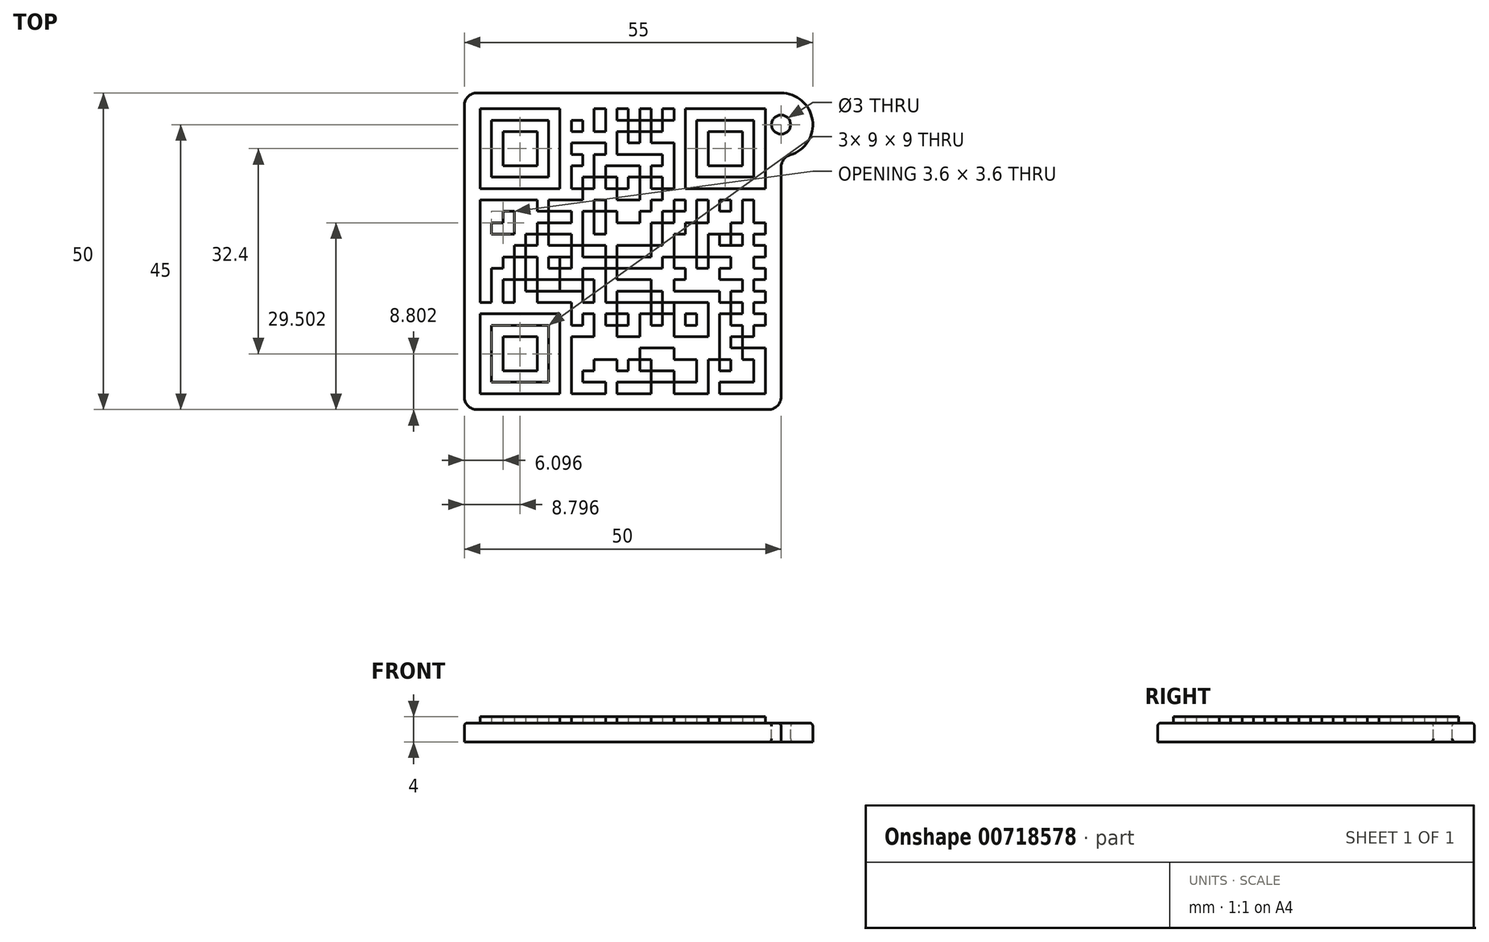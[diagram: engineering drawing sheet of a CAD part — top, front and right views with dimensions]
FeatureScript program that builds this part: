
annotation { "Feature Type Name" : "Feature", "Feature Type Description" : "" }
export const myFeature = defineFeature(function(context is Context, id is Id, definition is map)
    precondition{}
    {
        {
            var Q0;
            Q0=qCreatedBy(makeId("Top.planeOp"),FACE);
            var sketch = newSketch(context, id + "F0", { "sketchPlane" : qUnion([Q0])});
            skLineSegment(sketch, "E0.bottom", {"start": v(-25, 25) * mm, "end": v(25, 25) * mm});
            skLineSegment(sketch, "E0.top", {"start": v(-25, -25) * mm, "end": v(25, -25) * mm});
            skLineSegment(sketch, "E0.left", {"start": v(-25, 25) * mm, "end": v(-25, -25) * mm});
            skLineSegment(sketch, "E0.right", {"start": v(25, 15) * mm, "end": v(25, -25) * mm});
            skArc(sketch, "E1", {"start": v(25, 15) * mm, "mid": v(30, 20) * mm, "end": v(25, 25) * mm});
            skCircle(sketch, "E2", {"center": v(25, 20) * mm, "radius": 1.5 * mm});
            skSolve(sketch);
        }
        {
            var Q0;
            Q0 = qSketchRegion(id + "F0", true);
            extrude(context, id + "F1", {"entities" : qUnion([Q0]), "oppositeDirection" : true, "depth" : 3 * mm, "offsetDistance" : 25 * mm});
        }
        {
            var Q0;
            Q0=makeQuery(id+"F1.opExtrude","SWEPT_EDGE",EDGE,{"disambiguationData":[OSD([sQuery(id+"F0.wireOp",EDGE,"E0.top"),sQuery(id+"F0.wireOp",EDGE,"E0.left")])]});
            var Q1;
            Q1=makeQuery(id+"F1.opExtrude","SWEPT_EDGE",EDGE,{"disambiguationData":[OSD([sQuery(id+"F0.wireOp",EDGE,"E0.top"),sQuery(id+"F0.wireOp",EDGE,"E0.right")])]});
            var Q2;
            Q2=makeQuery(id+"F1.opExtrude","SWEPT_EDGE",EDGE,{"disambiguationData":[OSD([sQuery(id+"F0.wireOp",EDGE,"E0.right"),sQuery(id+"F0.wireOp",EDGE,"E1")])]});
            var Q3;
            Q3=makeQuery(id+"F1.opExtrude","SWEPT_EDGE",EDGE,{"disambiguationData":[OSD([sQuery(id+"F0.wireOp",EDGE,"E0.bottom"),sQuery(id+"F0.wireOp",EDGE,"E0.left")])]});
            fillet(context, id + "F2", {"entities" : qUnion([Q0, Q1, Q2, Q3]), "radius" : 2 * mm, "tangentPropagation" : true, "allowEdgeOverflow" : false});
        }
        {
            var Q0;
            Q0=qCreatedBy(makeId("Top.planeOp"),FACE);
            var sketch = newSketch(context, id + "F3", { "sketchPlane" : qUnion([Q0])});
            skLineSegment(sketch, "E3", {"start": v(22.5, 22.5) * mm, "end": v(22.5, -22.5) * mm});
            skLineSegment(sketch, "E4.1.0.0", {"start": v(20.7, 22.5) * mm, "end": v(20.7, -22.5) * mm});
            skLineSegment(sketch, "E4.2.0.0", {"start": v(18.9, 22.5) * mm, "end": v(18.9, -22.5) * mm});
            skLineSegment(sketch, "E4.3.0.0", {"start": v(17.1, 22.5) * mm, "end": v(17.1, -22.5) * mm});
            skLineSegment(sketch, "E4.4.0.0", {"start": v(15.3, 22.5) * mm, "end": v(15.3, -22.5) * mm});
            skLineSegment(sketch, "E4.5.0.0", {"start": v(13.5, 22.5) * mm, "end": v(13.5, -22.5) * mm});
            skLineSegment(sketch, "E4.6.0.0", {"start": v(11.7, 22.5) * mm, "end": v(11.7, -22.5) * mm});
            skLineSegment(sketch, "E4.7.0.0", {"start": v(9.9, 22.5) * mm, "end": v(9.9, -22.5) * mm});
            skLineSegment(sketch, "E4.8.0.0", {"start": v(8.1, 22.5) * mm, "end": v(8.1, -22.5) * mm});
            skLineSegment(sketch, "E4.9.0.0", {"start": v(6.3, 22.5) * mm, "end": v(6.3, -22.5) * mm});
            skLineSegment(sketch, "E4.direction1", {"start": v(22.5, -22.5) * mm, "end": v(20.7, -22.5) * mm, "construction": true});
            skLineSegment(sketch, "E5.0.10.0", {"start": v(4.5, 22.5) * mm, "end": v(4.5, -22.5) * mm});
            skLineSegment(sketch, "E5.0.11.0", {"start": v(2.7, 22.5) * mm, "end": v(2.7, -22.5) * mm});
            skLineSegment(sketch, "E6.0.12.0", {"start": v(0.9, 22.5) * mm, "end": v(0.9, -22.5) * mm});
            skLineSegment(sketch, "E6.0.13.0", {"start": v(-0.9, 22.5) * mm, "end": v(-0.9, -22.5) * mm});
            skLineSegment(sketch, "E6.0.14.0", {"start": v(-2.7, 22.5) * mm, "end": v(-2.7, -22.5) * mm});
            skLineSegment(sketch, "E6.0.15.0", {"start": v(-4.5, 22.5) * mm, "end": v(-4.5, -22.5) * mm});
            skLineSegment(sketch, "E6.0.16.0", {"start": v(-6.3, 22.5) * mm, "end": v(-6.3, -22.5) * mm});
            skLineSegment(sketch, "E6.0.17.0", {"start": v(-8.1, 22.5) * mm, "end": v(-8.1, -22.5) * mm});
            skLineSegment(sketch, "E6.0.18.0", {"start": v(-9.9, 22.5) * mm, "end": v(-9.9, -22.5) * mm});
            skLineSegment(sketch, "E6.0.19.0", {"start": v(-11.7, 22.5) * mm, "end": v(-11.7, -22.5) * mm});
            skLineSegment(sketch, "E6.0.20.0", {"start": v(-13.5, 22.5) * mm, "end": v(-13.5, -22.5) * mm});
            skLineSegment(sketch, "E6.0.21.0", {"start": v(-15.3, 22.5) * mm, "end": v(-15.3, -22.5) * mm});
            skLineSegment(sketch, "E6.0.22.0", {"start": v(-17.1, 22.5) * mm, "end": v(-17.1, -22.5) * mm});
            skLineSegment(sketch, "E6.0.23.0", {"start": v(-18.9, 22.5) * mm, "end": v(-18.9, -22.5) * mm});
            skLineSegment(sketch, "E6.0.24.0", {"start": v(-20.7, 22.5) * mm, "end": v(-20.7, -22.5) * mm});
            skLineSegment(sketch, "E6.0.25.0", {"start": v(-22.5, 22.5) * mm, "end": v(-22.5, -22.5) * mm});
            skLineSegment(sketch, "E7", {"start": v(-22.5, -22.5) * mm, "end": v(22.5, -22.5) * mm});
            skLineSegment(sketch, "E8.0.1.0", {"start": v(-22.5, -20.7) * mm, "end": v(22.5, -20.7) * mm});
            skLineSegment(sketch, "E8.0.2.0", {"start": v(-22.5, -18.9) * mm, "end": v(22.5, -18.9) * mm});
            skLineSegment(sketch, "E8.0.3.0", {"start": v(-22.5, -17.1) * mm, "end": v(22.5, -17.1) * mm});
            skLineSegment(sketch, "E8.0.4.0", {"start": v(-22.5, -15.3) * mm, "end": v(22.5, -15.3) * mm});
            skLineSegment(sketch, "E8.0.5.0", {"start": v(-22.5, -13.5) * mm, "end": v(22.5, -13.5) * mm});
            skLineSegment(sketch, "E8.0.6.0", {"start": v(-22.5, -11.7) * mm, "end": v(22.5, -11.7) * mm});
            skLineSegment(sketch, "E8.0.7.0", {"start": v(-22.5, -9.9) * mm, "end": v(22.5, -9.9) * mm});
            skLineSegment(sketch, "E8.0.8.0", {"start": v(-22.5, -8.1) * mm, "end": v(22.5, -8.1) * mm});
            skLineSegment(sketch, "E8.0.9.0", {"start": v(-22.5, -6.3) * mm, "end": v(22.5, -6.3) * mm});
            skLineSegment(sketch, "E8.0.10.0", {"start": v(-22.5, -4.5) * mm, "end": v(22.5, -4.5) * mm});
            skLineSegment(sketch, "E8.0.11.0", {"start": v(-22.5, -2.7) * mm, "end": v(22.5, -2.7) * mm});
            skLineSegment(sketch, "E8.0.12.0", {"start": v(-22.5, -0.9) * mm, "end": v(22.5, -0.9) * mm});
            skLineSegment(sketch, "E8.0.13.0", {"start": v(-22.5, 0.9) * mm, "end": v(22.5, 0.9) * mm});
            skLineSegment(sketch, "E8.0.14.0", {"start": v(-22.5, 2.7) * mm, "end": v(22.5, 2.7) * mm});
            skLineSegment(sketch, "E8.0.15.0", {"start": v(-22.5, 4.5) * mm, "end": v(22.5, 4.5) * mm});
            skLineSegment(sketch, "E8.0.16.0", {"start": v(-22.5, 6.3) * mm, "end": v(22.5, 6.3) * mm});
            skLineSegment(sketch, "E8.0.17.0", {"start": v(-22.5, 8.1) * mm, "end": v(22.5, 8.1) * mm});
            skLineSegment(sketch, "E8.0.18.0", {"start": v(-22.5, 9.9) * mm, "end": v(22.5, 9.9) * mm});
            skLineSegment(sketch, "E8.0.19.0", {"start": v(-22.5, 11.7) * mm, "end": v(22.5, 11.7) * mm});
            skLineSegment(sketch, "E8.0.20.0", {"start": v(-22.5, 13.5) * mm, "end": v(22.5, 13.5) * mm});
            skLineSegment(sketch, "E8.0.21.0", {"start": v(-22.5, 15.3) * mm, "end": v(22.5, 15.3) * mm});
            skLineSegment(sketch, "E8.0.22.0", {"start": v(-22.5, 17.1) * mm, "end": v(22.5, 17.1) * mm});
            skLineSegment(sketch, "E8.0.23.0", {"start": v(-22.5, 18.9) * mm, "end": v(22.5, 18.9) * mm});
            skLineSegment(sketch, "E8.0.24.0", {"start": v(-22.5, 20.7) * mm, "end": v(22.5, 20.7) * mm});
            skLineSegment(sketch, "E8.0.25.0", {"start": v(-22.5, 22.5) * mm, "end": v(22.5, 22.5) * mm});
            skLineSegment(sketch, "E8.direction1", {"start": v(-22.5, -22.5) * mm, "end": v(22.5, -22.5) * mm, "construction": true});
            skLineSegment(sketch, "E8.direction2", {"start": v(-22.5, -22.5) * mm, "end": v(-22.5, -20.7) * mm, "construction": true});
            skSolve(sketch);
        }
        {
            var Q0;
            {var subQ0=sQuery(id+"F3.wireOp",EDGE,"E8.0.25.0");var subQ1=sQuery(id+"F3.wireOp",EDGE,"E3");var subQ2=makeQuery(id+"F3.imprint","INTERSECT",VERTEX,{"derivedFrom":[subQ1,subQ0]});Q0=makeQuery(id+"F3.imprint","IMPRINT",FACE,{"disambiguationData":[TD([[makeQuery(id+"F3.imprint","IMPRINT",EDGE,{"disambiguationData":[TD([[subQ2,-1.0]])],"derivedFrom":subQ1}),-1.0]])]});}
            var Q1;
            {var subQ0=sQuery(id+"F3.wireOp",EDGE,"E7");var subQ1=sQuery(id+"F3.wireOp",EDGE,"E3");var subQ2=makeQuery(id+"F3.imprint","INTERSECT",VERTEX,{"derivedFrom":[subQ1,subQ0]});Q1=makeQuery(id+"F3.imprint","IMPRINT",FACE,{"disambiguationData":[TD([[makeQuery(id+"F3.imprint","IMPRINT",EDGE,{"disambiguationData":[TD([[subQ2,1.0]])],"derivedFrom":subQ1}),-1.0]])]});}
            var Q2;
            {var subQ0=sQuery(id+"F3.wireOp",EDGE,"E8.0.25.0");var subQ1=sQuery(id+"F3.wireOp",EDGE,"E6.0.24.0");var subQ2=makeQuery(id+"F3.imprint","INTERSECT",VERTEX,{"derivedFrom":[subQ1,subQ0]});Q2=makeQuery(id+"F3.imprint","IMPRINT",FACE,{"disambiguationData":[TD([[makeQuery(id+"F3.imprint","IMPRINT",EDGE,{"disambiguationData":[TD([[subQ2,-1.0]])],"derivedFrom":subQ1}),-1.0]])]});}
            var Q3;
            {var subQ0=sQuery(id+"F3.wireOp",EDGE,"E7");var subQ1=sQuery(id+"F3.wireOp",EDGE,"E6.0.24.0");var subQ2=makeQuery(id+"F3.imprint","INTERSECT",VERTEX,{"derivedFrom":[subQ1,subQ0]});Q3=makeQuery(id+"F3.imprint","IMPRINT",FACE,{"disambiguationData":[TD([[makeQuery(id+"F3.imprint","IMPRINT",EDGE,{"disambiguationData":[TD([[subQ2,1.0]])],"derivedFrom":subQ1}),-1.0]])]});}
            var Q4;
            {var subQ0=sQuery(id+"F3.wireOp",EDGE,"E8.0.23.0");var subQ1=sQuery(id+"F3.wireOp",EDGE,"E3");var subQ2=makeQuery(id+"F3.imprint","INTERSECT",VERTEX,{"derivedFrom":[subQ1,subQ0]});Q4=makeQuery(id+"F3.imprint","IMPRINT",FACE,{"disambiguationData":[TD([[makeQuery(id+"F3.imprint","IMPRINT",EDGE,{"disambiguationData":[TD([[subQ2,1.0]])],"derivedFrom":subQ1}),-1.0]])]});}
            var Q5;
            {var subQ0=sQuery(id+"F3.wireOp",EDGE,"E8.0.22.0");var subQ1=sQuery(id+"F3.wireOp",EDGE,"E3");var subQ2=makeQuery(id+"F3.imprint","INTERSECT",VERTEX,{"derivedFrom":[subQ1,subQ0]});Q5=makeQuery(id+"F3.imprint","IMPRINT",FACE,{"disambiguationData":[TD([[makeQuery(id+"F3.imprint","IMPRINT",EDGE,{"disambiguationData":[TD([[subQ2,1.0]])],"derivedFrom":subQ1}),-1.0]])]});}
            var Q6;
            {var subQ0=sQuery(id+"F3.wireOp",EDGE,"E8.0.21.0");var subQ1=sQuery(id+"F3.wireOp",EDGE,"E3");var subQ2=makeQuery(id+"F3.imprint","INTERSECT",VERTEX,{"derivedFrom":[subQ1,subQ0]});Q6=makeQuery(id+"F3.imprint","IMPRINT",FACE,{"disambiguationData":[TD([[makeQuery(id+"F3.imprint","IMPRINT",EDGE,{"disambiguationData":[TD([[subQ2,1.0]])],"derivedFrom":subQ1}),-1.0]])]});}
            var Q7;
            {var subQ0=sQuery(id+"F3.wireOp",EDGE,"E8.0.20.0");var subQ1=sQuery(id+"F3.wireOp",EDGE,"E3");var subQ2=makeQuery(id+"F3.imprint","INTERSECT",VERTEX,{"derivedFrom":[subQ1,subQ0]});Q7=makeQuery(id+"F3.imprint","IMPRINT",FACE,{"disambiguationData":[TD([[makeQuery(id+"F3.imprint","IMPRINT",EDGE,{"disambiguationData":[TD([[subQ2,1.0]])],"derivedFrom":subQ1}),-1.0]])]});}
            var Q8;
            {var subQ0=sQuery(id+"F3.wireOp",EDGE,"E8.0.19.0");var subQ1=sQuery(id+"F3.wireOp",EDGE,"E3");var subQ2=makeQuery(id+"F3.imprint","INTERSECT",VERTEX,{"derivedFrom":[subQ1,subQ0]});Q8=makeQuery(id+"F3.imprint","IMPRINT",FACE,{"disambiguationData":[TD([[makeQuery(id+"F3.imprint","IMPRINT",EDGE,{"disambiguationData":[TD([[subQ2,1.0]])],"derivedFrom":subQ1}),-1.0]])]});}
            var Q9;
            {var subQ0=sQuery(id+"F3.wireOp",EDGE,"E8.0.18.0");var subQ1=sQuery(id+"F3.wireOp",EDGE,"E3");var subQ2=makeQuery(id+"F3.imprint","INTERSECT",VERTEX,{"derivedFrom":[subQ1,subQ0]});Q9=makeQuery(id+"F3.imprint","IMPRINT",FACE,{"disambiguationData":[TD([[makeQuery(id+"F3.imprint","IMPRINT",EDGE,{"disambiguationData":[TD([[subQ2,1.0]])],"derivedFrom":subQ1}),-1.0]])]});}
            var Q10;
            {var subQ0=sQuery(id+"F3.wireOp",EDGE,"E8.0.14.0");var subQ1=sQuery(id+"F3.wireOp",EDGE,"E3");var subQ2=makeQuery(id+"F3.imprint","INTERSECT",VERTEX,{"derivedFrom":[subQ1,subQ0]});Q10=makeQuery(id+"F3.imprint","IMPRINT",FACE,{"disambiguationData":[TD([[makeQuery(id+"F3.imprint","IMPRINT",EDGE,{"disambiguationData":[TD([[subQ2,1.0]])],"derivedFrom":subQ1}),-1.0]])]});}
            var Q11;
            {var subQ0=sQuery(id+"F3.wireOp",EDGE,"E8.0.12.0");var subQ1=sQuery(id+"F3.wireOp",EDGE,"E3");var subQ2=makeQuery(id+"F3.imprint","INTERSECT",VERTEX,{"derivedFrom":[subQ1,subQ0]});Q11=makeQuery(id+"F3.imprint","IMPRINT",FACE,{"disambiguationData":[TD([[makeQuery(id+"F3.imprint","IMPRINT",EDGE,{"disambiguationData":[TD([[subQ2,1.0]])],"derivedFrom":subQ1}),-1.0]])]});}
            var Q12;
            {var subQ0=sQuery(id+"F3.wireOp",EDGE,"E8.0.10.0");var subQ1=sQuery(id+"F3.wireOp",EDGE,"E3");var subQ2=makeQuery(id+"F3.imprint","INTERSECT",VERTEX,{"derivedFrom":[subQ1,subQ0]});Q12=makeQuery(id+"F3.imprint","IMPRINT",FACE,{"disambiguationData":[TD([[makeQuery(id+"F3.imprint","IMPRINT",EDGE,{"disambiguationData":[TD([[subQ2,1.0]])],"derivedFrom":subQ1}),-1.0]])]});}
            var Q13;
            {var subQ0=sQuery(id+"F3.wireOp",EDGE,"E8.0.8.0");var subQ1=sQuery(id+"F3.wireOp",EDGE,"E3");var subQ2=makeQuery(id+"F3.imprint","INTERSECT",VERTEX,{"derivedFrom":[subQ1,subQ0]});Q13=makeQuery(id+"F3.imprint","IMPRINT",FACE,{"disambiguationData":[TD([[makeQuery(id+"F3.imprint","IMPRINT",EDGE,{"disambiguationData":[TD([[subQ2,1.0]])],"derivedFrom":subQ1}),-1.0]])]});}
            var Q14;
            {var subQ0=sQuery(id+"F3.wireOp",EDGE,"E8.0.6.0");var subQ1=sQuery(id+"F3.wireOp",EDGE,"E3");var subQ2=makeQuery(id+"F3.imprint","INTERSECT",VERTEX,{"derivedFrom":[subQ1,subQ0]});Q14=makeQuery(id+"F3.imprint","IMPRINT",FACE,{"disambiguationData":[TD([[makeQuery(id+"F3.imprint","IMPRINT",EDGE,{"disambiguationData":[TD([[subQ2,1.0]])],"derivedFrom":subQ1}),-1.0]])]});}
            var Q15;
            {var subQ0=sQuery(id+"F3.wireOp",EDGE,"E8.0.3.0");var subQ1=sQuery(id+"F3.wireOp",EDGE,"E3");var subQ2=makeQuery(id+"F3.imprint","INTERSECT",VERTEX,{"derivedFrom":[subQ1,subQ0]});Q15=makeQuery(id+"F3.imprint","IMPRINT",FACE,{"disambiguationData":[TD([[makeQuery(id+"F3.imprint","IMPRINT",EDGE,{"disambiguationData":[TD([[subQ2,1.0]])],"derivedFrom":subQ1}),-1.0]])]});}
            var Q16;
            {var subQ0=sQuery(id+"F3.wireOp",EDGE,"E8.0.2.0");var subQ1=sQuery(id+"F3.wireOp",EDGE,"E3");var subQ2=makeQuery(id+"F3.imprint","INTERSECT",VERTEX,{"derivedFrom":[subQ1,subQ0]});Q16=makeQuery(id+"F3.imprint","IMPRINT",FACE,{"disambiguationData":[TD([[makeQuery(id+"F3.imprint","IMPRINT",EDGE,{"disambiguationData":[TD([[subQ2,1.0]])],"derivedFrom":subQ1}),-1.0]])]});}
            var Q17;
            {var subQ0=sQuery(id+"F3.wireOp",EDGE,"E8.0.1.0");var subQ1=sQuery(id+"F3.wireOp",EDGE,"E3");var subQ2=makeQuery(id+"F3.imprint","INTERSECT",VERTEX,{"derivedFrom":[subQ1,subQ0]});Q17=makeQuery(id+"F3.imprint","IMPRINT",FACE,{"disambiguationData":[TD([[makeQuery(id+"F3.imprint","IMPRINT",EDGE,{"disambiguationData":[TD([[subQ2,1.0]])],"derivedFrom":subQ1}),-1.0]])]});}
            var Q18;
            {var subQ0=sQuery(id+"F3.wireOp",EDGE,"E8.0.25.0");var subQ1=sQuery(id+"F3.wireOp",EDGE,"E4.1.0.0");var subQ2=makeQuery(id+"F3.imprint","INTERSECT",VERTEX,{"derivedFrom":[subQ1,subQ0]});Q18=makeQuery(id+"F3.imprint","IMPRINT",FACE,{"disambiguationData":[TD([[makeQuery(id+"F3.imprint","IMPRINT",EDGE,{"disambiguationData":[TD([[subQ2,-1.0]])],"derivedFrom":subQ1}),-1.0]])]});}
            var Q19;
            {var subQ0=sQuery(id+"F3.wireOp",EDGE,"E7");var subQ1=sQuery(id+"F3.wireOp",EDGE,"E4.1.0.0");var subQ2=makeQuery(id+"F3.imprint","INTERSECT",VERTEX,{"derivedFrom":[subQ1,subQ0]});Q19=makeQuery(id+"F3.imprint","IMPRINT",FACE,{"disambiguationData":[TD([[makeQuery(id+"F3.imprint","IMPRINT",EDGE,{"disambiguationData":[TD([[subQ2,1.0]])],"derivedFrom":subQ1}),-1.0]])]});}
            var Q20;
            {var subQ0=sQuery(id+"F3.wireOp",EDGE,"E8.0.25.0");var subQ1=sQuery(id+"F3.wireOp",EDGE,"E4.2.0.0");var subQ2=makeQuery(id+"F3.imprint","INTERSECT",VERTEX,{"derivedFrom":[subQ1,subQ0]});Q20=makeQuery(id+"F3.imprint","IMPRINT",FACE,{"disambiguationData":[TD([[makeQuery(id+"F3.imprint","IMPRINT",EDGE,{"disambiguationData":[TD([[subQ2,-1.0]])],"derivedFrom":subQ1}),-1.0]])]});}
            var Q21;
            {var subQ0=sQuery(id+"F3.wireOp",EDGE,"E7");var subQ1=sQuery(id+"F3.wireOp",EDGE,"E4.2.0.0");var subQ2=makeQuery(id+"F3.imprint","INTERSECT",VERTEX,{"derivedFrom":[subQ1,subQ0]});Q21=makeQuery(id+"F3.imprint","IMPRINT",FACE,{"disambiguationData":[TD([[makeQuery(id+"F3.imprint","IMPRINT",EDGE,{"disambiguationData":[TD([[subQ2,1.0]])],"derivedFrom":subQ1}),-1.0]])]});}
            var Q22;
            {var subQ0=sQuery(id+"F3.wireOp",EDGE,"E8.0.25.0");var subQ1=sQuery(id+"F3.wireOp",EDGE,"E4.3.0.0");var subQ2=makeQuery(id+"F3.imprint","INTERSECT",VERTEX,{"derivedFrom":[subQ1,subQ0]});Q22=makeQuery(id+"F3.imprint","IMPRINT",FACE,{"disambiguationData":[TD([[makeQuery(id+"F3.imprint","IMPRINT",EDGE,{"disambiguationData":[TD([[subQ2,-1.0]])],"derivedFrom":subQ1}),-1.0]])]});}
            var Q23;
            {var subQ0=sQuery(id+"F3.wireOp",EDGE,"E7");var subQ1=sQuery(id+"F3.wireOp",EDGE,"E4.3.0.0");var subQ2=makeQuery(id+"F3.imprint","INTERSECT",VERTEX,{"derivedFrom":[subQ1,subQ0]});Q23=makeQuery(id+"F3.imprint","IMPRINT",FACE,{"disambiguationData":[TD([[makeQuery(id+"F3.imprint","IMPRINT",EDGE,{"disambiguationData":[TD([[subQ2,1.0]])],"derivedFrom":subQ1}),-1.0]])]});}
            var Q24;
            {var subQ0=sQuery(id+"F3.wireOp",EDGE,"E8.0.25.0");var subQ1=sQuery(id+"F3.wireOp",EDGE,"E4.4.0.0");var subQ2=makeQuery(id+"F3.imprint","INTERSECT",VERTEX,{"derivedFrom":[subQ1,subQ0]});Q24=makeQuery(id+"F3.imprint","IMPRINT",FACE,{"disambiguationData":[TD([[makeQuery(id+"F3.imprint","IMPRINT",EDGE,{"disambiguationData":[TD([[subQ2,-1.0]])],"derivedFrom":subQ1}),-1.0]])]});}
            var Q25;
            {var subQ0=sQuery(id+"F3.wireOp",EDGE,"E8.0.25.0");var subQ1=sQuery(id+"F3.wireOp",EDGE,"E4.5.0.0");var subQ2=makeQuery(id+"F3.imprint","INTERSECT",VERTEX,{"derivedFrom":[subQ1,subQ0]});Q25=makeQuery(id+"F3.imprint","IMPRINT",FACE,{"disambiguationData":[TD([[makeQuery(id+"F3.imprint","IMPRINT",EDGE,{"disambiguationData":[TD([[subQ2,-1.0]])],"derivedFrom":subQ1}),-1.0]])]});}
            var Q26;
            {var subQ0=sQuery(id+"F3.wireOp",EDGE,"E7");var subQ1=sQuery(id+"F3.wireOp",EDGE,"E4.5.0.0");var subQ2=makeQuery(id+"F3.imprint","INTERSECT",VERTEX,{"derivedFrom":[subQ1,subQ0]});Q26=makeQuery(id+"F3.imprint","IMPRINT",FACE,{"disambiguationData":[TD([[makeQuery(id+"F3.imprint","IMPRINT",EDGE,{"disambiguationData":[TD([[subQ2,1.0]])],"derivedFrom":subQ1}),-1.0]])]});}
            var Q27;
            {var subQ0=sQuery(id+"F3.wireOp",EDGE,"E8.0.25.0");var subQ1=sQuery(id+"F3.wireOp",EDGE,"E4.6.0.0");var subQ2=makeQuery(id+"F3.imprint","INTERSECT",VERTEX,{"derivedFrom":[subQ1,subQ0]});Q27=makeQuery(id+"F3.imprint","IMPRINT",FACE,{"disambiguationData":[TD([[makeQuery(id+"F3.imprint","IMPRINT",EDGE,{"disambiguationData":[TD([[subQ2,-1.0]])],"derivedFrom":subQ1}),-1.0]])]});}
            var Q28;
            {var subQ0=sQuery(id+"F3.wireOp",EDGE,"E7");var subQ1=sQuery(id+"F3.wireOp",EDGE,"E4.6.0.0");var subQ2=makeQuery(id+"F3.imprint","INTERSECT",VERTEX,{"derivedFrom":[subQ1,subQ0]});Q28=makeQuery(id+"F3.imprint","IMPRINT",FACE,{"disambiguationData":[TD([[makeQuery(id+"F3.imprint","IMPRINT",EDGE,{"disambiguationData":[TD([[subQ2,1.0]])],"derivedFrom":subQ1}),-1.0]])]});}
            var Q29;
            {var subQ0=sQuery(id+"F3.wireOp",EDGE,"E7");var subQ1=sQuery(id+"F3.wireOp",EDGE,"E4.7.0.0");var subQ2=makeQuery(id+"F3.imprint","INTERSECT",VERTEX,{"derivedFrom":[subQ1,subQ0]});Q29=makeQuery(id+"F3.imprint","IMPRINT",FACE,{"disambiguationData":[TD([[makeQuery(id+"F3.imprint","IMPRINT",EDGE,{"disambiguationData":[TD([[subQ2,1.0]])],"derivedFrom":subQ1}),-1.0]])]});}
            var Q30;
            {var subQ0=sQuery(id+"F3.wireOp",EDGE,"E7");var subQ1=sQuery(id+"F3.wireOp",EDGE,"E5.0.10.0");var subQ2=makeQuery(id+"F3.imprint","INTERSECT",VERTEX,{"derivedFrom":[subQ1,subQ0]});Q30=makeQuery(id+"F3.imprint","IMPRINT",FACE,{"disambiguationData":[TD([[makeQuery(id+"F3.imprint","IMPRINT",EDGE,{"disambiguationData":[TD([[subQ2,1.0]])],"derivedFrom":subQ1}),-1.0]])]});}
            var Q31;
            {var subQ0=sQuery(id+"F3.wireOp",EDGE,"E7");var subQ1=sQuery(id+"F3.wireOp",EDGE,"E5.0.11.0");var subQ2=makeQuery(id+"F3.imprint","INTERSECT",VERTEX,{"derivedFrom":[subQ1,subQ0]});Q31=makeQuery(id+"F3.imprint","IMPRINT",FACE,{"disambiguationData":[TD([[makeQuery(id+"F3.imprint","IMPRINT",EDGE,{"disambiguationData":[TD([[subQ2,1.0]])],"derivedFrom":subQ1}),-1.0]])]});}
            var Q32;
            {var subQ0=sQuery(id+"F3.wireOp",EDGE,"E7");var subQ1=sQuery(id+"F3.wireOp",EDGE,"E6.0.12.0");var subQ2=makeQuery(id+"F3.imprint","INTERSECT",VERTEX,{"derivedFrom":[subQ1,subQ0]});Q32=makeQuery(id+"F3.imprint","IMPRINT",FACE,{"disambiguationData":[TD([[makeQuery(id+"F3.imprint","IMPRINT",EDGE,{"disambiguationData":[TD([[subQ2,1.0]])],"derivedFrom":subQ1}),-1.0]])]});}
            var Q33;
            {var subQ0=sQuery(id+"F3.wireOp",EDGE,"E8.0.25.0");var subQ1=sQuery(id+"F3.wireOp",EDGE,"E6.0.14.0");var subQ2=makeQuery(id+"F3.imprint","INTERSECT",VERTEX,{"derivedFrom":[subQ1,subQ0]});Q33=makeQuery(id+"F3.imprint","IMPRINT",FACE,{"disambiguationData":[TD([[makeQuery(id+"F3.imprint","IMPRINT",EDGE,{"disambiguationData":[TD([[subQ2,-1.0]])],"derivedFrom":subQ1}),-1.0]])]});}
            var Q34;
            {var subQ0=sQuery(id+"F3.wireOp",EDGE,"E7");var subQ1=sQuery(id+"F3.wireOp",EDGE,"E6.0.14.0");var subQ2=makeQuery(id+"F3.imprint","INTERSECT",VERTEX,{"derivedFrom":[subQ1,subQ0]});Q34=makeQuery(id+"F3.imprint","IMPRINT",FACE,{"disambiguationData":[TD([[makeQuery(id+"F3.imprint","IMPRINT",EDGE,{"disambiguationData":[TD([[subQ2,1.0]])],"derivedFrom":subQ1}),-1.0]])]});}
            var Q35;
            {var subQ0=sQuery(id+"F3.wireOp",EDGE,"E7");var subQ1=sQuery(id+"F3.wireOp",EDGE,"E6.0.15.0");var subQ2=makeQuery(id+"F3.imprint","INTERSECT",VERTEX,{"derivedFrom":[subQ1,subQ0]});Q35=makeQuery(id+"F3.imprint","IMPRINT",FACE,{"disambiguationData":[TD([[makeQuery(id+"F3.imprint","IMPRINT",EDGE,{"disambiguationData":[TD([[subQ2,1.0]])],"derivedFrom":subQ1}),-1.0]])]});}
            var Q36;
            {var subQ0=sQuery(id+"F3.wireOp",EDGE,"E7");var subQ1=sQuery(id+"F3.wireOp",EDGE,"E6.0.16.0");var subQ2=makeQuery(id+"F3.imprint","INTERSECT",VERTEX,{"derivedFrom":[subQ1,subQ0]});Q36=makeQuery(id+"F3.imprint","IMPRINT",FACE,{"disambiguationData":[TD([[makeQuery(id+"F3.imprint","IMPRINT",EDGE,{"disambiguationData":[TD([[subQ2,1.0]])],"derivedFrom":subQ1}),-1.0]])]});}
            var Q37;
            {var subQ0=sQuery(id+"F3.wireOp",EDGE,"E8.0.25.0");var subQ1=sQuery(id+"F3.wireOp",EDGE,"E6.0.18.0");var subQ2=makeQuery(id+"F3.imprint","INTERSECT",VERTEX,{"derivedFrom":[subQ1,subQ0]});Q37=makeQuery(id+"F3.imprint","IMPRINT",FACE,{"disambiguationData":[TD([[makeQuery(id+"F3.imprint","IMPRINT",EDGE,{"disambiguationData":[TD([[subQ2,-1.0]])],"derivedFrom":subQ1}),-1.0]])]});}
            var Q38;
            {var subQ0=sQuery(id+"F3.wireOp",EDGE,"E7");var subQ1=sQuery(id+"F3.wireOp",EDGE,"E6.0.18.0");var subQ2=makeQuery(id+"F3.imprint","INTERSECT",VERTEX,{"derivedFrom":[subQ1,subQ0]});Q38=makeQuery(id+"F3.imprint","IMPRINT",FACE,{"disambiguationData":[TD([[makeQuery(id+"F3.imprint","IMPRINT",EDGE,{"disambiguationData":[TD([[subQ2,1.0]])],"derivedFrom":subQ1}),-1.0]])]});}
            var Q39;
            {var subQ0=sQuery(id+"F3.wireOp",EDGE,"E8.0.25.0");var subQ1=sQuery(id+"F3.wireOp",EDGE,"E6.0.19.0");var subQ2=makeQuery(id+"F3.imprint","INTERSECT",VERTEX,{"derivedFrom":[subQ1,subQ0]});Q39=makeQuery(id+"F3.imprint","IMPRINT",FACE,{"disambiguationData":[TD([[makeQuery(id+"F3.imprint","IMPRINT",EDGE,{"disambiguationData":[TD([[subQ2,-1.0]])],"derivedFrom":subQ1}),-1.0]])]});}
            var Q40;
            {var subQ0=sQuery(id+"F3.wireOp",EDGE,"E7");var subQ1=sQuery(id+"F3.wireOp",EDGE,"E6.0.19.0");var subQ2=makeQuery(id+"F3.imprint","INTERSECT",VERTEX,{"derivedFrom":[subQ1,subQ0]});Q40=makeQuery(id+"F3.imprint","IMPRINT",FACE,{"disambiguationData":[TD([[makeQuery(id+"F3.imprint","IMPRINT",EDGE,{"disambiguationData":[TD([[subQ2,1.0]])],"derivedFrom":subQ1}),-1.0]])]});}
            var Q41;
            {var subQ0=sQuery(id+"F3.wireOp",EDGE,"E8.0.25.0");var subQ1=sQuery(id+"F3.wireOp",EDGE,"E6.0.20.0");var subQ2=makeQuery(id+"F3.imprint","INTERSECT",VERTEX,{"derivedFrom":[subQ1,subQ0]});Q41=makeQuery(id+"F3.imprint","IMPRINT",FACE,{"disambiguationData":[TD([[makeQuery(id+"F3.imprint","IMPRINT",EDGE,{"disambiguationData":[TD([[subQ2,-1.0]])],"derivedFrom":subQ1}),-1.0]])]});}
            var Q42;
            {var subQ0=sQuery(id+"F3.wireOp",EDGE,"E7");var subQ1=sQuery(id+"F3.wireOp",EDGE,"E6.0.20.0");var subQ2=makeQuery(id+"F3.imprint","INTERSECT",VERTEX,{"derivedFrom":[subQ1,subQ0]});Q42=makeQuery(id+"F3.imprint","IMPRINT",FACE,{"disambiguationData":[TD([[makeQuery(id+"F3.imprint","IMPRINT",EDGE,{"disambiguationData":[TD([[subQ2,1.0]])],"derivedFrom":subQ1}),-1.0]])]});}
            var Q43;
            {var subQ0=sQuery(id+"F3.wireOp",EDGE,"E8.0.25.0");var subQ1=sQuery(id+"F3.wireOp",EDGE,"E6.0.21.0");var subQ2=makeQuery(id+"F3.imprint","INTERSECT",VERTEX,{"derivedFrom":[subQ1,subQ0]});Q43=makeQuery(id+"F3.imprint","IMPRINT",FACE,{"disambiguationData":[TD([[makeQuery(id+"F3.imprint","IMPRINT",EDGE,{"disambiguationData":[TD([[subQ2,-1.0]])],"derivedFrom":subQ1}),-1.0]])]});}
            var Q44;
            {var subQ0=sQuery(id+"F3.wireOp",EDGE,"E7");var subQ1=sQuery(id+"F3.wireOp",EDGE,"E6.0.21.0");var subQ2=makeQuery(id+"F3.imprint","INTERSECT",VERTEX,{"derivedFrom":[subQ1,subQ0]});Q44=makeQuery(id+"F3.imprint","IMPRINT",FACE,{"disambiguationData":[TD([[makeQuery(id+"F3.imprint","IMPRINT",EDGE,{"disambiguationData":[TD([[subQ2,1.0]])],"derivedFrom":subQ1}),-1.0]])]});}
            var Q45;
            {var subQ0=sQuery(id+"F3.wireOp",EDGE,"E8.0.25.0");var subQ1=sQuery(id+"F3.wireOp",EDGE,"E6.0.22.0");var subQ2=makeQuery(id+"F3.imprint","INTERSECT",VERTEX,{"derivedFrom":[subQ1,subQ0]});Q45=makeQuery(id+"F3.imprint","IMPRINT",FACE,{"disambiguationData":[TD([[makeQuery(id+"F3.imprint","IMPRINT",EDGE,{"disambiguationData":[TD([[subQ2,-1.0]])],"derivedFrom":subQ1}),-1.0]])]});}
            var Q46;
            {var subQ0=sQuery(id+"F3.wireOp",EDGE,"E7");var subQ1=sQuery(id+"F3.wireOp",EDGE,"E6.0.22.0");var subQ2=makeQuery(id+"F3.imprint","INTERSECT",VERTEX,{"derivedFrom":[subQ1,subQ0]});Q46=makeQuery(id+"F3.imprint","IMPRINT",FACE,{"disambiguationData":[TD([[makeQuery(id+"F3.imprint","IMPRINT",EDGE,{"disambiguationData":[TD([[subQ2,1.0]])],"derivedFrom":subQ1}),-1.0]])]});}
            var Q47;
            {var subQ0=sQuery(id+"F3.wireOp",EDGE,"E8.0.25.0");var subQ1=sQuery(id+"F3.wireOp",EDGE,"E6.0.23.0");var subQ2=makeQuery(id+"F3.imprint","INTERSECT",VERTEX,{"derivedFrom":[subQ1,subQ0]});Q47=makeQuery(id+"F3.imprint","IMPRINT",FACE,{"disambiguationData":[TD([[makeQuery(id+"F3.imprint","IMPRINT",EDGE,{"disambiguationData":[TD([[subQ2,-1.0]])],"derivedFrom":subQ1}),-1.0]])]});}
            var Q48;
            {var subQ0=sQuery(id+"F3.wireOp",EDGE,"E7");var subQ1=sQuery(id+"F3.wireOp",EDGE,"E6.0.23.0");var subQ2=makeQuery(id+"F3.imprint","INTERSECT",VERTEX,{"derivedFrom":[subQ1,subQ0]});Q48=makeQuery(id+"F3.imprint","IMPRINT",FACE,{"disambiguationData":[TD([[makeQuery(id+"F3.imprint","IMPRINT",EDGE,{"disambiguationData":[TD([[subQ2,1.0]])],"derivedFrom":subQ1}),-1.0]])]});}
            var Q49;
            {var subQ0=sQuery(id+"F3.wireOp",EDGE,"E8.0.24.0");var subQ1=sQuery(id+"F3.wireOp",EDGE,"E6.0.24.0");var subQ2=makeQuery(id+"F3.imprint","INTERSECT",VERTEX,{"derivedFrom":[subQ1,subQ0]});Q49=makeQuery(id+"F3.imprint","IMPRINT",FACE,{"disambiguationData":[TD([[makeQuery(id+"F3.imprint","IMPRINT",EDGE,{"disambiguationData":[TD([[subQ2,-1.0]])],"derivedFrom":subQ1}),-1.0]])]});}
            var Q50;
            {var subQ0=sQuery(id+"F3.wireOp",EDGE,"E8.0.23.0");var subQ1=sQuery(id+"F3.wireOp",EDGE,"E6.0.24.0");var subQ2=makeQuery(id+"F3.imprint","INTERSECT",VERTEX,{"derivedFrom":[subQ1,subQ0]});Q50=makeQuery(id+"F3.imprint","IMPRINT",FACE,{"disambiguationData":[TD([[makeQuery(id+"F3.imprint","IMPRINT",EDGE,{"disambiguationData":[TD([[subQ2,-1.0]])],"derivedFrom":subQ1}),-1.0]])]});}
            var Q51;
            {var subQ0=sQuery(id+"F3.wireOp",EDGE,"E8.0.22.0");var subQ1=sQuery(id+"F3.wireOp",EDGE,"E6.0.24.0");var subQ2=makeQuery(id+"F3.imprint","INTERSECT",VERTEX,{"derivedFrom":[subQ1,subQ0]});Q51=makeQuery(id+"F3.imprint","IMPRINT",FACE,{"disambiguationData":[TD([[makeQuery(id+"F3.imprint","IMPRINT",EDGE,{"disambiguationData":[TD([[subQ2,-1.0]])],"derivedFrom":subQ1}),-1.0]])]});}
            var Q52;
            {var subQ0=sQuery(id+"F3.wireOp",EDGE,"E8.0.21.0");var subQ1=sQuery(id+"F3.wireOp",EDGE,"E6.0.24.0");var subQ2=makeQuery(id+"F3.imprint","INTERSECT",VERTEX,{"derivedFrom":[subQ1,subQ0]});Q52=makeQuery(id+"F3.imprint","IMPRINT",FACE,{"disambiguationData":[TD([[makeQuery(id+"F3.imprint","IMPRINT",EDGE,{"disambiguationData":[TD([[subQ2,-1.0]])],"derivedFrom":subQ1}),-1.0]])]});}
            var Q53;
            {var subQ0=sQuery(id+"F3.wireOp",EDGE,"E8.0.20.0");var subQ1=sQuery(id+"F3.wireOp",EDGE,"E6.0.24.0");var subQ2=makeQuery(id+"F3.imprint","INTERSECT",VERTEX,{"derivedFrom":[subQ1,subQ0]});Q53=makeQuery(id+"F3.imprint","IMPRINT",FACE,{"disambiguationData":[TD([[makeQuery(id+"F3.imprint","IMPRINT",EDGE,{"disambiguationData":[TD([[subQ2,-1.0]])],"derivedFrom":subQ1}),-1.0]])]});}
            var Q54;
            {var subQ0=sQuery(id+"F3.wireOp",EDGE,"E8.0.19.0");var subQ1=sQuery(id+"F3.wireOp",EDGE,"E6.0.24.0");var subQ2=makeQuery(id+"F3.imprint","INTERSECT",VERTEX,{"derivedFrom":[subQ1,subQ0]});Q54=makeQuery(id+"F3.imprint","IMPRINT",FACE,{"disambiguationData":[TD([[makeQuery(id+"F3.imprint","IMPRINT",EDGE,{"disambiguationData":[TD([[subQ2,-1.0]])],"derivedFrom":subQ1}),-1.0]])]});}
            var Q55;
            {var subQ0=sQuery(id+"F3.wireOp",EDGE,"E8.0.17.0");var subQ1=sQuery(id+"F3.wireOp",EDGE,"E6.0.24.0");var subQ2=makeQuery(id+"F3.imprint","INTERSECT",VERTEX,{"derivedFrom":[subQ1,subQ0]});Q55=makeQuery(id+"F3.imprint","IMPRINT",FACE,{"disambiguationData":[TD([[makeQuery(id+"F3.imprint","IMPRINT",EDGE,{"disambiguationData":[TD([[subQ2,-1.0]])],"derivedFrom":subQ1}),-1.0]])]});}
            var Q56;
            {var subQ0=sQuery(id+"F3.wireOp",EDGE,"E8.0.16.0");var subQ1=sQuery(id+"F3.wireOp",EDGE,"E6.0.24.0");var subQ2=makeQuery(id+"F3.imprint","INTERSECT",VERTEX,{"derivedFrom":[subQ1,subQ0]});Q56=makeQuery(id+"F3.imprint","IMPRINT",FACE,{"disambiguationData":[TD([[makeQuery(id+"F3.imprint","IMPRINT",EDGE,{"disambiguationData":[TD([[subQ2,-1.0]])],"derivedFrom":subQ1}),-1.0]])]});}
            var Q57;
            {var subQ0=sQuery(id+"F3.wireOp",EDGE,"E8.0.15.0");var subQ1=sQuery(id+"F3.wireOp",EDGE,"E6.0.24.0");var subQ2=makeQuery(id+"F3.imprint","INTERSECT",VERTEX,{"derivedFrom":[subQ1,subQ0]});Q57=makeQuery(id+"F3.imprint","IMPRINT",FACE,{"disambiguationData":[TD([[makeQuery(id+"F3.imprint","IMPRINT",EDGE,{"disambiguationData":[TD([[subQ2,-1.0]])],"derivedFrom":subQ1}),-1.0]])]});}
            var Q58;
            {var subQ0=sQuery(id+"F3.wireOp",EDGE,"E8.0.14.0");var subQ1=sQuery(id+"F3.wireOp",EDGE,"E6.0.24.0");var subQ2=makeQuery(id+"F3.imprint","INTERSECT",VERTEX,{"derivedFrom":[subQ1,subQ0]});Q58=makeQuery(id+"F3.imprint","IMPRINT",FACE,{"disambiguationData":[TD([[makeQuery(id+"F3.imprint","IMPRINT",EDGE,{"disambiguationData":[TD([[subQ2,-1.0]])],"derivedFrom":subQ1}),-1.0]])]});}
            var Q59;
            {var subQ0=sQuery(id+"F3.wireOp",EDGE,"E8.0.13.0");var subQ1=sQuery(id+"F3.wireOp",EDGE,"E6.0.24.0");var subQ2=makeQuery(id+"F3.imprint","INTERSECT",VERTEX,{"derivedFrom":[subQ1,subQ0]});Q59=makeQuery(id+"F3.imprint","IMPRINT",FACE,{"disambiguationData":[TD([[makeQuery(id+"F3.imprint","IMPRINT",EDGE,{"disambiguationData":[TD([[subQ2,-1.0]])],"derivedFrom":subQ1}),-1.0]])]});}
            var Q60;
            {var subQ0=sQuery(id+"F3.wireOp",EDGE,"E8.0.12.0");var subQ1=sQuery(id+"F3.wireOp",EDGE,"E6.0.24.0");var subQ2=makeQuery(id+"F3.imprint","INTERSECT",VERTEX,{"derivedFrom":[subQ1,subQ0]});Q60=makeQuery(id+"F3.imprint","IMPRINT",FACE,{"disambiguationData":[TD([[makeQuery(id+"F3.imprint","IMPRINT",EDGE,{"disambiguationData":[TD([[subQ2,-1.0]])],"derivedFrom":subQ1}),-1.0]])]});}
            var Q61;
            {var subQ0=sQuery(id+"F3.wireOp",EDGE,"E8.0.11.0");var subQ1=sQuery(id+"F3.wireOp",EDGE,"E6.0.24.0");var subQ2=makeQuery(id+"F3.imprint","INTERSECT",VERTEX,{"derivedFrom":[subQ1,subQ0]});Q61=makeQuery(id+"F3.imprint","IMPRINT",FACE,{"disambiguationData":[TD([[makeQuery(id+"F3.imprint","IMPRINT",EDGE,{"disambiguationData":[TD([[subQ2,-1.0]])],"derivedFrom":subQ1}),-1.0]])]});}
            var Q62;
            {var subQ0=sQuery(id+"F3.wireOp",EDGE,"E8.0.10.0");var subQ1=sQuery(id+"F3.wireOp",EDGE,"E6.0.24.0");var subQ2=makeQuery(id+"F3.imprint","INTERSECT",VERTEX,{"derivedFrom":[subQ1,subQ0]});Q62=makeQuery(id+"F3.imprint","IMPRINT",FACE,{"disambiguationData":[TD([[makeQuery(id+"F3.imprint","IMPRINT",EDGE,{"disambiguationData":[TD([[subQ2,-1.0]])],"derivedFrom":subQ1}),-1.0]])]});}
            var Q63;
            {var subQ0=sQuery(id+"F3.wireOp",EDGE,"E8.0.9.0");var subQ1=sQuery(id+"F3.wireOp",EDGE,"E6.0.24.0");var subQ2=makeQuery(id+"F3.imprint","INTERSECT",VERTEX,{"derivedFrom":[subQ1,subQ0]});Q63=makeQuery(id+"F3.imprint","IMPRINT",FACE,{"disambiguationData":[TD([[makeQuery(id+"F3.imprint","IMPRINT",EDGE,{"disambiguationData":[TD([[subQ2,-1.0]])],"derivedFrom":subQ1}),-1.0]])]});}
            var Q64;
            {var subQ0=sQuery(id+"F3.wireOp",EDGE,"E8.0.7.0");var subQ1=sQuery(id+"F3.wireOp",EDGE,"E6.0.24.0");var subQ2=makeQuery(id+"F3.imprint","INTERSECT",VERTEX,{"derivedFrom":[subQ1,subQ0]});Q64=makeQuery(id+"F3.imprint","IMPRINT",FACE,{"disambiguationData":[TD([[makeQuery(id+"F3.imprint","IMPRINT",EDGE,{"disambiguationData":[TD([[subQ2,-1.0]])],"derivedFrom":subQ1}),-1.0]])]});}
            var Q65;
            {var subQ0=sQuery(id+"F3.wireOp",EDGE,"E8.0.6.0");var subQ1=sQuery(id+"F3.wireOp",EDGE,"E6.0.24.0");var subQ2=makeQuery(id+"F3.imprint","INTERSECT",VERTEX,{"derivedFrom":[subQ1,subQ0]});Q65=makeQuery(id+"F3.imprint","IMPRINT",FACE,{"disambiguationData":[TD([[makeQuery(id+"F3.imprint","IMPRINT",EDGE,{"disambiguationData":[TD([[subQ2,-1.0]])],"derivedFrom":subQ1}),-1.0]])]});}
            var Q66;
            {var subQ0=sQuery(id+"F3.wireOp",EDGE,"E8.0.5.0");var subQ1=sQuery(id+"F3.wireOp",EDGE,"E6.0.24.0");var subQ2=makeQuery(id+"F3.imprint","INTERSECT",VERTEX,{"derivedFrom":[subQ1,subQ0]});Q66=makeQuery(id+"F3.imprint","IMPRINT",FACE,{"disambiguationData":[TD([[makeQuery(id+"F3.imprint","IMPRINT",EDGE,{"disambiguationData":[TD([[subQ2,-1.0]])],"derivedFrom":subQ1}),-1.0]])]});}
            var Q67;
            {var subQ0=sQuery(id+"F3.wireOp",EDGE,"E8.0.4.0");var subQ1=sQuery(id+"F3.wireOp",EDGE,"E6.0.24.0");var subQ2=makeQuery(id+"F3.imprint","INTERSECT",VERTEX,{"derivedFrom":[subQ1,subQ0]});Q67=makeQuery(id+"F3.imprint","IMPRINT",FACE,{"disambiguationData":[TD([[makeQuery(id+"F3.imprint","IMPRINT",EDGE,{"disambiguationData":[TD([[subQ2,-1.0]])],"derivedFrom":subQ1}),-1.0]])]});}
            var Q68;
            {var subQ0=sQuery(id+"F3.wireOp",EDGE,"E8.0.3.0");var subQ1=sQuery(id+"F3.wireOp",EDGE,"E6.0.24.0");var subQ2=makeQuery(id+"F3.imprint","INTERSECT",VERTEX,{"derivedFrom":[subQ1,subQ0]});Q68=makeQuery(id+"F3.imprint","IMPRINT",FACE,{"disambiguationData":[TD([[makeQuery(id+"F3.imprint","IMPRINT",EDGE,{"disambiguationData":[TD([[subQ2,-1.0]])],"derivedFrom":subQ1}),-1.0]])]});}
            var Q69;
            {var subQ0=sQuery(id+"F3.wireOp",EDGE,"E8.0.2.0");var subQ1=sQuery(id+"F3.wireOp",EDGE,"E6.0.24.0");var subQ2=makeQuery(id+"F3.imprint","INTERSECT",VERTEX,{"derivedFrom":[subQ1,subQ0]});Q69=makeQuery(id+"F3.imprint","IMPRINT",FACE,{"disambiguationData":[TD([[makeQuery(id+"F3.imprint","IMPRINT",EDGE,{"disambiguationData":[TD([[subQ2,-1.0]])],"derivedFrom":subQ1}),-1.0]])]});}
            var Q70;
            {var subQ0=sQuery(id+"F3.wireOp",EDGE,"E8.0.19.0");var subQ1=sQuery(id+"F3.wireOp",EDGE,"E6.0.23.0");var subQ2=makeQuery(id+"F3.imprint","INTERSECT",VERTEX,{"derivedFrom":[subQ1,subQ0]});Q70=makeQuery(id+"F3.imprint","IMPRINT",FACE,{"disambiguationData":[TD([[makeQuery(id+"F3.imprint","IMPRINT",EDGE,{"disambiguationData":[TD([[subQ2,-1.0]])],"derivedFrom":subQ1}),-1.0]])]});}
            var Q71;
            {var subQ0=sQuery(id+"F3.wireOp",EDGE,"E8.0.19.0");var subQ1=sQuery(id+"F3.wireOp",EDGE,"E6.0.22.0");var subQ2=makeQuery(id+"F3.imprint","INTERSECT",VERTEX,{"derivedFrom":[subQ1,subQ0]});Q71=makeQuery(id+"F3.imprint","IMPRINT",FACE,{"disambiguationData":[TD([[makeQuery(id+"F3.imprint","IMPRINT",EDGE,{"disambiguationData":[TD([[subQ2,-1.0]])],"derivedFrom":subQ1}),-1.0]])]});}
            var Q72;
            {var subQ0=sQuery(id+"F3.wireOp",EDGE,"E8.0.19.0");var subQ1=sQuery(id+"F3.wireOp",EDGE,"E6.0.21.0");var subQ2=makeQuery(id+"F3.imprint","INTERSECT",VERTEX,{"derivedFrom":[subQ1,subQ0]});Q72=makeQuery(id+"F3.imprint","IMPRINT",FACE,{"disambiguationData":[TD([[makeQuery(id+"F3.imprint","IMPRINT",EDGE,{"disambiguationData":[TD([[subQ2,-1.0]])],"derivedFrom":subQ1}),-1.0]])]});}
            var Q73;
            {var subQ0=sQuery(id+"F3.wireOp",EDGE,"E8.0.19.0");var subQ1=sQuery(id+"F3.wireOp",EDGE,"E6.0.20.0");var subQ2=makeQuery(id+"F3.imprint","INTERSECT",VERTEX,{"derivedFrom":[subQ1,subQ0]});Q73=makeQuery(id+"F3.imprint","IMPRINT",FACE,{"disambiguationData":[TD([[makeQuery(id+"F3.imprint","IMPRINT",EDGE,{"disambiguationData":[TD([[subQ2,-1.0]])],"derivedFrom":subQ1}),-1.0]])]});}
            var Q74;
            {var subQ0=sQuery(id+"F3.wireOp",EDGE,"E8.0.19.0");var subQ1=sQuery(id+"F3.wireOp",EDGE,"E6.0.19.0");var subQ2=makeQuery(id+"F3.imprint","INTERSECT",VERTEX,{"derivedFrom":[subQ1,subQ0]});Q74=makeQuery(id+"F3.imprint","IMPRINT",FACE,{"disambiguationData":[TD([[makeQuery(id+"F3.imprint","IMPRINT",EDGE,{"disambiguationData":[TD([[subQ2,-1.0]])],"derivedFrom":subQ1}),-1.0]])]});}
            var Q75;
            {var subQ0=sQuery(id+"F3.wireOp",EDGE,"E8.0.19.0");var subQ1=sQuery(id+"F3.wireOp",EDGE,"E6.0.18.0");var subQ2=makeQuery(id+"F3.imprint","INTERSECT",VERTEX,{"derivedFrom":[subQ1,subQ0]});Q75=makeQuery(id+"F3.imprint","IMPRINT",FACE,{"disambiguationData":[TD([[makeQuery(id+"F3.imprint","IMPRINT",EDGE,{"disambiguationData":[TD([[subQ2,-1.0]])],"derivedFrom":subQ1}),-1.0]])]});}
            var Q76;
            {var subQ0=sQuery(id+"F3.wireOp",EDGE,"E8.0.20.0");var subQ1=sQuery(id+"F3.wireOp",EDGE,"E6.0.18.0");var subQ2=makeQuery(id+"F3.imprint","INTERSECT",VERTEX,{"derivedFrom":[subQ1,subQ0]});Q76=makeQuery(id+"F3.imprint","IMPRINT",FACE,{"disambiguationData":[TD([[makeQuery(id+"F3.imprint","IMPRINT",EDGE,{"disambiguationData":[TD([[subQ2,-1.0]])],"derivedFrom":subQ1}),-1.0]])]});}
            var Q77;
            {var subQ0=sQuery(id+"F3.wireOp",EDGE,"E8.0.21.0");var subQ1=sQuery(id+"F3.wireOp",EDGE,"E6.0.18.0");var subQ2=makeQuery(id+"F3.imprint","INTERSECT",VERTEX,{"derivedFrom":[subQ1,subQ0]});Q77=makeQuery(id+"F3.imprint","IMPRINT",FACE,{"disambiguationData":[TD([[makeQuery(id+"F3.imprint","IMPRINT",EDGE,{"disambiguationData":[TD([[subQ2,-1.0]])],"derivedFrom":subQ1}),-1.0]])]});}
            var Q78;
            {var subQ0=sQuery(id+"F3.wireOp",EDGE,"E8.0.22.0");var subQ1=sQuery(id+"F3.wireOp",EDGE,"E6.0.18.0");var subQ2=makeQuery(id+"F3.imprint","INTERSECT",VERTEX,{"derivedFrom":[subQ1,subQ0]});Q78=makeQuery(id+"F3.imprint","IMPRINT",FACE,{"disambiguationData":[TD([[makeQuery(id+"F3.imprint","IMPRINT",EDGE,{"disambiguationData":[TD([[subQ2,-1.0]])],"derivedFrom":subQ1}),-1.0]])]});}
            var Q79;
            {var subQ0=sQuery(id+"F3.wireOp",EDGE,"E8.0.23.0");var subQ1=sQuery(id+"F3.wireOp",EDGE,"E6.0.18.0");var subQ2=makeQuery(id+"F3.imprint","INTERSECT",VERTEX,{"derivedFrom":[subQ1,subQ0]});Q79=makeQuery(id+"F3.imprint","IMPRINT",FACE,{"disambiguationData":[TD([[makeQuery(id+"F3.imprint","IMPRINT",EDGE,{"disambiguationData":[TD([[subQ2,-1.0]])],"derivedFrom":subQ1}),-1.0]])]});}
            var Q80;
            {var subQ0=sQuery(id+"F3.wireOp",EDGE,"E8.0.24.0");var subQ1=sQuery(id+"F3.wireOp",EDGE,"E6.0.18.0");var subQ2=makeQuery(id+"F3.imprint","INTERSECT",VERTEX,{"derivedFrom":[subQ1,subQ0]});Q80=makeQuery(id+"F3.imprint","IMPRINT",FACE,{"disambiguationData":[TD([[makeQuery(id+"F3.imprint","IMPRINT",EDGE,{"disambiguationData":[TD([[subQ2,-1.0]])],"derivedFrom":subQ1}),-1.0]])]});}
            var Q81;
            {var subQ0=sQuery(id+"F3.wireOp",EDGE,"E8.0.23.0");var subQ1=sQuery(id+"F3.wireOp",EDGE,"E6.0.22.0");var subQ2=makeQuery(id+"F3.imprint","INTERSECT",VERTEX,{"derivedFrom":[subQ1,subQ0]});Q81=makeQuery(id+"F3.imprint","IMPRINT",FACE,{"disambiguationData":[TD([[makeQuery(id+"F3.imprint","IMPRINT",EDGE,{"disambiguationData":[TD([[subQ2,-1.0]])],"derivedFrom":subQ1}),-1.0]])]});}
            var Q82;
            {var subQ0=sQuery(id+"F3.wireOp",EDGE,"E8.0.23.0");var subQ1=sQuery(id+"F3.wireOp",EDGE,"E6.0.21.0");var subQ2=makeQuery(id+"F3.imprint","INTERSECT",VERTEX,{"derivedFrom":[subQ1,subQ0]});Q82=makeQuery(id+"F3.imprint","IMPRINT",FACE,{"disambiguationData":[TD([[makeQuery(id+"F3.imprint","IMPRINT",EDGE,{"disambiguationData":[TD([[subQ2,-1.0]])],"derivedFrom":subQ1}),-1.0]])]});}
            var Q83;
            {var subQ0=sQuery(id+"F3.wireOp",EDGE,"E8.0.23.0");var subQ1=sQuery(id+"F3.wireOp",EDGE,"E6.0.20.0");var subQ2=makeQuery(id+"F3.imprint","INTERSECT",VERTEX,{"derivedFrom":[subQ1,subQ0]});Q83=makeQuery(id+"F3.imprint","IMPRINT",FACE,{"disambiguationData":[TD([[makeQuery(id+"F3.imprint","IMPRINT",EDGE,{"disambiguationData":[TD([[subQ2,-1.0]])],"derivedFrom":subQ1}),-1.0]])]});}
            var Q84;
            {var subQ0=sQuery(id+"F3.wireOp",EDGE,"E8.0.22.0");var subQ1=sQuery(id+"F3.wireOp",EDGE,"E6.0.20.0");var subQ2=makeQuery(id+"F3.imprint","INTERSECT",VERTEX,{"derivedFrom":[subQ1,subQ0]});Q84=makeQuery(id+"F3.imprint","IMPRINT",FACE,{"disambiguationData":[TD([[makeQuery(id+"F3.imprint","IMPRINT",EDGE,{"disambiguationData":[TD([[subQ2,-1.0]])],"derivedFrom":subQ1}),-1.0]])]});}
            var Q85;
            {var subQ0=sQuery(id+"F3.wireOp",EDGE,"E8.0.21.0");var subQ1=sQuery(id+"F3.wireOp",EDGE,"E6.0.20.0");var subQ2=makeQuery(id+"F3.imprint","INTERSECT",VERTEX,{"derivedFrom":[subQ1,subQ0]});Q85=makeQuery(id+"F3.imprint","IMPRINT",FACE,{"disambiguationData":[TD([[makeQuery(id+"F3.imprint","IMPRINT",EDGE,{"disambiguationData":[TD([[subQ2,-1.0]])],"derivedFrom":subQ1}),-1.0]])]});}
            var Q86;
            {var subQ0=sQuery(id+"F3.wireOp",EDGE,"E8.0.21.0");var subQ1=sQuery(id+"F3.wireOp",EDGE,"E6.0.21.0");var subQ2=makeQuery(id+"F3.imprint","INTERSECT",VERTEX,{"derivedFrom":[subQ1,subQ0]});Q86=makeQuery(id+"F3.imprint","IMPRINT",FACE,{"disambiguationData":[TD([[makeQuery(id+"F3.imprint","IMPRINT",EDGE,{"disambiguationData":[TD([[subQ2,-1.0]])],"derivedFrom":subQ1}),-1.0]])]});}
            var Q87;
            {var subQ0=sQuery(id+"F3.wireOp",EDGE,"E8.0.21.0");var subQ1=sQuery(id+"F3.wireOp",EDGE,"E6.0.22.0");var subQ2=makeQuery(id+"F3.imprint","INTERSECT",VERTEX,{"derivedFrom":[subQ1,subQ0]});Q87=makeQuery(id+"F3.imprint","IMPRINT",FACE,{"disambiguationData":[TD([[makeQuery(id+"F3.imprint","IMPRINT",EDGE,{"disambiguationData":[TD([[subQ2,-1.0]])],"derivedFrom":subQ1}),-1.0]])]});}
            var Q88;
            {var subQ0=sQuery(id+"F3.wireOp",EDGE,"E8.0.22.0");var subQ1=sQuery(id+"F3.wireOp",EDGE,"E6.0.22.0");var subQ2=makeQuery(id+"F3.imprint","INTERSECT",VERTEX,{"derivedFrom":[subQ1,subQ0]});Q88=makeQuery(id+"F3.imprint","IMPRINT",FACE,{"disambiguationData":[TD([[makeQuery(id+"F3.imprint","IMPRINT",EDGE,{"disambiguationData":[TD([[subQ2,-1.0]])],"derivedFrom":subQ1}),-1.0]])]});}
            var Q89;
            {var subQ0=sQuery(id+"F3.wireOp",EDGE,"E8.0.22.0");var subQ1=sQuery(id+"F3.wireOp",EDGE,"E6.0.21.0");var subQ2=makeQuery(id+"F3.imprint","INTERSECT",VERTEX,{"derivedFrom":[subQ1,subQ0]});Q89=makeQuery(id+"F3.imprint","IMPRINT",FACE,{"disambiguationData":[TD([[makeQuery(id+"F3.imprint","IMPRINT",EDGE,{"disambiguationData":[TD([[subQ2,-1.0]])],"derivedFrom":subQ1}),-1.0]])]});}
            var Q90;
            {var subQ0=sQuery(id+"F3.wireOp",EDGE,"E8.0.24.0");var subQ1=sQuery(id+"F3.wireOp",EDGE,"E6.0.14.0");var subQ2=makeQuery(id+"F3.imprint","INTERSECT",VERTEX,{"derivedFrom":[subQ1,subQ0]});Q90=makeQuery(id+"F3.imprint","IMPRINT",FACE,{"disambiguationData":[TD([[makeQuery(id+"F3.imprint","IMPRINT",EDGE,{"disambiguationData":[TD([[subQ2,-1.0]])],"derivedFrom":subQ1}),-1.0]])]});}
            var Q91;
            {var subQ0=sQuery(id+"F3.wireOp",EDGE,"E8.0.24.0");var subQ1=sQuery(id+"F3.wireOp",EDGE,"E6.0.16.0");var subQ2=makeQuery(id+"F3.imprint","INTERSECT",VERTEX,{"derivedFrom":[subQ1,subQ0]});Q91=makeQuery(id+"F3.imprint","IMPRINT",FACE,{"disambiguationData":[TD([[makeQuery(id+"F3.imprint","IMPRINT",EDGE,{"disambiguationData":[TD([[subQ2,-1.0]])],"derivedFrom":subQ1}),-1.0]])]});}
            var Q92;
            {var subQ0=sQuery(id+"F3.wireOp",EDGE,"E8.0.22.0");var subQ1=sQuery(id+"F3.wireOp",EDGE,"E6.0.16.0");var subQ2=makeQuery(id+"F3.imprint","INTERSECT",VERTEX,{"derivedFrom":[subQ1,subQ0]});Q92=makeQuery(id+"F3.imprint","IMPRINT",FACE,{"disambiguationData":[TD([[makeQuery(id+"F3.imprint","IMPRINT",EDGE,{"disambiguationData":[TD([[subQ2,-1.0]])],"derivedFrom":subQ1}),-1.0]])]});}
            var Q93;
            {var subQ0=sQuery(id+"F3.wireOp",EDGE,"E8.0.22.0");var subQ1=sQuery(id+"F3.wireOp",EDGE,"E6.0.15.0");var subQ2=makeQuery(id+"F3.imprint","INTERSECT",VERTEX,{"derivedFrom":[subQ1,subQ0]});Q93=makeQuery(id+"F3.imprint","IMPRINT",FACE,{"disambiguationData":[TD([[makeQuery(id+"F3.imprint","IMPRINT",EDGE,{"disambiguationData":[TD([[subQ2,-1.0]])],"derivedFrom":subQ1}),-1.0]])]});}
            var Q94;
            {var subQ0=sQuery(id+"F3.wireOp",EDGE,"E8.0.22.0");var subQ1=sQuery(id+"F3.wireOp",EDGE,"E6.0.14.0");var subQ2=makeQuery(id+"F3.imprint","INTERSECT",VERTEX,{"derivedFrom":[subQ1,subQ0]});Q94=makeQuery(id+"F3.imprint","IMPRINT",FACE,{"disambiguationData":[TD([[makeQuery(id+"F3.imprint","IMPRINT",EDGE,{"disambiguationData":[TD([[subQ2,-1.0]])],"derivedFrom":subQ1}),-1.0]])]});}
            var Q95;
            {var subQ0=sQuery(id+"F3.wireOp",EDGE,"E8.0.24.0");var subQ1=sQuery(id+"F3.wireOp",EDGE,"E4.6.0.0");var subQ2=makeQuery(id+"F3.imprint","INTERSECT",VERTEX,{"derivedFrom":[subQ1,subQ0]});Q95=makeQuery(id+"F3.imprint","IMPRINT",FACE,{"disambiguationData":[TD([[makeQuery(id+"F3.imprint","IMPRINT",EDGE,{"disambiguationData":[TD([[subQ2,-1.0]])],"derivedFrom":subQ1}),-1.0]])]});}
            var Q96;
            {var subQ0=sQuery(id+"F3.wireOp",EDGE,"E8.0.23.0");var subQ1=sQuery(id+"F3.wireOp",EDGE,"E4.6.0.0");var subQ2=makeQuery(id+"F3.imprint","INTERSECT",VERTEX,{"derivedFrom":[subQ1,subQ0]});Q96=makeQuery(id+"F3.imprint","IMPRINT",FACE,{"disambiguationData":[TD([[makeQuery(id+"F3.imprint","IMPRINT",EDGE,{"disambiguationData":[TD([[subQ2,-1.0]])],"derivedFrom":subQ1}),-1.0]])]});}
            var Q97;
            {var subQ0=sQuery(id+"F3.wireOp",EDGE,"E8.0.22.0");var subQ1=sQuery(id+"F3.wireOp",EDGE,"E4.6.0.0");var subQ2=makeQuery(id+"F3.imprint","INTERSECT",VERTEX,{"derivedFrom":[subQ1,subQ0]});Q97=makeQuery(id+"F3.imprint","IMPRINT",FACE,{"disambiguationData":[TD([[makeQuery(id+"F3.imprint","IMPRINT",EDGE,{"disambiguationData":[TD([[subQ2,-1.0]])],"derivedFrom":subQ1}),-1.0]])]});}
            var Q98;
            {var subQ0=sQuery(id+"F3.wireOp",EDGE,"E8.0.21.0");var subQ1=sQuery(id+"F3.wireOp",EDGE,"E4.6.0.0");var subQ2=makeQuery(id+"F3.imprint","INTERSECT",VERTEX,{"derivedFrom":[subQ1,subQ0]});Q98=makeQuery(id+"F3.imprint","IMPRINT",FACE,{"disambiguationData":[TD([[makeQuery(id+"F3.imprint","IMPRINT",EDGE,{"disambiguationData":[TD([[subQ2,-1.0]])],"derivedFrom":subQ1}),-1.0]])]});}
            var Q99;
            {var subQ0=sQuery(id+"F3.wireOp",EDGE,"E8.0.20.0");var subQ1=sQuery(id+"F3.wireOp",EDGE,"E4.6.0.0");var subQ2=makeQuery(id+"F3.imprint","INTERSECT",VERTEX,{"derivedFrom":[subQ1,subQ0]});Q99=makeQuery(id+"F3.imprint","IMPRINT",FACE,{"disambiguationData":[TD([[makeQuery(id+"F3.imprint","IMPRINT",EDGE,{"disambiguationData":[TD([[subQ2,-1.0]])],"derivedFrom":subQ1}),-1.0]])]});}
            var Q100;
            {var subQ0=sQuery(id+"F3.wireOp",EDGE,"E8.0.19.0");var subQ1=sQuery(id+"F3.wireOp",EDGE,"E4.6.0.0");var subQ2=makeQuery(id+"F3.imprint","INTERSECT",VERTEX,{"derivedFrom":[subQ1,subQ0]});Q100=makeQuery(id+"F3.imprint","IMPRINT",FACE,{"disambiguationData":[TD([[makeQuery(id+"F3.imprint","IMPRINT",EDGE,{"disambiguationData":[TD([[subQ2,-1.0]])],"derivedFrom":subQ1}),-1.0]])]});}
            var Q101;
            {var subQ0=sQuery(id+"F3.wireOp",EDGE,"E8.0.19.0");var subQ1=sQuery(id+"F3.wireOp",EDGE,"E4.5.0.0");var subQ2=makeQuery(id+"F3.imprint","INTERSECT",VERTEX,{"derivedFrom":[subQ1,subQ0]});Q101=makeQuery(id+"F3.imprint","IMPRINT",FACE,{"disambiguationData":[TD([[makeQuery(id+"F3.imprint","IMPRINT",EDGE,{"disambiguationData":[TD([[subQ2,-1.0]])],"derivedFrom":subQ1}),-1.0]])]});}
            var Q102;
            {var subQ0=sQuery(id+"F3.wireOp",EDGE,"E8.0.19.0");var subQ1=sQuery(id+"F3.wireOp",EDGE,"E4.4.0.0");var subQ2=makeQuery(id+"F3.imprint","INTERSECT",VERTEX,{"derivedFrom":[subQ1,subQ0]});Q102=makeQuery(id+"F3.imprint","IMPRINT",FACE,{"disambiguationData":[TD([[makeQuery(id+"F3.imprint","IMPRINT",EDGE,{"disambiguationData":[TD([[subQ2,-1.0]])],"derivedFrom":subQ1}),-1.0]])]});}
            var Q103;
            {var subQ0=sQuery(id+"F3.wireOp",EDGE,"E8.0.19.0");var subQ1=sQuery(id+"F3.wireOp",EDGE,"E4.3.0.0");var subQ2=makeQuery(id+"F3.imprint","INTERSECT",VERTEX,{"derivedFrom":[subQ1,subQ0]});Q103=makeQuery(id+"F3.imprint","IMPRINT",FACE,{"disambiguationData":[TD([[makeQuery(id+"F3.imprint","IMPRINT",EDGE,{"disambiguationData":[TD([[subQ2,-1.0]])],"derivedFrom":subQ1}),-1.0]])]});}
            var Q104;
            {var subQ0=sQuery(id+"F3.wireOp",EDGE,"E8.0.19.0");var subQ1=sQuery(id+"F3.wireOp",EDGE,"E4.2.0.0");var subQ2=makeQuery(id+"F3.imprint","INTERSECT",VERTEX,{"derivedFrom":[subQ1,subQ0]});Q104=makeQuery(id+"F3.imprint","IMPRINT",FACE,{"disambiguationData":[TD([[makeQuery(id+"F3.imprint","IMPRINT",EDGE,{"disambiguationData":[TD([[subQ2,-1.0]])],"derivedFrom":subQ1}),-1.0]])]});}
            var Q105;
            {var subQ0=sQuery(id+"F3.wireOp",EDGE,"E8.0.19.0");var subQ1=sQuery(id+"F3.wireOp",EDGE,"E4.1.0.0");var subQ2=makeQuery(id+"F3.imprint","INTERSECT",VERTEX,{"derivedFrom":[subQ1,subQ0]});Q105=makeQuery(id+"F3.imprint","IMPRINT",FACE,{"disambiguationData":[TD([[makeQuery(id+"F3.imprint","IMPRINT",EDGE,{"disambiguationData":[TD([[subQ2,-1.0]])],"derivedFrom":subQ1}),-1.0]])]});}
            var Q106;
            {var subQ0=sQuery(id+"F3.wireOp",EDGE,"E8.0.21.0");var subQ1=sQuery(id+"F3.wireOp",EDGE,"E4.4.0.0");var subQ2=makeQuery(id+"F3.imprint","INTERSECT",VERTEX,{"derivedFrom":[subQ1,subQ0]});Q106=makeQuery(id+"F3.imprint","IMPRINT",FACE,{"disambiguationData":[TD([[makeQuery(id+"F3.imprint","IMPRINT",EDGE,{"disambiguationData":[TD([[subQ2,-1.0]])],"derivedFrom":subQ1}),-1.0]])]});}
            var Q107;
            {var subQ0=sQuery(id+"F3.wireOp",EDGE,"E8.0.22.0");var subQ1=sQuery(id+"F3.wireOp",EDGE,"E4.4.0.0");var subQ2=makeQuery(id+"F3.imprint","INTERSECT",VERTEX,{"derivedFrom":[subQ1,subQ0]});Q107=makeQuery(id+"F3.imprint","IMPRINT",FACE,{"disambiguationData":[TD([[makeQuery(id+"F3.imprint","IMPRINT",EDGE,{"disambiguationData":[TD([[subQ2,-1.0]])],"derivedFrom":subQ1}),-1.0]])]});}
            var Q108;
            {var subQ0=sQuery(id+"F3.wireOp",EDGE,"E8.0.23.0");var subQ1=sQuery(id+"F3.wireOp",EDGE,"E4.4.0.0");var subQ2=makeQuery(id+"F3.imprint","INTERSECT",VERTEX,{"derivedFrom":[subQ1,subQ0]});Q108=makeQuery(id+"F3.imprint","IMPRINT",FACE,{"disambiguationData":[TD([[makeQuery(id+"F3.imprint","IMPRINT",EDGE,{"disambiguationData":[TD([[subQ2,-1.0]])],"derivedFrom":subQ1}),-1.0]])]});}
            var Q109;
            {var subQ0=sQuery(id+"F3.wireOp",EDGE,"E8.0.23.0");var subQ1=sQuery(id+"F3.wireOp",EDGE,"E4.3.0.0");var subQ2=makeQuery(id+"F3.imprint","INTERSECT",VERTEX,{"derivedFrom":[subQ1,subQ0]});Q109=makeQuery(id+"F3.imprint","IMPRINT",FACE,{"disambiguationData":[TD([[makeQuery(id+"F3.imprint","IMPRINT",EDGE,{"disambiguationData":[TD([[subQ2,-1.0]])],"derivedFrom":subQ1}),-1.0]])]});}
            var Q110;
            {var subQ0=sQuery(id+"F3.wireOp",EDGE,"E8.0.22.0");var subQ1=sQuery(id+"F3.wireOp",EDGE,"E4.3.0.0");var subQ2=makeQuery(id+"F3.imprint","INTERSECT",VERTEX,{"derivedFrom":[subQ1,subQ0]});Q110=makeQuery(id+"F3.imprint","IMPRINT",FACE,{"disambiguationData":[TD([[makeQuery(id+"F3.imprint","IMPRINT",EDGE,{"disambiguationData":[TD([[subQ2,-1.0]])],"derivedFrom":subQ1}),-1.0]])]});}
            var Q111;
            {var subQ0=sQuery(id+"F3.wireOp",EDGE,"E8.0.21.0");var subQ1=sQuery(id+"F3.wireOp",EDGE,"E4.3.0.0");var subQ2=makeQuery(id+"F3.imprint","INTERSECT",VERTEX,{"derivedFrom":[subQ1,subQ0]});Q111=makeQuery(id+"F3.imprint","IMPRINT",FACE,{"disambiguationData":[TD([[makeQuery(id+"F3.imprint","IMPRINT",EDGE,{"disambiguationData":[TD([[subQ2,-1.0]])],"derivedFrom":subQ1}),-1.0]])]});}
            var Q112;
            {var subQ0=sQuery(id+"F3.wireOp",EDGE,"E8.0.21.0");var subQ1=sQuery(id+"F3.wireOp",EDGE,"E4.2.0.0");var subQ2=makeQuery(id+"F3.imprint","INTERSECT",VERTEX,{"derivedFrom":[subQ1,subQ0]});Q112=makeQuery(id+"F3.imprint","IMPRINT",FACE,{"disambiguationData":[TD([[makeQuery(id+"F3.imprint","IMPRINT",EDGE,{"disambiguationData":[TD([[subQ2,-1.0]])],"derivedFrom":subQ1}),-1.0]])]});}
            var Q113;
            {var subQ0=sQuery(id+"F3.wireOp",EDGE,"E8.0.22.0");var subQ1=sQuery(id+"F3.wireOp",EDGE,"E4.2.0.0");var subQ2=makeQuery(id+"F3.imprint","INTERSECT",VERTEX,{"derivedFrom":[subQ1,subQ0]});Q113=makeQuery(id+"F3.imprint","IMPRINT",FACE,{"disambiguationData":[TD([[makeQuery(id+"F3.imprint","IMPRINT",EDGE,{"disambiguationData":[TD([[subQ2,-1.0]])],"derivedFrom":subQ1}),-1.0]])]});}
            var Q114;
            {var subQ0=sQuery(id+"F3.wireOp",EDGE,"E8.0.23.0");var subQ1=sQuery(id+"F3.wireOp",EDGE,"E4.2.0.0");var subQ2=makeQuery(id+"F3.imprint","INTERSECT",VERTEX,{"derivedFrom":[subQ1,subQ0]});Q114=makeQuery(id+"F3.imprint","IMPRINT",FACE,{"disambiguationData":[TD([[makeQuery(id+"F3.imprint","IMPRINT",EDGE,{"disambiguationData":[TD([[subQ2,-1.0]])],"derivedFrom":subQ1}),-1.0]])]});}
            var Q115;
            {var subQ0=sQuery(id+"F3.wireOp",EDGE,"E8.0.21.0");var subQ1=sQuery(id+"F3.wireOp",EDGE,"E6.0.15.0");var subQ2=makeQuery(id+"F3.imprint","INTERSECT",VERTEX,{"derivedFrom":[subQ1,subQ0]});Q115=makeQuery(id+"F3.imprint","IMPRINT",FACE,{"disambiguationData":[TD([[makeQuery(id+"F3.imprint","IMPRINT",EDGE,{"disambiguationData":[TD([[subQ2,-1.0]])],"derivedFrom":subQ1}),-1.0]])]});}
            var Q116;
            {var subQ0=sQuery(id+"F3.wireOp",EDGE,"E8.0.20.0");var subQ1=sQuery(id+"F3.wireOp",EDGE,"E6.0.15.0");var subQ2=makeQuery(id+"F3.imprint","INTERSECT",VERTEX,{"derivedFrom":[subQ1,subQ0]});Q116=makeQuery(id+"F3.imprint","IMPRINT",FACE,{"disambiguationData":[TD([[makeQuery(id+"F3.imprint","IMPRINT",EDGE,{"disambiguationData":[TD([[subQ2,-1.0]])],"derivedFrom":subQ1}),-1.0]])]});}
            var Q117;
            {var subQ0=sQuery(id+"F3.wireOp",EDGE,"E8.0.20.0");var subQ1=sQuery(id+"F3.wireOp",EDGE,"E6.0.16.0");var subQ2=makeQuery(id+"F3.imprint","INTERSECT",VERTEX,{"derivedFrom":[subQ1,subQ0]});Q117=makeQuery(id+"F3.imprint","IMPRINT",FACE,{"disambiguationData":[TD([[makeQuery(id+"F3.imprint","IMPRINT",EDGE,{"disambiguationData":[TD([[subQ2,-1.0]])],"derivedFrom":subQ1}),-1.0]])]});}
            var Q118;
            {var subQ0=sQuery(id+"F3.wireOp",EDGE,"E8.0.19.0");var subQ1=sQuery(id+"F3.wireOp",EDGE,"E6.0.16.0");var subQ2=makeQuery(id+"F3.imprint","INTERSECT",VERTEX,{"derivedFrom":[subQ1,subQ0]});Q118=makeQuery(id+"F3.imprint","IMPRINT",FACE,{"disambiguationData":[TD([[makeQuery(id+"F3.imprint","IMPRINT",EDGE,{"disambiguationData":[TD([[subQ2,-1.0]])],"derivedFrom":subQ1}),-1.0]])]});}
            var Q119;
            {var subQ0=sQuery(id+"F3.wireOp",EDGE,"E8.0.25.0");var subQ1=sQuery(id+"F3.wireOp",EDGE,"E6.0.12.0");var subQ2=makeQuery(id+"F3.imprint","INTERSECT",VERTEX,{"derivedFrom":[subQ1,subQ0]});Q119=makeQuery(id+"F3.imprint","IMPRINT",FACE,{"disambiguationData":[TD([[makeQuery(id+"F3.imprint","IMPRINT",EDGE,{"disambiguationData":[TD([[subQ2,-1.0]])],"derivedFrom":subQ1}),-1.0]])]});}
            var Q120;
            {var subQ0=sQuery(id+"F3.wireOp",EDGE,"E8.0.25.0");var subQ1=sQuery(id+"F3.wireOp",EDGE,"E5.0.10.0");var subQ2=makeQuery(id+"F3.imprint","INTERSECT",VERTEX,{"derivedFrom":[subQ1,subQ0]});Q120=makeQuery(id+"F3.imprint","IMPRINT",FACE,{"disambiguationData":[TD([[makeQuery(id+"F3.imprint","IMPRINT",EDGE,{"disambiguationData":[TD([[subQ2,-1.0]])],"derivedFrom":subQ1}),-1.0]])]});}
            var Q121;
            {var subQ0=sQuery(id+"F3.wireOp",EDGE,"E8.0.25.0");var subQ1=sQuery(id+"F3.wireOp",EDGE,"E4.8.0.0");var subQ2=makeQuery(id+"F3.imprint","INTERSECT",VERTEX,{"derivedFrom":[subQ1,subQ0]});Q121=makeQuery(id+"F3.imprint","IMPRINT",FACE,{"disambiguationData":[TD([[makeQuery(id+"F3.imprint","IMPRINT",EDGE,{"disambiguationData":[TD([[subQ2,-1.0]])],"derivedFrom":subQ1}),-1.0]])]});}
            var Q122;
            {var subQ0=sQuery(id+"F3.wireOp",EDGE,"E8.0.24.0");var subQ1=sQuery(id+"F3.wireOp",EDGE,"E5.0.11.0");var subQ2=makeQuery(id+"F3.imprint","INTERSECT",VERTEX,{"derivedFrom":[subQ1,subQ0]});Q122=makeQuery(id+"F3.imprint","IMPRINT",FACE,{"disambiguationData":[TD([[makeQuery(id+"F3.imprint","IMPRINT",EDGE,{"disambiguationData":[TD([[subQ2,-1.0]])],"derivedFrom":subQ1}),-1.0]])]});}
            var Q123;
            {var subQ0=sQuery(id+"F3.wireOp",EDGE,"E8.0.24.0");var subQ1=sQuery(id+"F3.wireOp",EDGE,"E4.9.0.0");var subQ2=makeQuery(id+"F3.imprint","INTERSECT",VERTEX,{"derivedFrom":[subQ1,subQ0]});Q123=makeQuery(id+"F3.imprint","IMPRINT",FACE,{"disambiguationData":[TD([[makeQuery(id+"F3.imprint","IMPRINT",EDGE,{"disambiguationData":[TD([[subQ2,-1.0]])],"derivedFrom":subQ1}),-1.0]])]});}
            var Q124;
            {var subQ0=sQuery(id+"F3.wireOp",EDGE,"E8.0.23.0");var subQ1=sQuery(id+"F3.wireOp",EDGE,"E6.0.12.0");var subQ2=makeQuery(id+"F3.imprint","INTERSECT",VERTEX,{"derivedFrom":[subQ1,subQ0]});Q124=makeQuery(id+"F3.imprint","IMPRINT",FACE,{"disambiguationData":[TD([[makeQuery(id+"F3.imprint","IMPRINT",EDGE,{"disambiguationData":[TD([[subQ2,-1.0]])],"derivedFrom":subQ1}),-1.0]])]});}
            var Q125;
            {var subQ0=sQuery(id+"F3.wireOp",EDGE,"E8.0.22.0");var subQ1=sQuery(id+"F3.wireOp",EDGE,"E6.0.12.0");var subQ2=makeQuery(id+"F3.imprint","INTERSECT",VERTEX,{"derivedFrom":[subQ1,subQ0]});Q125=makeQuery(id+"F3.imprint","IMPRINT",FACE,{"disambiguationData":[TD([[makeQuery(id+"F3.imprint","IMPRINT",EDGE,{"disambiguationData":[TD([[subQ2,-1.0]])],"derivedFrom":subQ1}),-1.0]])]});}
            var Q126;
            {var subQ0=sQuery(id+"F3.wireOp",EDGE,"E8.0.22.0");var subQ1=sQuery(id+"F3.wireOp",EDGE,"E5.0.11.0");var subQ2=makeQuery(id+"F3.imprint","INTERSECT",VERTEX,{"derivedFrom":[subQ1,subQ0]});Q126=makeQuery(id+"F3.imprint","IMPRINT",FACE,{"disambiguationData":[TD([[makeQuery(id+"F3.imprint","IMPRINT",EDGE,{"disambiguationData":[TD([[subQ2,-1.0]])],"derivedFrom":subQ1}),-1.0]])]});}
            var Q127;
            {var subQ0=sQuery(id+"F3.wireOp",EDGE,"E8.0.22.0");var subQ1=sQuery(id+"F3.wireOp",EDGE,"E5.0.10.0");var subQ2=makeQuery(id+"F3.imprint","INTERSECT",VERTEX,{"derivedFrom":[subQ1,subQ0]});Q127=makeQuery(id+"F3.imprint","IMPRINT",FACE,{"disambiguationData":[TD([[makeQuery(id+"F3.imprint","IMPRINT",EDGE,{"disambiguationData":[TD([[subQ2,-1.0]])],"derivedFrom":subQ1}),-1.0]])]});}
            var Q128;
            {var subQ0=sQuery(id+"F3.wireOp",EDGE,"E8.0.23.0");var subQ1=sQuery(id+"F3.wireOp",EDGE,"E5.0.10.0");var subQ2=makeQuery(id+"F3.imprint","INTERSECT",VERTEX,{"derivedFrom":[subQ1,subQ0]});Q128=makeQuery(id+"F3.imprint","IMPRINT",FACE,{"disambiguationData":[TD([[makeQuery(id+"F3.imprint","IMPRINT",EDGE,{"disambiguationData":[TD([[subQ2,-1.0]])],"derivedFrom":subQ1}),-1.0]])]});}
            var Q129;
            {var subQ0=sQuery(id+"F3.wireOp",EDGE,"E8.0.22.0");var subQ1=sQuery(id+"F3.wireOp",EDGE,"E4.9.0.0");var subQ2=makeQuery(id+"F3.imprint","INTERSECT",VERTEX,{"derivedFrom":[subQ1,subQ0]});Q129=makeQuery(id+"F3.imprint","IMPRINT",FACE,{"disambiguationData":[TD([[makeQuery(id+"F3.imprint","IMPRINT",EDGE,{"disambiguationData":[TD([[subQ2,-1.0]])],"derivedFrom":subQ1}),-1.0]])]});}
            var Q130;
            {var subQ0=sQuery(id+"F3.wireOp",EDGE,"E8.0.22.0");var subQ1=sQuery(id+"F3.wireOp",EDGE,"E4.8.0.0");var subQ2=makeQuery(id+"F3.imprint","INTERSECT",VERTEX,{"derivedFrom":[subQ1,subQ0]});Q130=makeQuery(id+"F3.imprint","IMPRINT",FACE,{"disambiguationData":[TD([[makeQuery(id+"F3.imprint","IMPRINT",EDGE,{"disambiguationData":[TD([[subQ2,-1.0]])],"derivedFrom":subQ1}),-1.0]])]});}
            var Q131;
            {var subQ0=sQuery(id+"F3.wireOp",EDGE,"E8.0.21.0");var subQ1=sQuery(id+"F3.wireOp",EDGE,"E4.8.0.0");var subQ2=makeQuery(id+"F3.imprint","INTERSECT",VERTEX,{"derivedFrom":[subQ1,subQ0]});Q131=makeQuery(id+"F3.imprint","IMPRINT",FACE,{"disambiguationData":[TD([[makeQuery(id+"F3.imprint","IMPRINT",EDGE,{"disambiguationData":[TD([[subQ2,-1.0]])],"derivedFrom":subQ1}),-1.0]])]});}
            var Q132;
            {var subQ0=sQuery(id+"F3.wireOp",EDGE,"E8.0.20.0");var subQ1=sQuery(id+"F3.wireOp",EDGE,"E4.8.0.0");var subQ2=makeQuery(id+"F3.imprint","INTERSECT",VERTEX,{"derivedFrom":[subQ1,subQ0]});Q132=makeQuery(id+"F3.imprint","IMPRINT",FACE,{"disambiguationData":[TD([[makeQuery(id+"F3.imprint","IMPRINT",EDGE,{"disambiguationData":[TD([[subQ2,-1.0]])],"derivedFrom":subQ1}),-1.0]])]});}
            var Q133;
            {var subQ0=sQuery(id+"F3.wireOp",EDGE,"E8.0.19.0");var subQ1=sQuery(id+"F3.wireOp",EDGE,"E4.8.0.0");var subQ2=makeQuery(id+"F3.imprint","INTERSECT",VERTEX,{"derivedFrom":[subQ1,subQ0]});Q133=makeQuery(id+"F3.imprint","IMPRINT",FACE,{"disambiguationData":[TD([[makeQuery(id+"F3.imprint","IMPRINT",EDGE,{"disambiguationData":[TD([[subQ2,-1.0]])],"derivedFrom":subQ1}),-1.0]])]});}
            var Q134;
            {var subQ0=sQuery(id+"F3.wireOp",EDGE,"E8.0.20.0");var subQ1=sQuery(id+"F3.wireOp",EDGE,"E4.9.0.0");var subQ2=makeQuery(id+"F3.imprint","INTERSECT",VERTEX,{"derivedFrom":[subQ1,subQ0]});Q134=makeQuery(id+"F3.imprint","IMPRINT",FACE,{"disambiguationData":[TD([[makeQuery(id+"F3.imprint","IMPRINT",EDGE,{"disambiguationData":[TD([[subQ2,-1.0]])],"derivedFrom":subQ1}),-1.0]])]});}
            var Q135;
            {var subQ0=sQuery(id+"F3.wireOp",EDGE,"E8.0.20.0");var subQ1=sQuery(id+"F3.wireOp",EDGE,"E6.0.13.0");var subQ2=makeQuery(id+"F3.imprint","INTERSECT",VERTEX,{"derivedFrom":[subQ1,subQ0]});Q135=makeQuery(id+"F3.imprint","IMPRINT",FACE,{"disambiguationData":[TD([[makeQuery(id+"F3.imprint","IMPRINT",EDGE,{"disambiguationData":[TD([[subQ2,-1.0]])],"derivedFrom":subQ1}),-1.0]])]});}
            var Q136;
            {var subQ0=sQuery(id+"F3.wireOp",EDGE,"E8.0.20.0");var subQ1=sQuery(id+"F3.wireOp",EDGE,"E6.0.12.0");var subQ2=makeQuery(id+"F3.imprint","INTERSECT",VERTEX,{"derivedFrom":[subQ1,subQ0]});Q136=makeQuery(id+"F3.imprint","IMPRINT",FACE,{"disambiguationData":[TD([[makeQuery(id+"F3.imprint","IMPRINT",EDGE,{"disambiguationData":[TD([[subQ2,-1.0]])],"derivedFrom":subQ1}),-1.0]])]});}
            var Q137;
            {var subQ0=sQuery(id+"F3.wireOp",EDGE,"E8.0.20.0");var subQ1=sQuery(id+"F3.wireOp",EDGE,"E5.0.11.0");var subQ2=makeQuery(id+"F3.imprint","INTERSECT",VERTEX,{"derivedFrom":[subQ1,subQ0]});Q137=makeQuery(id+"F3.imprint","IMPRINT",FACE,{"disambiguationData":[TD([[makeQuery(id+"F3.imprint","IMPRINT",EDGE,{"disambiguationData":[TD([[subQ2,-1.0]])],"derivedFrom":subQ1}),-1.0]])]});}
            var Q138;
            {var subQ0=sQuery(id+"F3.wireOp",EDGE,"E8.0.19.0");var subQ1=sQuery(id+"F3.wireOp",EDGE,"E6.0.12.0");var subQ2=makeQuery(id+"F3.imprint","INTERSECT",VERTEX,{"derivedFrom":[subQ1,subQ0]});Q138=makeQuery(id+"F3.imprint","IMPRINT",FACE,{"disambiguationData":[TD([[makeQuery(id+"F3.imprint","IMPRINT",EDGE,{"disambiguationData":[TD([[subQ2,-1.0]])],"derivedFrom":subQ1}),-1.0]])]});}
            var Q139;
            {var subQ0=sQuery(id+"F3.wireOp",EDGE,"E8.0.19.0");var subQ1=sQuery(id+"F3.wireOp",EDGE,"E5.0.10.0");var subQ2=makeQuery(id+"F3.imprint","INTERSECT",VERTEX,{"derivedFrom":[subQ1,subQ0]});Q139=makeQuery(id+"F3.imprint","IMPRINT",FACE,{"disambiguationData":[TD([[makeQuery(id+"F3.imprint","IMPRINT",EDGE,{"disambiguationData":[TD([[subQ2,-1.0]])],"derivedFrom":subQ1}),-1.0]])]});}
            var Q140;
            {var subQ0=sQuery(id+"F3.wireOp",EDGE,"E8.0.18.0");var subQ1=sQuery(id+"F3.wireOp",EDGE,"E5.0.10.0");var subQ2=makeQuery(id+"F3.imprint","INTERSECT",VERTEX,{"derivedFrom":[subQ1,subQ0]});Q140=makeQuery(id+"F3.imprint","IMPRINT",FACE,{"disambiguationData":[TD([[makeQuery(id+"F3.imprint","IMPRINT",EDGE,{"disambiguationData":[TD([[subQ2,-1.0]])],"derivedFrom":subQ1}),-1.0]])]});}
            var Q141;
            {var subQ0=sQuery(id+"F3.wireOp",EDGE,"E8.0.17.0");var subQ1=sQuery(id+"F3.wireOp",EDGE,"E5.0.10.0");var subQ2=makeQuery(id+"F3.imprint","INTERSECT",VERTEX,{"derivedFrom":[subQ1,subQ0]});Q141=makeQuery(id+"F3.imprint","IMPRINT",FACE,{"disambiguationData":[TD([[makeQuery(id+"F3.imprint","IMPRINT",EDGE,{"disambiguationData":[TD([[subQ2,-1.0]])],"derivedFrom":subQ1}),-1.0]])]});}
            var Q142;
            {var subQ0=sQuery(id+"F3.wireOp",EDGE,"E8.0.18.0");var subQ1=sQuery(id+"F3.wireOp",EDGE,"E4.9.0.0");var subQ2=makeQuery(id+"F3.imprint","INTERSECT",VERTEX,{"derivedFrom":[subQ1,subQ0]});Q142=makeQuery(id+"F3.imprint","IMPRINT",FACE,{"disambiguationData":[TD([[makeQuery(id+"F3.imprint","IMPRINT",EDGE,{"disambiguationData":[TD([[subQ2,-1.0]])],"derivedFrom":subQ1}),-1.0]])]});}
            var Q143;
            {var subQ0=sQuery(id+"F3.wireOp",EDGE,"E8.0.16.0");var subQ1=sQuery(id+"F3.wireOp",EDGE,"E5.0.11.0");var subQ2=makeQuery(id+"F3.imprint","INTERSECT",VERTEX,{"derivedFrom":[subQ1,subQ0]});Q143=makeQuery(id+"F3.imprint","IMPRINT",FACE,{"disambiguationData":[TD([[makeQuery(id+"F3.imprint","IMPRINT",EDGE,{"disambiguationData":[TD([[subQ2,-1.0]])],"derivedFrom":subQ1}),-1.0]])]});}
            var Q144;
            {var subQ0=sQuery(id+"F3.wireOp",EDGE,"E8.0.17.0");var subQ1=sQuery(id+"F3.wireOp",EDGE,"E5.0.11.0");var subQ2=makeQuery(id+"F3.imprint","INTERSECT",VERTEX,{"derivedFrom":[subQ1,subQ0]});Q144=makeQuery(id+"F3.imprint","IMPRINT",FACE,{"disambiguationData":[TD([[makeQuery(id+"F3.imprint","IMPRINT",EDGE,{"disambiguationData":[TD([[subQ2,-1.0]])],"derivedFrom":subQ1}),-1.0]])]});}
            var Q145;
            {var subQ0=sQuery(id+"F3.wireOp",EDGE,"E8.0.17.0");var subQ1=sQuery(id+"F3.wireOp",EDGE,"E6.0.12.0");var subQ2=makeQuery(id+"F3.imprint","INTERSECT",VERTEX,{"derivedFrom":[subQ1,subQ0]});Q145=makeQuery(id+"F3.imprint","IMPRINT",FACE,{"disambiguationData":[TD([[makeQuery(id+"F3.imprint","IMPRINT",EDGE,{"disambiguationData":[TD([[subQ2,-1.0]])],"derivedFrom":subQ1}),-1.0]])]});}
            var Q146;
            {var subQ0=sQuery(id+"F3.wireOp",EDGE,"E8.0.16.0");var subQ1=sQuery(id+"F3.wireOp",EDGE,"E6.0.12.0");var subQ2=makeQuery(id+"F3.imprint","INTERSECT",VERTEX,{"derivedFrom":[subQ1,subQ0]});Q146=makeQuery(id+"F3.imprint","IMPRINT",FACE,{"disambiguationData":[TD([[makeQuery(id+"F3.imprint","IMPRINT",EDGE,{"disambiguationData":[TD([[subQ2,-1.0]])],"derivedFrom":subQ1}),-1.0]])]});}
            var Q147;
            {var subQ0=sQuery(id+"F3.wireOp",EDGE,"E8.0.18.0");var subQ1=sQuery(id+"F3.wireOp",EDGE,"E6.0.13.0");var subQ2=makeQuery(id+"F3.imprint","INTERSECT",VERTEX,{"derivedFrom":[subQ1,subQ0]});Q147=makeQuery(id+"F3.imprint","IMPRINT",FACE,{"disambiguationData":[TD([[makeQuery(id+"F3.imprint","IMPRINT",EDGE,{"disambiguationData":[TD([[subQ2,-1.0]])],"derivedFrom":subQ1}),-1.0]])]});}
            var Q148;
            {var subQ0=sQuery(id+"F3.wireOp",EDGE,"E8.0.18.0");var subQ1=sQuery(id+"F3.wireOp",EDGE,"E6.0.14.0");var subQ2=makeQuery(id+"F3.imprint","INTERSECT",VERTEX,{"derivedFrom":[subQ1,subQ0]});Q148=makeQuery(id+"F3.imprint","IMPRINT",FACE,{"disambiguationData":[TD([[makeQuery(id+"F3.imprint","IMPRINT",EDGE,{"disambiguationData":[TD([[subQ2,-1.0]])],"derivedFrom":subQ1}),-1.0]])]});}
            var Q149;
            {var subQ0=sQuery(id+"F3.wireOp",EDGE,"E8.0.19.0");var subQ1=sQuery(id+"F3.wireOp",EDGE,"E6.0.14.0");var subQ2=makeQuery(id+"F3.imprint","INTERSECT",VERTEX,{"derivedFrom":[subQ1,subQ0]});Q149=makeQuery(id+"F3.imprint","IMPRINT",FACE,{"disambiguationData":[TD([[makeQuery(id+"F3.imprint","IMPRINT",EDGE,{"disambiguationData":[TD([[subQ2,-1.0]])],"derivedFrom":subQ1}),-1.0]])]});}
            var Q150;
            {var subQ0=sQuery(id+"F3.wireOp",EDGE,"E8.0.18.0");var subQ1=sQuery(id+"F3.wireOp",EDGE,"E6.0.15.0");var subQ2=makeQuery(id+"F3.imprint","INTERSECT",VERTEX,{"derivedFrom":[subQ1,subQ0]});Q150=makeQuery(id+"F3.imprint","IMPRINT",FACE,{"disambiguationData":[TD([[makeQuery(id+"F3.imprint","IMPRINT",EDGE,{"disambiguationData":[TD([[subQ2,-1.0]])],"derivedFrom":subQ1}),-1.0]])]});}
            var Q151;
            {var subQ0=sQuery(id+"F3.wireOp",EDGE,"E8.0.17.0");var subQ1=sQuery(id+"F3.wireOp",EDGE,"E6.0.15.0");var subQ2=makeQuery(id+"F3.imprint","INTERSECT",VERTEX,{"derivedFrom":[subQ1,subQ0]});Q151=makeQuery(id+"F3.imprint","IMPRINT",FACE,{"disambiguationData":[TD([[makeQuery(id+"F3.imprint","IMPRINT",EDGE,{"disambiguationData":[TD([[subQ2,-1.0]])],"derivedFrom":subQ1}),-1.0]])]});}
            var Q152;
            {var subQ0=sQuery(id+"F3.wireOp",EDGE,"E8.0.17.0");var subQ1=sQuery(id+"F3.wireOp",EDGE,"E6.0.16.0");var subQ2=makeQuery(id+"F3.imprint","INTERSECT",VERTEX,{"derivedFrom":[subQ1,subQ0]});Q152=makeQuery(id+"F3.imprint","IMPRINT",FACE,{"disambiguationData":[TD([[makeQuery(id+"F3.imprint","IMPRINT",EDGE,{"disambiguationData":[TD([[subQ2,-1.0]])],"derivedFrom":subQ1}),-1.0]])]});}
            var Q153;
            {var subQ0=sQuery(id+"F3.wireOp",EDGE,"E8.0.17.0");var subQ1=sQuery(id+"F3.wireOp",EDGE,"E6.0.17.0");var subQ2=makeQuery(id+"F3.imprint","INTERSECT",VERTEX,{"derivedFrom":[subQ1,subQ0]});Q153=makeQuery(id+"F3.imprint","IMPRINT",FACE,{"disambiguationData":[TD([[makeQuery(id+"F3.imprint","IMPRINT",EDGE,{"disambiguationData":[TD([[subQ2,-1.0]])],"derivedFrom":subQ1}),-1.0]])]});}
            var Q154;
            {var subQ0=sQuery(id+"F3.wireOp",EDGE,"E8.0.17.0");var subQ1=sQuery(id+"F3.wireOp",EDGE,"E6.0.18.0");var subQ2=makeQuery(id+"F3.imprint","INTERSECT",VERTEX,{"derivedFrom":[subQ1,subQ0]});Q154=makeQuery(id+"F3.imprint","IMPRINT",FACE,{"disambiguationData":[TD([[makeQuery(id+"F3.imprint","IMPRINT",EDGE,{"disambiguationData":[TD([[subQ2,-1.0]])],"derivedFrom":subQ1}),-1.0]])]});}
            var Q155;
            {var subQ0=sQuery(id+"F3.wireOp",EDGE,"E8.0.16.0");var subQ1=sQuery(id+"F3.wireOp",EDGE,"E6.0.16.0");var subQ2=makeQuery(id+"F3.imprint","INTERSECT",VERTEX,{"derivedFrom":[subQ1,subQ0]});Q155=makeQuery(id+"F3.imprint","IMPRINT",FACE,{"disambiguationData":[TD([[makeQuery(id+"F3.imprint","IMPRINT",EDGE,{"disambiguationData":[TD([[subQ2,-1.0]])],"derivedFrom":subQ1}),-1.0]])]});}
            var Q156;
            {var subQ0=sQuery(id+"F3.wireOp",EDGE,"E8.0.15.0");var subQ1=sQuery(id+"F3.wireOp",EDGE,"E6.0.16.0");var subQ2=makeQuery(id+"F3.imprint","INTERSECT",VERTEX,{"derivedFrom":[subQ1,subQ0]});Q156=makeQuery(id+"F3.imprint","IMPRINT",FACE,{"disambiguationData":[TD([[makeQuery(id+"F3.imprint","IMPRINT",EDGE,{"disambiguationData":[TD([[subQ2,-1.0]])],"derivedFrom":subQ1}),-1.0]])]});}
            var Q157;
            {var subQ0=sQuery(id+"F3.wireOp",EDGE,"E8.0.14.0");var subQ1=sQuery(id+"F3.wireOp",EDGE,"E6.0.16.0");var subQ2=makeQuery(id+"F3.imprint","INTERSECT",VERTEX,{"derivedFrom":[subQ1,subQ0]});Q157=makeQuery(id+"F3.imprint","IMPRINT",FACE,{"disambiguationData":[TD([[makeQuery(id+"F3.imprint","IMPRINT",EDGE,{"disambiguationData":[TD([[subQ2,-1.0]])],"derivedFrom":subQ1}),-1.0]])]});}
            var Q158;
            {var subQ0=sQuery(id+"F3.wireOp",EDGE,"E8.0.15.0");var subQ1=sQuery(id+"F3.wireOp",EDGE,"E6.0.17.0");var subQ2=makeQuery(id+"F3.imprint","INTERSECT",VERTEX,{"derivedFrom":[subQ1,subQ0]});Q158=makeQuery(id+"F3.imprint","IMPRINT",FACE,{"disambiguationData":[TD([[makeQuery(id+"F3.imprint","IMPRINT",EDGE,{"disambiguationData":[TD([[subQ2,-1.0]])],"derivedFrom":subQ1}),-1.0]])]});}
            var Q159;
            {var subQ0=sQuery(id+"F3.wireOp",EDGE,"E8.0.15.0");var subQ1=sQuery(id+"F3.wireOp",EDGE,"E6.0.18.0");var subQ2=makeQuery(id+"F3.imprint","INTERSECT",VERTEX,{"derivedFrom":[subQ1,subQ0]});Q159=makeQuery(id+"F3.imprint","IMPRINT",FACE,{"disambiguationData":[TD([[makeQuery(id+"F3.imprint","IMPRINT",EDGE,{"disambiguationData":[TD([[subQ2,-1.0]])],"derivedFrom":subQ1}),-1.0]])]});}
            var Q160;
            {var subQ0=sQuery(id+"F3.wireOp",EDGE,"E8.0.15.0");var subQ1=sQuery(id+"F3.wireOp",EDGE,"E6.0.14.0");var subQ2=makeQuery(id+"F3.imprint","INTERSECT",VERTEX,{"derivedFrom":[subQ1,subQ0]});Q160=makeQuery(id+"F3.imprint","IMPRINT",FACE,{"disambiguationData":[TD([[makeQuery(id+"F3.imprint","IMPRINT",EDGE,{"disambiguationData":[TD([[subQ2,-1.0]])],"derivedFrom":subQ1}),-1.0]])]});}
            var Q161;
            {var subQ0=sQuery(id+"F3.wireOp",EDGE,"E8.0.16.0");var subQ1=sQuery(id+"F3.wireOp",EDGE,"E6.0.14.0");var subQ2=makeQuery(id+"F3.imprint","INTERSECT",VERTEX,{"derivedFrom":[subQ1,subQ0]});Q161=makeQuery(id+"F3.imprint","IMPRINT",FACE,{"disambiguationData":[TD([[makeQuery(id+"F3.imprint","IMPRINT",EDGE,{"disambiguationData":[TD([[subQ2,-1.0]])],"derivedFrom":subQ1}),-1.0]])]});}
            var Q162;
            {var subQ0=sQuery(id+"F3.wireOp",EDGE,"E8.0.17.0");var subQ1=sQuery(id+"F3.wireOp",EDGE,"E6.0.13.0");var subQ2=makeQuery(id+"F3.imprint","INTERSECT",VERTEX,{"derivedFrom":[subQ1,subQ0]});Q162=makeQuery(id+"F3.imprint","IMPRINT",FACE,{"disambiguationData":[TD([[makeQuery(id+"F3.imprint","IMPRINT",EDGE,{"disambiguationData":[TD([[subQ2,-1.0]])],"derivedFrom":subQ1}),-1.0]])]});}
            var Q163;
            {var subQ0=sQuery(id+"F3.wireOp",EDGE,"E8.0.12.0");var subQ1=sQuery(id+"F3.wireOp",EDGE,"E6.0.23.0");var subQ2=makeQuery(id+"F3.imprint","INTERSECT",VERTEX,{"derivedFrom":[subQ1,subQ0]});Q163=makeQuery(id+"F3.imprint","IMPRINT",FACE,{"disambiguationData":[TD([[makeQuery(id+"F3.imprint","IMPRINT",EDGE,{"disambiguationData":[TD([[subQ2,-1.0]])],"derivedFrom":subQ1}),-1.0]])]});}
            var Q164;
            {var subQ0=sQuery(id+"F3.wireOp",EDGE,"E8.0.13.0");var subQ1=sQuery(id+"F3.wireOp",EDGE,"E6.0.23.0");var subQ2=makeQuery(id+"F3.imprint","INTERSECT",VERTEX,{"derivedFrom":[subQ1,subQ0]});Q164=makeQuery(id+"F3.imprint","IMPRINT",FACE,{"disambiguationData":[TD([[makeQuery(id+"F3.imprint","IMPRINT",EDGE,{"disambiguationData":[TD([[subQ2,-1.0]])],"derivedFrom":subQ1}),-1.0]])]});}
            var Q165;
            {var subQ0=sQuery(id+"F3.wireOp",EDGE,"E8.0.14.0");var subQ1=sQuery(id+"F3.wireOp",EDGE,"E6.0.23.0");var subQ2=makeQuery(id+"F3.imprint","INTERSECT",VERTEX,{"derivedFrom":[subQ1,subQ0]});Q165=makeQuery(id+"F3.imprint","IMPRINT",FACE,{"disambiguationData":[TD([[makeQuery(id+"F3.imprint","IMPRINT",EDGE,{"disambiguationData":[TD([[subQ2,-1.0]])],"derivedFrom":subQ1}),-1.0]])]});}
            var Q166;
            {var subQ0=sQuery(id+"F3.wireOp",EDGE,"E8.0.13.0");var subQ1=sQuery(id+"F3.wireOp",EDGE,"E6.0.22.0");var subQ2=makeQuery(id+"F3.imprint","INTERSECT",VERTEX,{"derivedFrom":[subQ1,subQ0]});Q166=makeQuery(id+"F3.imprint","IMPRINT",FACE,{"disambiguationData":[TD([[makeQuery(id+"F3.imprint","IMPRINT",EDGE,{"disambiguationData":[TD([[subQ2,-1.0]])],"derivedFrom":subQ1}),-1.0]])]});}
            var Q167;
            {var subQ0=sQuery(id+"F3.wireOp",EDGE,"E8.0.14.0");var subQ1=sQuery(id+"F3.wireOp",EDGE,"E6.0.22.0");var subQ2=makeQuery(id+"F3.imprint","INTERSECT",VERTEX,{"derivedFrom":[subQ1,subQ0]});Q167=makeQuery(id+"F3.imprint","IMPRINT",FACE,{"disambiguationData":[TD([[makeQuery(id+"F3.imprint","IMPRINT",EDGE,{"disambiguationData":[TD([[subQ2,-1.0]])],"derivedFrom":subQ1}),-1.0]])]});}
            var Q168;
            {var subQ0=sQuery(id+"F3.wireOp",EDGE,"E8.0.14.0");var subQ1=sQuery(id+"F3.wireOp",EDGE,"E6.0.21.0");var subQ2=makeQuery(id+"F3.imprint","INTERSECT",VERTEX,{"derivedFrom":[subQ1,subQ0]});Q168=makeQuery(id+"F3.imprint","IMPRINT",FACE,{"disambiguationData":[TD([[makeQuery(id+"F3.imprint","IMPRINT",EDGE,{"disambiguationData":[TD([[subQ2,-1.0]])],"derivedFrom":subQ1}),-1.0]])]});}
            var Q169;
            {var subQ0=sQuery(id+"F3.wireOp",EDGE,"E8.0.16.0");var subQ1=sQuery(id+"F3.wireOp",EDGE,"E6.0.19.0");var subQ2=makeQuery(id+"F3.imprint","INTERSECT",VERTEX,{"derivedFrom":[subQ1,subQ0]});Q169=makeQuery(id+"F3.imprint","IMPRINT",FACE,{"disambiguationData":[TD([[makeQuery(id+"F3.imprint","IMPRINT",EDGE,{"disambiguationData":[TD([[subQ2,-1.0]])],"derivedFrom":subQ1}),-1.0]])]});}
            var Q170;
            {var subQ0=sQuery(id+"F3.wireOp",EDGE,"E8.0.16.0");var subQ1=sQuery(id+"F3.wireOp",EDGE,"E6.0.20.0");var subQ2=makeQuery(id+"F3.imprint","INTERSECT",VERTEX,{"derivedFrom":[subQ1,subQ0]});Q170=makeQuery(id+"F3.imprint","IMPRINT",FACE,{"disambiguationData":[TD([[makeQuery(id+"F3.imprint","IMPRINT",EDGE,{"disambiguationData":[TD([[subQ2,-1.0]])],"derivedFrom":subQ1}),-1.0]])]});}
            var Q171;
            {var subQ0=sQuery(id+"F3.wireOp",EDGE,"E8.0.16.0");var subQ1=sQuery(id+"F3.wireOp",EDGE,"E6.0.21.0");var subQ2=makeQuery(id+"F3.imprint","INTERSECT",VERTEX,{"derivedFrom":[subQ1,subQ0]});Q171=makeQuery(id+"F3.imprint","IMPRINT",FACE,{"disambiguationData":[TD([[makeQuery(id+"F3.imprint","IMPRINT",EDGE,{"disambiguationData":[TD([[subQ2,-1.0]])],"derivedFrom":subQ1}),-1.0]])]});}
            var Q172;
            {var subQ0=sQuery(id+"F3.wireOp",EDGE,"E8.0.17.0");var subQ1=sQuery(id+"F3.wireOp",EDGE,"E6.0.20.0");var subQ2=makeQuery(id+"F3.imprint","INTERSECT",VERTEX,{"derivedFrom":[subQ1,subQ0]});Q172=makeQuery(id+"F3.imprint","IMPRINT",FACE,{"disambiguationData":[TD([[makeQuery(id+"F3.imprint","IMPRINT",EDGE,{"disambiguationData":[TD([[subQ2,-1.0]])],"derivedFrom":subQ1}),-1.0]])]});}
            var Q173;
            {var subQ0=sQuery(id+"F3.wireOp",EDGE,"E8.0.16.0");var subQ1=sQuery(id+"F3.wireOp",EDGE,"E6.0.23.0");var subQ2=makeQuery(id+"F3.imprint","INTERSECT",VERTEX,{"derivedFrom":[subQ1,subQ0]});Q173=makeQuery(id+"F3.imprint","IMPRINT",FACE,{"disambiguationData":[TD([[makeQuery(id+"F3.imprint","IMPRINT",EDGE,{"disambiguationData":[TD([[subQ2,-1.0]])],"derivedFrom":subQ1}),-1.0]])]});}
            var Q174;
            {var subQ0=sQuery(id+"F3.wireOp",EDGE,"E8.0.17.0");var subQ1=sQuery(id+"F3.wireOp",EDGE,"E6.0.23.0");var subQ2=makeQuery(id+"F3.imprint","INTERSECT",VERTEX,{"derivedFrom":[subQ1,subQ0]});Q174=makeQuery(id+"F3.imprint","IMPRINT",FACE,{"disambiguationData":[TD([[makeQuery(id+"F3.imprint","IMPRINT",EDGE,{"disambiguationData":[TD([[subQ2,-1.0]])],"derivedFrom":subQ1}),-1.0]])]});}
            var Q175;
            {var subQ0=sQuery(id+"F3.wireOp",EDGE,"E8.0.17.0");var subQ1=sQuery(id+"F3.wireOp",EDGE,"E6.0.22.0");var subQ2=makeQuery(id+"F3.imprint","INTERSECT",VERTEX,{"derivedFrom":[subQ1,subQ0]});Q175=makeQuery(id+"F3.imprint","IMPRINT",FACE,{"disambiguationData":[TD([[makeQuery(id+"F3.imprint","IMPRINT",EDGE,{"disambiguationData":[TD([[subQ2,-1.0]])],"derivedFrom":subQ1}),-1.0]])]});}
            var Q176;
            {var subQ0=sQuery(id+"F3.wireOp",EDGE,"E8.0.17.0");var subQ1=sQuery(id+"F3.wireOp",EDGE,"E6.0.21.0");var subQ2=makeQuery(id+"F3.imprint","INTERSECT",VERTEX,{"derivedFrom":[subQ1,subQ0]});Q176=makeQuery(id+"F3.imprint","IMPRINT",FACE,{"disambiguationData":[TD([[makeQuery(id+"F3.imprint","IMPRINT",EDGE,{"disambiguationData":[TD([[subQ2,-1.0]])],"derivedFrom":subQ1}),-1.0]])]});}
            var Q177;
            {var subQ0=sQuery(id+"F3.wireOp",EDGE,"E8.0.15.0");var subQ1=sQuery(id+"F3.wireOp",EDGE,"E6.0.21.0");var subQ2=makeQuery(id+"F3.imprint","INTERSECT",VERTEX,{"derivedFrom":[subQ1,subQ0]});Q177=makeQuery(id+"F3.imprint","IMPRINT",FACE,{"disambiguationData":[TD([[makeQuery(id+"F3.imprint","IMPRINT",EDGE,{"disambiguationData":[TD([[subQ2,-1.0]])],"derivedFrom":subQ1}),-1.0]])]});}
            var Q178;
            {var subQ0=sQuery(id+"F3.wireOp",EDGE,"E8.0.15.0");var subQ1=sQuery(id+"F3.wireOp",EDGE,"E6.0.20.0");var subQ2=makeQuery(id+"F3.imprint","INTERSECT",VERTEX,{"derivedFrom":[subQ1,subQ0]});Q178=makeQuery(id+"F3.imprint","IMPRINT",FACE,{"disambiguationData":[TD([[makeQuery(id+"F3.imprint","IMPRINT",EDGE,{"disambiguationData":[TD([[subQ2,-1.0]])],"derivedFrom":subQ1}),-1.0]])]});}
            var Q179;
            {var subQ0=sQuery(id+"F3.wireOp",EDGE,"E8.0.7.0");var subQ1=sQuery(id+"F3.wireOp",EDGE,"E6.0.23.0");var subQ2=makeQuery(id+"F3.imprint","INTERSECT",VERTEX,{"derivedFrom":[subQ1,subQ0]});Q179=makeQuery(id+"F3.imprint","IMPRINT",FACE,{"disambiguationData":[TD([[makeQuery(id+"F3.imprint","IMPRINT",EDGE,{"disambiguationData":[TD([[subQ2,-1.0]])],"derivedFrom":subQ1}),-1.0]])]});}
            var Q180;
            {var subQ0=sQuery(id+"F3.wireOp",EDGE,"E8.0.7.0");var subQ1=sQuery(id+"F3.wireOp",EDGE,"E6.0.22.0");var subQ2=makeQuery(id+"F3.imprint","INTERSECT",VERTEX,{"derivedFrom":[subQ1,subQ0]});Q180=makeQuery(id+"F3.imprint","IMPRINT",FACE,{"disambiguationData":[TD([[makeQuery(id+"F3.imprint","IMPRINT",EDGE,{"disambiguationData":[TD([[subQ2,-1.0]])],"derivedFrom":subQ1}),-1.0]])]});}
            var Q181;
            {var subQ0=sQuery(id+"F3.wireOp",EDGE,"E8.0.7.0");var subQ1=sQuery(id+"F3.wireOp",EDGE,"E6.0.21.0");var subQ2=makeQuery(id+"F3.imprint","INTERSECT",VERTEX,{"derivedFrom":[subQ1,subQ0]});Q181=makeQuery(id+"F3.imprint","IMPRINT",FACE,{"disambiguationData":[TD([[makeQuery(id+"F3.imprint","IMPRINT",EDGE,{"disambiguationData":[TD([[subQ2,-1.0]])],"derivedFrom":subQ1}),-1.0]])]});}
            var Q182;
            {var subQ0=sQuery(id+"F3.wireOp",EDGE,"E8.0.7.0");var subQ1=sQuery(id+"F3.wireOp",EDGE,"E6.0.20.0");var subQ2=makeQuery(id+"F3.imprint","INTERSECT",VERTEX,{"derivedFrom":[subQ1,subQ0]});Q182=makeQuery(id+"F3.imprint","IMPRINT",FACE,{"disambiguationData":[TD([[makeQuery(id+"F3.imprint","IMPRINT",EDGE,{"disambiguationData":[TD([[subQ2,-1.0]])],"derivedFrom":subQ1}),-1.0]])]});}
            var Q183;
            {var subQ0=sQuery(id+"F3.wireOp",EDGE,"E8.0.7.0");var subQ1=sQuery(id+"F3.wireOp",EDGE,"E6.0.19.0");var subQ2=makeQuery(id+"F3.imprint","INTERSECT",VERTEX,{"derivedFrom":[subQ1,subQ0]});Q183=makeQuery(id+"F3.imprint","IMPRINT",FACE,{"disambiguationData":[TD([[makeQuery(id+"F3.imprint","IMPRINT",EDGE,{"disambiguationData":[TD([[subQ2,-1.0]])],"derivedFrom":subQ1}),-1.0]])]});}
            var Q184;
            {var subQ0=sQuery(id+"F3.wireOp",EDGE,"E8.0.7.0");var subQ1=sQuery(id+"F3.wireOp",EDGE,"E6.0.18.0");var subQ2=makeQuery(id+"F3.imprint","INTERSECT",VERTEX,{"derivedFrom":[subQ1,subQ0]});Q184=makeQuery(id+"F3.imprint","IMPRINT",FACE,{"disambiguationData":[TD([[makeQuery(id+"F3.imprint","IMPRINT",EDGE,{"disambiguationData":[TD([[subQ2,-1.0]])],"derivedFrom":subQ1}),-1.0]])]});}
            var Q185;
            {var subQ0=sQuery(id+"F3.wireOp",EDGE,"E8.0.6.0");var subQ1=sQuery(id+"F3.wireOp",EDGE,"E6.0.18.0");var subQ2=makeQuery(id+"F3.imprint","INTERSECT",VERTEX,{"derivedFrom":[subQ1,subQ0]});Q185=makeQuery(id+"F3.imprint","IMPRINT",FACE,{"disambiguationData":[TD([[makeQuery(id+"F3.imprint","IMPRINT",EDGE,{"disambiguationData":[TD([[subQ2,-1.0]])],"derivedFrom":subQ1}),-1.0]])]});}
            var Q186;
            {var subQ0=sQuery(id+"F3.wireOp",EDGE,"E8.0.5.0");var subQ1=sQuery(id+"F3.wireOp",EDGE,"E6.0.18.0");var subQ2=makeQuery(id+"F3.imprint","INTERSECT",VERTEX,{"derivedFrom":[subQ1,subQ0]});Q186=makeQuery(id+"F3.imprint","IMPRINT",FACE,{"disambiguationData":[TD([[makeQuery(id+"F3.imprint","IMPRINT",EDGE,{"disambiguationData":[TD([[subQ2,-1.0]])],"derivedFrom":subQ1}),-1.0]])]});}
            var Q187;
            {var subQ0=sQuery(id+"F3.wireOp",EDGE,"E8.0.4.0");var subQ1=sQuery(id+"F3.wireOp",EDGE,"E6.0.18.0");var subQ2=makeQuery(id+"F3.imprint","INTERSECT",VERTEX,{"derivedFrom":[subQ1,subQ0]});Q187=makeQuery(id+"F3.imprint","IMPRINT",FACE,{"disambiguationData":[TD([[makeQuery(id+"F3.imprint","IMPRINT",EDGE,{"disambiguationData":[TD([[subQ2,-1.0]])],"derivedFrom":subQ1}),-1.0]])]});}
            var Q188;
            {var subQ0=sQuery(id+"F3.wireOp",EDGE,"E8.0.3.0");var subQ1=sQuery(id+"F3.wireOp",EDGE,"E6.0.18.0");var subQ2=makeQuery(id+"F3.imprint","INTERSECT",VERTEX,{"derivedFrom":[subQ1,subQ0]});Q188=makeQuery(id+"F3.imprint","IMPRINT",FACE,{"disambiguationData":[TD([[makeQuery(id+"F3.imprint","IMPRINT",EDGE,{"disambiguationData":[TD([[subQ2,-1.0]])],"derivedFrom":subQ1}),-1.0]])]});}
            var Q189;
            {var subQ0=sQuery(id+"F3.wireOp",EDGE,"E8.0.2.0");var subQ1=sQuery(id+"F3.wireOp",EDGE,"E6.0.18.0");var subQ2=makeQuery(id+"F3.imprint","INTERSECT",VERTEX,{"derivedFrom":[subQ1,subQ0]});Q189=makeQuery(id+"F3.imprint","IMPRINT",FACE,{"disambiguationData":[TD([[makeQuery(id+"F3.imprint","IMPRINT",EDGE,{"disambiguationData":[TD([[subQ2,-1.0]])],"derivedFrom":subQ1}),-1.0]])]});}
            var Q190;
            {var subQ0=sQuery(id+"F3.wireOp",EDGE,"E8.0.5.0");var subQ1=sQuery(id+"F3.wireOp",EDGE,"E6.0.22.0");var subQ2=makeQuery(id+"F3.imprint","INTERSECT",VERTEX,{"derivedFrom":[subQ1,subQ0]});Q190=makeQuery(id+"F3.imprint","IMPRINT",FACE,{"disambiguationData":[TD([[makeQuery(id+"F3.imprint","IMPRINT",EDGE,{"disambiguationData":[TD([[subQ2,-1.0]])],"derivedFrom":subQ1}),-1.0]])]});}
            var Q191;
            {var subQ0=sQuery(id+"F3.wireOp",EDGE,"E8.0.5.0");var subQ1=sQuery(id+"F3.wireOp",EDGE,"E6.0.21.0");var subQ2=makeQuery(id+"F3.imprint","INTERSECT",VERTEX,{"derivedFrom":[subQ1,subQ0]});Q191=makeQuery(id+"F3.imprint","IMPRINT",FACE,{"disambiguationData":[TD([[makeQuery(id+"F3.imprint","IMPRINT",EDGE,{"disambiguationData":[TD([[subQ2,-1.0]])],"derivedFrom":subQ1}),-1.0]])]});}
            var Q192;
            {var subQ0=sQuery(id+"F3.wireOp",EDGE,"E8.0.5.0");var subQ1=sQuery(id+"F3.wireOp",EDGE,"E6.0.20.0");var subQ2=makeQuery(id+"F3.imprint","INTERSECT",VERTEX,{"derivedFrom":[subQ1,subQ0]});Q192=makeQuery(id+"F3.imprint","IMPRINT",FACE,{"disambiguationData":[TD([[makeQuery(id+"F3.imprint","IMPRINT",EDGE,{"disambiguationData":[TD([[subQ2,-1.0]])],"derivedFrom":subQ1}),-1.0]])]});}
            var Q193;
            {var subQ0=sQuery(id+"F3.wireOp",EDGE,"E8.0.4.0");var subQ1=sQuery(id+"F3.wireOp",EDGE,"E6.0.20.0");var subQ2=makeQuery(id+"F3.imprint","INTERSECT",VERTEX,{"derivedFrom":[subQ1,subQ0]});Q193=makeQuery(id+"F3.imprint","IMPRINT",FACE,{"disambiguationData":[TD([[makeQuery(id+"F3.imprint","IMPRINT",EDGE,{"disambiguationData":[TD([[subQ2,-1.0]])],"derivedFrom":subQ1}),-1.0]])]});}
            var Q194;
            {var subQ0=sQuery(id+"F3.wireOp",EDGE,"E8.0.4.0");var subQ1=sQuery(id+"F3.wireOp",EDGE,"E6.0.21.0");var subQ2=makeQuery(id+"F3.imprint","INTERSECT",VERTEX,{"derivedFrom":[subQ1,subQ0]});Q194=makeQuery(id+"F3.imprint","IMPRINT",FACE,{"disambiguationData":[TD([[makeQuery(id+"F3.imprint","IMPRINT",EDGE,{"disambiguationData":[TD([[subQ2,-1.0]])],"derivedFrom":subQ1}),-1.0]])]});}
            var Q195;
            {var subQ0=sQuery(id+"F3.wireOp",EDGE,"E8.0.4.0");var subQ1=sQuery(id+"F3.wireOp",EDGE,"E6.0.22.0");var subQ2=makeQuery(id+"F3.imprint","INTERSECT",VERTEX,{"derivedFrom":[subQ1,subQ0]});Q195=makeQuery(id+"F3.imprint","IMPRINT",FACE,{"disambiguationData":[TD([[makeQuery(id+"F3.imprint","IMPRINT",EDGE,{"disambiguationData":[TD([[subQ2,-1.0]])],"derivedFrom":subQ1}),-1.0]])]});}
            var Q196;
            {var subQ0=sQuery(id+"F3.wireOp",EDGE,"E8.0.3.0");var subQ1=sQuery(id+"F3.wireOp",EDGE,"E6.0.22.0");var subQ2=makeQuery(id+"F3.imprint","INTERSECT",VERTEX,{"derivedFrom":[subQ1,subQ0]});Q196=makeQuery(id+"F3.imprint","IMPRINT",FACE,{"disambiguationData":[TD([[makeQuery(id+"F3.imprint","IMPRINT",EDGE,{"disambiguationData":[TD([[subQ2,-1.0]])],"derivedFrom":subQ1}),-1.0]])]});}
            var Q197;
            {var subQ0=sQuery(id+"F3.wireOp",EDGE,"E8.0.3.0");var subQ1=sQuery(id+"F3.wireOp",EDGE,"E6.0.21.0");var subQ2=makeQuery(id+"F3.imprint","INTERSECT",VERTEX,{"derivedFrom":[subQ1,subQ0]});Q197=makeQuery(id+"F3.imprint","IMPRINT",FACE,{"disambiguationData":[TD([[makeQuery(id+"F3.imprint","IMPRINT",EDGE,{"disambiguationData":[TD([[subQ2,-1.0]])],"derivedFrom":subQ1}),-1.0]])]});}
            var Q198;
            {var subQ0=sQuery(id+"F3.wireOp",EDGE,"E8.0.3.0");var subQ1=sQuery(id+"F3.wireOp",EDGE,"E6.0.20.0");var subQ2=makeQuery(id+"F3.imprint","INTERSECT",VERTEX,{"derivedFrom":[subQ1,subQ0]});Q198=makeQuery(id+"F3.imprint","IMPRINT",FACE,{"disambiguationData":[TD([[makeQuery(id+"F3.imprint","IMPRINT",EDGE,{"disambiguationData":[TD([[subQ2,-1.0]])],"derivedFrom":subQ1}),-1.0]])]});}
            var Q199;
            {var subQ0=sQuery(id+"F3.wireOp",EDGE,"E8.0.9.0");var subQ1=sQuery(id+"F3.wireOp",EDGE,"E6.0.22.0");var subQ2=makeQuery(id+"F3.imprint","INTERSECT",VERTEX,{"derivedFrom":[subQ1,subQ0]});Q199=makeQuery(id+"F3.imprint","IMPRINT",FACE,{"disambiguationData":[TD([[makeQuery(id+"F3.imprint","IMPRINT",EDGE,{"disambiguationData":[TD([[subQ2,-1.0]])],"derivedFrom":subQ1}),-1.0]])]});}
            var Q200;
            {var subQ0=sQuery(id+"F3.wireOp",EDGE,"E8.0.10.0");var subQ1=sQuery(id+"F3.wireOp",EDGE,"E6.0.22.0");var subQ2=makeQuery(id+"F3.imprint","INTERSECT",VERTEX,{"derivedFrom":[subQ1,subQ0]});Q200=makeQuery(id+"F3.imprint","IMPRINT",FACE,{"disambiguationData":[TD([[makeQuery(id+"F3.imprint","IMPRINT",EDGE,{"disambiguationData":[TD([[subQ2,-1.0]])],"derivedFrom":subQ1}),-1.0]])]});}
            var Q201;
            {var subQ0=sQuery(id+"F3.wireOp",EDGE,"E8.0.11.0");var subQ1=sQuery(id+"F3.wireOp",EDGE,"E6.0.21.0");var subQ2=makeQuery(id+"F3.imprint","INTERSECT",VERTEX,{"derivedFrom":[subQ1,subQ0]});Q201=makeQuery(id+"F3.imprint","IMPRINT",FACE,{"disambiguationData":[TD([[makeQuery(id+"F3.imprint","IMPRINT",EDGE,{"disambiguationData":[TD([[subQ2,-1.0]])],"derivedFrom":subQ1}),-1.0]])]});}
            var Q202;
            {var subQ0=sQuery(id+"F3.wireOp",EDGE,"E8.0.12.0");var subQ1=sQuery(id+"F3.wireOp",EDGE,"E6.0.21.0");var subQ2=makeQuery(id+"F3.imprint","INTERSECT",VERTEX,{"derivedFrom":[subQ1,subQ0]});Q202=makeQuery(id+"F3.imprint","IMPRINT",FACE,{"disambiguationData":[TD([[makeQuery(id+"F3.imprint","IMPRINT",EDGE,{"disambiguationData":[TD([[subQ2,-1.0]])],"derivedFrom":subQ1}),-1.0]])]});}
            var Q203;
            {var subQ0=sQuery(id+"F3.wireOp",EDGE,"E8.0.10.0");var subQ1=sQuery(id+"F3.wireOp",EDGE,"E6.0.20.0");var subQ2=makeQuery(id+"F3.imprint","INTERSECT",VERTEX,{"derivedFrom":[subQ1,subQ0]});Q203=makeQuery(id+"F3.imprint","IMPRINT",FACE,{"disambiguationData":[TD([[makeQuery(id+"F3.imprint","IMPRINT",EDGE,{"disambiguationData":[TD([[subQ2,-1.0]])],"derivedFrom":subQ1}),-1.0]])]});}
            var Q204;
            {var subQ0=sQuery(id+"F3.wireOp",EDGE,"E8.0.9.0");var subQ1=sQuery(id+"F3.wireOp",EDGE,"E6.0.19.0");var subQ2=makeQuery(id+"F3.imprint","INTERSECT",VERTEX,{"derivedFrom":[subQ1,subQ0]});Q204=makeQuery(id+"F3.imprint","IMPRINT",FACE,{"disambiguationData":[TD([[makeQuery(id+"F3.imprint","IMPRINT",EDGE,{"disambiguationData":[TD([[subQ2,-1.0]])],"derivedFrom":subQ1}),-1.0]])]});}
            var Q205;
            {var subQ0=sQuery(id+"F3.wireOp",EDGE,"E8.0.9.0");var subQ1=sQuery(id+"F3.wireOp",EDGE,"E6.0.18.0");var subQ2=makeQuery(id+"F3.imprint","INTERSECT",VERTEX,{"derivedFrom":[subQ1,subQ0]});Q205=makeQuery(id+"F3.imprint","IMPRINT",FACE,{"disambiguationData":[TD([[makeQuery(id+"F3.imprint","IMPRINT",EDGE,{"disambiguationData":[TD([[subQ2,-1.0]])],"derivedFrom":subQ1}),-1.0]])]});}
            var Q206;
            {var subQ0=sQuery(id+"F3.wireOp",EDGE,"E8.0.11.0");var subQ1=sQuery(id+"F3.wireOp",EDGE,"E6.0.18.0");var subQ2=makeQuery(id+"F3.imprint","INTERSECT",VERTEX,{"derivedFrom":[subQ1,subQ0]});Q206=makeQuery(id+"F3.imprint","IMPRINT",FACE,{"disambiguationData":[TD([[makeQuery(id+"F3.imprint","IMPRINT",EDGE,{"disambiguationData":[TD([[subQ2,-1.0]])],"derivedFrom":subQ1}),-1.0]])]});}
            var Q207;
            {var subQ0=sQuery(id+"F3.wireOp",EDGE,"E8.0.11.0");var subQ1=sQuery(id+"F3.wireOp",EDGE,"E6.0.19.0");var subQ2=makeQuery(id+"F3.imprint","INTERSECT",VERTEX,{"derivedFrom":[subQ1,subQ0]});Q207=makeQuery(id+"F3.imprint","IMPRINT",FACE,{"disambiguationData":[TD([[makeQuery(id+"F3.imprint","IMPRINT",EDGE,{"disambiguationData":[TD([[subQ2,-1.0]])],"derivedFrom":subQ1}),-1.0]])]});}
            var Q208;
            {var subQ0=sQuery(id+"F3.wireOp",EDGE,"E8.0.12.0");var subQ1=sQuery(id+"F3.wireOp",EDGE,"E6.0.19.0");var subQ2=makeQuery(id+"F3.imprint","INTERSECT",VERTEX,{"derivedFrom":[subQ1,subQ0]});Q208=makeQuery(id+"F3.imprint","IMPRINT",FACE,{"disambiguationData":[TD([[makeQuery(id+"F3.imprint","IMPRINT",EDGE,{"disambiguationData":[TD([[subQ2,-1.0]])],"derivedFrom":subQ1}),-1.0]])]});}
            var Q209;
            {var subQ0=sQuery(id+"F3.wireOp",EDGE,"E8.0.13.0");var subQ1=sQuery(id+"F3.wireOp",EDGE,"E6.0.20.0");var subQ2=makeQuery(id+"F3.imprint","INTERSECT",VERTEX,{"derivedFrom":[subQ1,subQ0]});Q209=makeQuery(id+"F3.imprint","IMPRINT",FACE,{"disambiguationData":[TD([[makeQuery(id+"F3.imprint","IMPRINT",EDGE,{"disambiguationData":[TD([[subQ2,-1.0]])],"derivedFrom":subQ1}),-1.0]])]});}
            var Q210;
            {var subQ0=sQuery(id+"F3.wireOp",EDGE,"E8.0.13.0");var subQ1=sQuery(id+"F3.wireOp",EDGE,"E6.0.19.0");var subQ2=makeQuery(id+"F3.imprint","INTERSECT",VERTEX,{"derivedFrom":[subQ1,subQ0]});Q210=makeQuery(id+"F3.imprint","IMPRINT",FACE,{"disambiguationData":[TD([[makeQuery(id+"F3.imprint","IMPRINT",EDGE,{"disambiguationData":[TD([[subQ2,-1.0]])],"derivedFrom":subQ1}),-1.0]])]});}
            var Q211;
            {var subQ0=sQuery(id+"F3.wireOp",EDGE,"E8.0.14.0");var subQ1=sQuery(id+"F3.wireOp",EDGE,"E6.0.19.0");var subQ2=makeQuery(id+"F3.imprint","INTERSECT",VERTEX,{"derivedFrom":[subQ1,subQ0]});Q211=makeQuery(id+"F3.imprint","IMPRINT",FACE,{"disambiguationData":[TD([[makeQuery(id+"F3.imprint","IMPRINT",EDGE,{"disambiguationData":[TD([[subQ2,-1.0]])],"derivedFrom":subQ1}),-1.0]])]});}
            var Q212;
            {var subQ0=sQuery(id+"F3.wireOp",EDGE,"E8.0.4.0");var subQ1=sQuery(id+"F3.wireOp",EDGE,"E4.1.0.0");var subQ2=makeQuery(id+"F3.imprint","INTERSECT",VERTEX,{"derivedFrom":[subQ1,subQ0]});Q212=makeQuery(id+"F3.imprint","IMPRINT",FACE,{"disambiguationData":[TD([[makeQuery(id+"F3.imprint","IMPRINT",EDGE,{"disambiguationData":[TD([[subQ2,-1.0]])],"derivedFrom":subQ1}),-1.0]])]});}
            var Q213;
            {var subQ0=sQuery(id+"F3.wireOp",EDGE,"E8.0.5.0");var subQ1=sQuery(id+"F3.wireOp",EDGE,"E4.2.0.0");var subQ2=makeQuery(id+"F3.imprint","INTERSECT",VERTEX,{"derivedFrom":[subQ1,subQ0]});Q213=makeQuery(id+"F3.imprint","IMPRINT",FACE,{"disambiguationData":[TD([[makeQuery(id+"F3.imprint","IMPRINT",EDGE,{"disambiguationData":[TD([[subQ2,-1.0]])],"derivedFrom":subQ1}),-1.0]])]});}
            var Q214;
            {var subQ0=sQuery(id+"F3.wireOp",EDGE,"E8.0.3.0");var subQ1=sQuery(id+"F3.wireOp",EDGE,"E4.3.0.0");var subQ2=makeQuery(id+"F3.imprint","INTERSECT",VERTEX,{"derivedFrom":[subQ1,subQ0]});Q214=makeQuery(id+"F3.imprint","IMPRINT",FACE,{"disambiguationData":[TD([[makeQuery(id+"F3.imprint","IMPRINT",EDGE,{"disambiguationData":[TD([[subQ2,-1.0]])],"derivedFrom":subQ1}),-1.0]])]});}
            var Q215;
            {var subQ0=sQuery(id+"F3.wireOp",EDGE,"E8.0.6.0");var subQ1=sQuery(id+"F3.wireOp",EDGE,"E4.1.0.0");var subQ2=makeQuery(id+"F3.imprint","INTERSECT",VERTEX,{"derivedFrom":[subQ1,subQ0]});Q215=makeQuery(id+"F3.imprint","IMPRINT",FACE,{"disambiguationData":[TD([[makeQuery(id+"F3.imprint","IMPRINT",EDGE,{"disambiguationData":[TD([[subQ2,-1.0]])],"derivedFrom":subQ1}),-1.0]])]});}
            var Q216;
            {var subQ0=sQuery(id+"F3.wireOp",EDGE,"E8.0.7.0");var subQ1=sQuery(id+"F3.wireOp",EDGE,"E4.1.0.0");var subQ2=makeQuery(id+"F3.imprint","INTERSECT",VERTEX,{"derivedFrom":[subQ1,subQ0]});Q216=makeQuery(id+"F3.imprint","IMPRINT",FACE,{"disambiguationData":[TD([[makeQuery(id+"F3.imprint","IMPRINT",EDGE,{"disambiguationData":[TD([[subQ2,-1.0]])],"derivedFrom":subQ1}),-1.0]])]});}
            var Q217;
            {var subQ0=sQuery(id+"F3.wireOp",EDGE,"E8.0.8.0");var subQ1=sQuery(id+"F3.wireOp",EDGE,"E4.1.0.0");var subQ2=makeQuery(id+"F3.imprint","INTERSECT",VERTEX,{"derivedFrom":[subQ1,subQ0]});Q217=makeQuery(id+"F3.imprint","IMPRINT",FACE,{"disambiguationData":[TD([[makeQuery(id+"F3.imprint","IMPRINT",EDGE,{"disambiguationData":[TD([[subQ2,-1.0]])],"derivedFrom":subQ1}),-1.0]])]});}
            var Q218;
            {var subQ0=sQuery(id+"F3.wireOp",EDGE,"E8.0.9.0");var subQ1=sQuery(id+"F3.wireOp",EDGE,"E4.1.0.0");var subQ2=makeQuery(id+"F3.imprint","INTERSECT",VERTEX,{"derivedFrom":[subQ1,subQ0]});Q218=makeQuery(id+"F3.imprint","IMPRINT",FACE,{"disambiguationData":[TD([[makeQuery(id+"F3.imprint","IMPRINT",EDGE,{"disambiguationData":[TD([[subQ2,-1.0]])],"derivedFrom":subQ1}),-1.0]])]});}
            var Q219;
            {var subQ0=sQuery(id+"F3.wireOp",EDGE,"E8.0.10.0");var subQ1=sQuery(id+"F3.wireOp",EDGE,"E4.1.0.0");var subQ2=makeQuery(id+"F3.imprint","INTERSECT",VERTEX,{"derivedFrom":[subQ1,subQ0]});Q219=makeQuery(id+"F3.imprint","IMPRINT",FACE,{"disambiguationData":[TD([[makeQuery(id+"F3.imprint","IMPRINT",EDGE,{"disambiguationData":[TD([[subQ2,-1.0]])],"derivedFrom":subQ1}),-1.0]])]});}
            var Q220;
            {var subQ0=sQuery(id+"F3.wireOp",EDGE,"E8.0.11.0");var subQ1=sQuery(id+"F3.wireOp",EDGE,"E4.1.0.0");var subQ2=makeQuery(id+"F3.imprint","INTERSECT",VERTEX,{"derivedFrom":[subQ1,subQ0]});Q220=makeQuery(id+"F3.imprint","IMPRINT",FACE,{"disambiguationData":[TD([[makeQuery(id+"F3.imprint","IMPRINT",EDGE,{"disambiguationData":[TD([[subQ2,-1.0]])],"derivedFrom":subQ1}),-1.0]])]});}
            var Q221;
            {var subQ0=sQuery(id+"F3.wireOp",EDGE,"E8.0.7.0");var subQ1=sQuery(id+"F3.wireOp",EDGE,"E4.2.0.0");var subQ2=makeQuery(id+"F3.imprint","INTERSECT",VERTEX,{"derivedFrom":[subQ1,subQ0]});Q221=makeQuery(id+"F3.imprint","IMPRINT",FACE,{"disambiguationData":[TD([[makeQuery(id+"F3.imprint","IMPRINT",EDGE,{"disambiguationData":[TD([[subQ2,-1.0]])],"derivedFrom":subQ1}),-1.0]])]});}
            var Q222;
            {var subQ0=sQuery(id+"F3.wireOp",EDGE,"E8.0.9.0");var subQ1=sQuery(id+"F3.wireOp",EDGE,"E4.2.0.0");var subQ2=makeQuery(id+"F3.imprint","INTERSECT",VERTEX,{"derivedFrom":[subQ1,subQ0]});Q222=makeQuery(id+"F3.imprint","IMPRINT",FACE,{"disambiguationData":[TD([[makeQuery(id+"F3.imprint","IMPRINT",EDGE,{"disambiguationData":[TD([[subQ2,-1.0]])],"derivedFrom":subQ1}),-1.0]])]});}
            var Q223;
            {var subQ0=sQuery(id+"F3.wireOp",EDGE,"E8.0.11.0");var subQ1=sQuery(id+"F3.wireOp",EDGE,"E4.3.0.0");var subQ2=makeQuery(id+"F3.imprint","INTERSECT",VERTEX,{"derivedFrom":[subQ1,subQ0]});Q223=makeQuery(id+"F3.imprint","IMPRINT",FACE,{"disambiguationData":[TD([[makeQuery(id+"F3.imprint","IMPRINT",EDGE,{"disambiguationData":[TD([[subQ2,-1.0]])],"derivedFrom":subQ1}),-1.0]])]});}
            var Q224;
            {var subQ0=sQuery(id+"F3.wireOp",EDGE,"E8.0.11.0");var subQ1=sQuery(id+"F3.wireOp",EDGE,"E4.2.0.0");var subQ2=makeQuery(id+"F3.imprint","INTERSECT",VERTEX,{"derivedFrom":[subQ1,subQ0]});Q224=makeQuery(id+"F3.imprint","IMPRINT",FACE,{"disambiguationData":[TD([[makeQuery(id+"F3.imprint","IMPRINT",EDGE,{"disambiguationData":[TD([[subQ2,-1.0]])],"derivedFrom":subQ1}),-1.0]])]});}
            var Q225;
            {var subQ0=sQuery(id+"F3.wireOp",EDGE,"E8.0.12.0");var subQ1=sQuery(id+"F3.wireOp",EDGE,"E4.2.0.0");var subQ2=makeQuery(id+"F3.imprint","INTERSECT",VERTEX,{"derivedFrom":[subQ1,subQ0]});Q225=makeQuery(id+"F3.imprint","IMPRINT",FACE,{"disambiguationData":[TD([[makeQuery(id+"F3.imprint","IMPRINT",EDGE,{"disambiguationData":[TD([[subQ2,-1.0]])],"derivedFrom":subQ1}),-1.0]])]});}
            var Q226;
            {var subQ0=sQuery(id+"F3.wireOp",EDGE,"E8.0.12.0");var subQ1=sQuery(id+"F3.wireOp",EDGE,"E4.1.0.0");var subQ2=makeQuery(id+"F3.imprint","INTERSECT",VERTEX,{"derivedFrom":[subQ1,subQ0]});Q226=makeQuery(id+"F3.imprint","IMPRINT",FACE,{"disambiguationData":[TD([[makeQuery(id+"F3.imprint","IMPRINT",EDGE,{"disambiguationData":[TD([[subQ2,-1.0]])],"derivedFrom":subQ1}),-1.0]])]});}
            var Q227;
            {var subQ0=sQuery(id+"F3.wireOp",EDGE,"E8.0.17.0");var subQ1=sQuery(id+"F3.wireOp",EDGE,"E4.1.0.0");var subQ2=makeQuery(id+"F3.imprint","INTERSECT",VERTEX,{"derivedFrom":[subQ1,subQ0]});Q227=makeQuery(id+"F3.imprint","IMPRINT",FACE,{"disambiguationData":[TD([[makeQuery(id+"F3.imprint","IMPRINT",EDGE,{"disambiguationData":[TD([[subQ2,-1.0]])],"derivedFrom":subQ1}),-1.0]])]});}
            var Q228;
            {var subQ0=sQuery(id+"F3.wireOp",EDGE,"E8.0.16.0");var subQ1=sQuery(id+"F3.wireOp",EDGE,"E4.1.0.0");var subQ2=makeQuery(id+"F3.imprint","INTERSECT",VERTEX,{"derivedFrom":[subQ1,subQ0]});Q228=makeQuery(id+"F3.imprint","IMPRINT",FACE,{"disambiguationData":[TD([[makeQuery(id+"F3.imprint","IMPRINT",EDGE,{"disambiguationData":[TD([[subQ2,-1.0]])],"derivedFrom":subQ1}),-1.0]])]});}
            var Q229;
            {var subQ0=sQuery(id+"F3.wireOp",EDGE,"E8.0.15.0");var subQ1=sQuery(id+"F3.wireOp",EDGE,"E4.1.0.0");var subQ2=makeQuery(id+"F3.imprint","INTERSECT",VERTEX,{"derivedFrom":[subQ1,subQ0]});Q229=makeQuery(id+"F3.imprint","IMPRINT",FACE,{"disambiguationData":[TD([[makeQuery(id+"F3.imprint","IMPRINT",EDGE,{"disambiguationData":[TD([[subQ2,-1.0]])],"derivedFrom":subQ1}),-1.0]])]});}
            var Q230;
            {var subQ0=sQuery(id+"F3.wireOp",EDGE,"E8.0.15.0");var subQ1=sQuery(id+"F3.wireOp",EDGE,"E4.2.0.0");var subQ2=makeQuery(id+"F3.imprint","INTERSECT",VERTEX,{"derivedFrom":[subQ1,subQ0]});Q230=makeQuery(id+"F3.imprint","IMPRINT",FACE,{"disambiguationData":[TD([[makeQuery(id+"F3.imprint","IMPRINT",EDGE,{"disambiguationData":[TD([[subQ2,-1.0]])],"derivedFrom":subQ1}),-1.0]])]});}
            var Q231;
            {var subQ0=sQuery(id+"F3.wireOp",EDGE,"E8.0.14.0");var subQ1=sQuery(id+"F3.wireOp",EDGE,"E4.1.0.0");var subQ2=makeQuery(id+"F3.imprint","INTERSECT",VERTEX,{"derivedFrom":[subQ1,subQ0]});Q231=makeQuery(id+"F3.imprint","IMPRINT",FACE,{"disambiguationData":[TD([[makeQuery(id+"F3.imprint","IMPRINT",EDGE,{"disambiguationData":[TD([[subQ2,-1.0]])],"derivedFrom":subQ1}),-1.0]])]});}
            var Q232;
            {var subQ0=sQuery(id+"F3.wireOp",EDGE,"E8.0.13.0");var subQ1=sQuery(id+"F3.wireOp",EDGE,"E4.1.0.0");var subQ2=makeQuery(id+"F3.imprint","INTERSECT",VERTEX,{"derivedFrom":[subQ1,subQ0]});Q232=makeQuery(id+"F3.imprint","IMPRINT",FACE,{"disambiguationData":[TD([[makeQuery(id+"F3.imprint","IMPRINT",EDGE,{"disambiguationData":[TD([[subQ2,-1.0]])],"derivedFrom":subQ1}),-1.0]])]});}
            var Q233;
            {var subQ0=sQuery(id+"F3.wireOp",EDGE,"E8.0.13.0");var subQ1=sQuery(id+"F3.wireOp",EDGE,"E4.2.0.0");var subQ2=makeQuery(id+"F3.imprint","INTERSECT",VERTEX,{"derivedFrom":[subQ1,subQ0]});Q233=makeQuery(id+"F3.imprint","IMPRINT",FACE,{"disambiguationData":[TD([[makeQuery(id+"F3.imprint","IMPRINT",EDGE,{"disambiguationData":[TD([[subQ2,-1.0]])],"derivedFrom":subQ1}),-1.0]])]});}
            var Q234;
            {var subQ0=sQuery(id+"F3.wireOp",EDGE,"E8.0.17.0");var subQ1=sQuery(id+"F3.wireOp",EDGE,"E4.3.0.0");var subQ2=makeQuery(id+"F3.imprint","INTERSECT",VERTEX,{"derivedFrom":[subQ1,subQ0]});Q234=makeQuery(id+"F3.imprint","IMPRINT",FACE,{"disambiguationData":[TD([[makeQuery(id+"F3.imprint","IMPRINT",EDGE,{"disambiguationData":[TD([[subQ2,-1.0]])],"derivedFrom":subQ1}),-1.0]])]});}
            var Q235;
            {var subQ0=sQuery(id+"F3.wireOp",EDGE,"E8.0.17.0");var subQ1=sQuery(id+"F3.wireOp",EDGE,"E4.5.0.0");var subQ2=makeQuery(id+"F3.imprint","INTERSECT",VERTEX,{"derivedFrom":[subQ1,subQ0]});Q235=makeQuery(id+"F3.imprint","IMPRINT",FACE,{"disambiguationData":[TD([[makeQuery(id+"F3.imprint","IMPRINT",EDGE,{"disambiguationData":[TD([[subQ2,-1.0]])],"derivedFrom":subQ1}),-1.0]])]});}
            var Q236;
            {var subQ0=sQuery(id+"F3.wireOp",EDGE,"E8.0.16.0");var subQ1=sQuery(id+"F3.wireOp",EDGE,"E4.5.0.0");var subQ2=makeQuery(id+"F3.imprint","INTERSECT",VERTEX,{"derivedFrom":[subQ1,subQ0]});Q236=makeQuery(id+"F3.imprint","IMPRINT",FACE,{"disambiguationData":[TD([[makeQuery(id+"F3.imprint","IMPRINT",EDGE,{"disambiguationData":[TD([[subQ2,-1.0]])],"derivedFrom":subQ1}),-1.0]])]});}
            var Q237;
            {var subQ0=sQuery(id+"F3.wireOp",EDGE,"E8.0.17.0");var subQ1=sQuery(id+"F3.wireOp",EDGE,"E4.7.0.0");var subQ2=makeQuery(id+"F3.imprint","INTERSECT",VERTEX,{"derivedFrom":[subQ1,subQ0]});Q237=makeQuery(id+"F3.imprint","IMPRINT",FACE,{"disambiguationData":[TD([[makeQuery(id+"F3.imprint","IMPRINT",EDGE,{"disambiguationData":[TD([[subQ2,-1.0]])],"derivedFrom":subQ1}),-1.0]])]});}
            var Q238;
            {var subQ0=sQuery(id+"F3.wireOp",EDGE,"E8.0.16.0");var subQ1=sQuery(id+"F3.wireOp",EDGE,"E4.8.0.0");var subQ2=makeQuery(id+"F3.imprint","INTERSECT",VERTEX,{"derivedFrom":[subQ1,subQ0]});Q238=makeQuery(id+"F3.imprint","IMPRINT",FACE,{"disambiguationData":[TD([[makeQuery(id+"F3.imprint","IMPRINT",EDGE,{"disambiguationData":[TD([[subQ2,-1.0]])],"derivedFrom":subQ1}),-1.0]])]});}
            var Q239;
            {var subQ0=sQuery(id+"F3.wireOp",EDGE,"E8.0.15.0");var subQ1=sQuery(id+"F3.wireOp",EDGE,"E4.9.0.0");var subQ2=makeQuery(id+"F3.imprint","INTERSECT",VERTEX,{"derivedFrom":[subQ1,subQ0]});Q239=makeQuery(id+"F3.imprint","IMPRINT",FACE,{"disambiguationData":[TD([[makeQuery(id+"F3.imprint","IMPRINT",EDGE,{"disambiguationData":[TD([[subQ2,-1.0]])],"derivedFrom":subQ1}),-1.0]])]});}
            var Q240;
            {var subQ0=sQuery(id+"F3.wireOp",EDGE,"E8.0.14.0");var subQ1=sQuery(id+"F3.wireOp",EDGE,"E4.9.0.0");var subQ2=makeQuery(id+"F3.imprint","INTERSECT",VERTEX,{"derivedFrom":[subQ1,subQ0]});Q240=makeQuery(id+"F3.imprint","IMPRINT",FACE,{"disambiguationData":[TD([[makeQuery(id+"F3.imprint","IMPRINT",EDGE,{"disambiguationData":[TD([[subQ2,-1.0]])],"derivedFrom":subQ1}),-1.0]])]});}
            var Q241;
            {var subQ0=sQuery(id+"F3.wireOp",EDGE,"E8.0.2.0");var subQ1=sQuery(id+"F3.wireOp",EDGE,"E4.8.0.0");var subQ2=makeQuery(id+"F3.imprint","INTERSECT",VERTEX,{"derivedFrom":[subQ1,subQ0]});Q241=makeQuery(id+"F3.imprint","IMPRINT",FACE,{"disambiguationData":[TD([[makeQuery(id+"F3.imprint","IMPRINT",EDGE,{"disambiguationData":[TD([[subQ2,-1.0]])],"derivedFrom":subQ1}),-1.0]])]});}
            var Q242;
            {var subQ0=sQuery(id+"F3.wireOp",EDGE,"E8.0.2.0");var subQ1=sQuery(id+"F3.wireOp",EDGE,"E4.9.0.0");var subQ2=makeQuery(id+"F3.imprint","INTERSECT",VERTEX,{"derivedFrom":[subQ1,subQ0]});Q242=makeQuery(id+"F3.imprint","IMPRINT",FACE,{"disambiguationData":[TD([[makeQuery(id+"F3.imprint","IMPRINT",EDGE,{"disambiguationData":[TD([[subQ2,-1.0]])],"derivedFrom":subQ1}),-1.0]])]});}
            var Q243;
            {var subQ0=sQuery(id+"F3.wireOp",EDGE,"E8.0.3.0");var subQ1=sQuery(id+"F3.wireOp",EDGE,"E5.0.10.0");var subQ2=makeQuery(id+"F3.imprint","INTERSECT",VERTEX,{"derivedFrom":[subQ1,subQ0]});Q243=makeQuery(id+"F3.imprint","IMPRINT",FACE,{"disambiguationData":[TD([[makeQuery(id+"F3.imprint","IMPRINT",EDGE,{"disambiguationData":[TD([[subQ2,-1.0]])],"derivedFrom":subQ1}),-1.0]])]});}
            var Q244;
            {var subQ0=sQuery(id+"F3.wireOp",EDGE,"E8.0.2.0");var subQ1=sQuery(id+"F3.wireOp",EDGE,"E4.5.0.0");var subQ2=makeQuery(id+"F3.imprint","INTERSECT",VERTEX,{"derivedFrom":[subQ1,subQ0]});Q244=makeQuery(id+"F3.imprint","IMPRINT",FACE,{"disambiguationData":[TD([[makeQuery(id+"F3.imprint","IMPRINT",EDGE,{"disambiguationData":[TD([[subQ2,-1.0]])],"derivedFrom":subQ1}),-1.0]])]});}
            var Q245;
            {var subQ0=sQuery(id+"F3.wireOp",EDGE,"E8.0.3.0");var subQ1=sQuery(id+"F3.wireOp",EDGE,"E4.5.0.0");var subQ2=makeQuery(id+"F3.imprint","INTERSECT",VERTEX,{"derivedFrom":[subQ1,subQ0]});Q245=makeQuery(id+"F3.imprint","IMPRINT",FACE,{"disambiguationData":[TD([[makeQuery(id+"F3.imprint","IMPRINT",EDGE,{"disambiguationData":[TD([[subQ2,-1.0]])],"derivedFrom":subQ1}),-1.0]])]});}
            var Q246;
            {var subQ0=sQuery(id+"F3.wireOp",EDGE,"E8.0.2.0");var subQ1=sQuery(id+"F3.wireOp",EDGE,"E6.0.16.0");var subQ2=makeQuery(id+"F3.imprint","INTERSECT",VERTEX,{"derivedFrom":[subQ1,subQ0]});Q246=makeQuery(id+"F3.imprint","IMPRINT",FACE,{"disambiguationData":[TD([[makeQuery(id+"F3.imprint","IMPRINT",EDGE,{"disambiguationData":[TD([[subQ2,-1.0]])],"derivedFrom":subQ1}),-1.0]])]});}
            var Q247;
            {var subQ0=sQuery(id+"F3.wireOp",EDGE,"E8.0.3.0");var subQ1=sQuery(id+"F3.wireOp",EDGE,"E6.0.16.0");var subQ2=makeQuery(id+"F3.imprint","INTERSECT",VERTEX,{"derivedFrom":[subQ1,subQ0]});Q247=makeQuery(id+"F3.imprint","IMPRINT",FACE,{"disambiguationData":[TD([[makeQuery(id+"F3.imprint","IMPRINT",EDGE,{"disambiguationData":[TD([[subQ2,-1.0]])],"derivedFrom":subQ1}),-1.0]])]});}
            var Q248;
            {var subQ0=sQuery(id+"F3.wireOp",EDGE,"E8.0.3.0");var subQ1=sQuery(id+"F3.wireOp",EDGE,"E6.0.15.0");var subQ2=makeQuery(id+"F3.imprint","INTERSECT",VERTEX,{"derivedFrom":[subQ1,subQ0]});Q248=makeQuery(id+"F3.imprint","IMPRINT",FACE,{"disambiguationData":[TD([[makeQuery(id+"F3.imprint","IMPRINT",EDGE,{"disambiguationData":[TD([[subQ2,-1.0]])],"derivedFrom":subQ1}),-1.0]])]});}
            var Q249;
            {var subQ0=sQuery(id+"F3.wireOp",EDGE,"E8.0.3.0");var subQ1=sQuery(id+"F3.wireOp",EDGE,"E6.0.12.0");var subQ2=makeQuery(id+"F3.imprint","INTERSECT",VERTEX,{"derivedFrom":[subQ1,subQ0]});Q249=makeQuery(id+"F3.imprint","IMPRINT",FACE,{"disambiguationData":[TD([[makeQuery(id+"F3.imprint","IMPRINT",EDGE,{"disambiguationData":[TD([[subQ2,-1.0]])],"derivedFrom":subQ1}),-1.0]])]});}
            var Q250;
            {var subQ0=sQuery(id+"F3.wireOp",EDGE,"E8.0.13.0");var subQ1=sQuery(id+"F3.wireOp",EDGE,"E6.0.18.0");var subQ2=makeQuery(id+"F3.imprint","INTERSECT",VERTEX,{"derivedFrom":[subQ1,subQ0]});Q250=makeQuery(id+"F3.imprint","IMPRINT",FACE,{"disambiguationData":[TD([[makeQuery(id+"F3.imprint","IMPRINT",EDGE,{"disambiguationData":[TD([[subQ2,-1.0]])],"derivedFrom":subQ1}),-1.0]])]});}
            var Q251;
            {var subQ0=sQuery(id+"F3.wireOp",EDGE,"E8.0.13.0");var subQ1=sQuery(id+"F3.wireOp",EDGE,"E6.0.17.0");var subQ2=makeQuery(id+"F3.imprint","INTERSECT",VERTEX,{"derivedFrom":[subQ1,subQ0]});Q251=makeQuery(id+"F3.imprint","IMPRINT",FACE,{"disambiguationData":[TD([[makeQuery(id+"F3.imprint","IMPRINT",EDGE,{"disambiguationData":[TD([[subQ2,-1.0]])],"derivedFrom":subQ1}),-1.0]])]});}
            var Q252;
            {var subQ0=sQuery(id+"F3.wireOp",EDGE,"E8.0.13.0");var subQ1=sQuery(id+"F3.wireOp",EDGE,"E6.0.15.0");var subQ2=makeQuery(id+"F3.imprint","INTERSECT",VERTEX,{"derivedFrom":[subQ1,subQ0]});Q252=makeQuery(id+"F3.imprint","IMPRINT",FACE,{"disambiguationData":[TD([[makeQuery(id+"F3.imprint","IMPRINT",EDGE,{"disambiguationData":[TD([[subQ2,-1.0]])],"derivedFrom":subQ1}),-1.0]])]});}
            var Q253;
            {var subQ0=sQuery(id+"F3.wireOp",EDGE,"E8.0.13.0");var subQ1=sQuery(id+"F3.wireOp",EDGE,"E6.0.14.0");var subQ2=makeQuery(id+"F3.imprint","INTERSECT",VERTEX,{"derivedFrom":[subQ1,subQ0]});Q253=makeQuery(id+"F3.imprint","IMPRINT",FACE,{"disambiguationData":[TD([[makeQuery(id+"F3.imprint","IMPRINT",EDGE,{"disambiguationData":[TD([[subQ2,-1.0]])],"derivedFrom":subQ1}),-1.0]])]});}
            var Q254;
            {var subQ0=sQuery(id+"F3.wireOp",EDGE,"E8.0.12.0");var subQ1=sQuery(id+"F3.wireOp",EDGE,"E6.0.13.0");var subQ2=makeQuery(id+"F3.imprint","INTERSECT",VERTEX,{"derivedFrom":[subQ1,subQ0]});Q254=makeQuery(id+"F3.imprint","IMPRINT",FACE,{"disambiguationData":[TD([[makeQuery(id+"F3.imprint","IMPRINT",EDGE,{"disambiguationData":[TD([[subQ2,-1.0]])],"derivedFrom":subQ1}),-1.0]])]});}
            var Q255;
            {var subQ0=sQuery(id+"F3.wireOp",EDGE,"E8.0.13.0");var subQ1=sQuery(id+"F3.wireOp",EDGE,"E6.0.12.0");var subQ2=makeQuery(id+"F3.imprint","INTERSECT",VERTEX,{"derivedFrom":[subQ1,subQ0]});Q255=makeQuery(id+"F3.imprint","IMPRINT",FACE,{"disambiguationData":[TD([[makeQuery(id+"F3.imprint","IMPRINT",EDGE,{"disambiguationData":[TD([[subQ2,-1.0]])],"derivedFrom":subQ1}),-1.0]])]});}
            var Q256;
            {var subQ0=sQuery(id+"F3.wireOp",EDGE,"E8.0.13.0");var subQ1=sQuery(id+"F3.wireOp",EDGE,"E5.0.11.0");var subQ2=makeQuery(id+"F3.imprint","INTERSECT",VERTEX,{"derivedFrom":[subQ1,subQ0]});Q256=makeQuery(id+"F3.imprint","IMPRINT",FACE,{"disambiguationData":[TD([[makeQuery(id+"F3.imprint","IMPRINT",EDGE,{"disambiguationData":[TD([[subQ2,-1.0]])],"derivedFrom":subQ1}),-1.0]])]});}
            var Q257;
            {var subQ0=sQuery(id+"F3.wireOp",EDGE,"E8.0.13.0");var subQ1=sQuery(id+"F3.wireOp",EDGE,"E5.0.10.0");var subQ2=makeQuery(id+"F3.imprint","INTERSECT",VERTEX,{"derivedFrom":[subQ1,subQ0]});Q257=makeQuery(id+"F3.imprint","IMPRINT",FACE,{"disambiguationData":[TD([[makeQuery(id+"F3.imprint","IMPRINT",EDGE,{"disambiguationData":[TD([[subQ2,-1.0]])],"derivedFrom":subQ1}),-1.0]])]});}
            var Q258;
            {var subQ0=sQuery(id+"F3.wireOp",EDGE,"E8.0.4.0");var subQ1=sQuery(id+"F3.wireOp",EDGE,"E6.0.16.0");var subQ2=makeQuery(id+"F3.imprint","INTERSECT",VERTEX,{"derivedFrom":[subQ1,subQ0]});Q258=makeQuery(id+"F3.imprint","IMPRINT",FACE,{"disambiguationData":[TD([[makeQuery(id+"F3.imprint","IMPRINT",EDGE,{"disambiguationData":[TD([[subQ2,-1.0]])],"derivedFrom":subQ1}),-1.0]])]});}
            var Q259;
            {var subQ0=sQuery(id+"F3.wireOp",EDGE,"E8.0.4.0");var subQ1=sQuery(id+"F3.wireOp",EDGE,"E6.0.15.0");var subQ2=makeQuery(id+"F3.imprint","INTERSECT",VERTEX,{"derivedFrom":[subQ1,subQ0]});Q259=makeQuery(id+"F3.imprint","IMPRINT",FACE,{"disambiguationData":[TD([[makeQuery(id+"F3.imprint","IMPRINT",EDGE,{"disambiguationData":[TD([[subQ2,-1.0]])],"derivedFrom":subQ1}),-1.0]])]});}
            var Q260;
            {var subQ0=sQuery(id+"F3.wireOp",EDGE,"E8.0.4.0");var subQ1=sQuery(id+"F3.wireOp",EDGE,"E6.0.14.0");var subQ2=makeQuery(id+"F3.imprint","INTERSECT",VERTEX,{"derivedFrom":[subQ1,subQ0]});Q260=makeQuery(id+"F3.imprint","IMPRINT",FACE,{"disambiguationData":[TD([[makeQuery(id+"F3.imprint","IMPRINT",EDGE,{"disambiguationData":[TD([[subQ2,-1.0]])],"derivedFrom":subQ1}),-1.0]])]});}
            var Q261;
            {var subQ0=sQuery(id+"F3.wireOp",EDGE,"E8.0.4.0");var subQ1=sQuery(id+"F3.wireOp",EDGE,"E6.0.13.0");var subQ2=makeQuery(id+"F3.imprint","INTERSECT",VERTEX,{"derivedFrom":[subQ1,subQ0]});Q261=makeQuery(id+"F3.imprint","IMPRINT",FACE,{"disambiguationData":[TD([[makeQuery(id+"F3.imprint","IMPRINT",EDGE,{"disambiguationData":[TD([[subQ2,-1.0]])],"derivedFrom":subQ1}),-1.0]])]});}
            var Q262;
            {var subQ0=sQuery(id+"F3.wireOp",EDGE,"E8.0.4.0");var subQ1=sQuery(id+"F3.wireOp",EDGE,"E6.0.12.0");var subQ2=makeQuery(id+"F3.imprint","INTERSECT",VERTEX,{"derivedFrom":[subQ1,subQ0]});Q262=makeQuery(id+"F3.imprint","IMPRINT",FACE,{"disambiguationData":[TD([[makeQuery(id+"F3.imprint","IMPRINT",EDGE,{"disambiguationData":[TD([[subQ2,-1.0]])],"derivedFrom":subQ1}),-1.0]])]});}
            var Q263;
            {var subQ0=sQuery(id+"F3.wireOp",EDGE,"E8.0.4.0");var subQ1=sQuery(id+"F3.wireOp",EDGE,"E5.0.11.0");var subQ2=makeQuery(id+"F3.imprint","INTERSECT",VERTEX,{"derivedFrom":[subQ1,subQ0]});Q263=makeQuery(id+"F3.imprint","IMPRINT",FACE,{"disambiguationData":[TD([[makeQuery(id+"F3.imprint","IMPRINT",EDGE,{"disambiguationData":[TD([[subQ2,-1.0]])],"derivedFrom":subQ1}),-1.0]])]});}
            var Q264;
            {var subQ0=sQuery(id+"F3.wireOp",EDGE,"E8.0.4.0");var subQ1=sQuery(id+"F3.wireOp",EDGE,"E4.7.0.0");var subQ2=makeQuery(id+"F3.imprint","INTERSECT",VERTEX,{"derivedFrom":[subQ1,subQ0]});Q264=makeQuery(id+"F3.imprint","IMPRINT",FACE,{"disambiguationData":[TD([[makeQuery(id+"F3.imprint","IMPRINT",EDGE,{"disambiguationData":[TD([[subQ2,-1.0]])],"derivedFrom":subQ1}),-1.0]])]});}
            var Q265;
            {var subQ0=sQuery(id+"F3.wireOp",EDGE,"E8.0.4.0");var subQ1=sQuery(id+"F3.wireOp",EDGE,"E4.6.0.0");var subQ2=makeQuery(id+"F3.imprint","INTERSECT",VERTEX,{"derivedFrom":[subQ1,subQ0]});Q265=makeQuery(id+"F3.imprint","IMPRINT",FACE,{"disambiguationData":[TD([[makeQuery(id+"F3.imprint","IMPRINT",EDGE,{"disambiguationData":[TD([[subQ2,-1.0]])],"derivedFrom":subQ1}),-1.0]])]});}
            var Q266;
            {var subQ0=sQuery(id+"F3.wireOp",EDGE,"E8.0.4.0");var subQ1=sQuery(id+"F3.wireOp",EDGE,"E4.5.0.0");var subQ2=makeQuery(id+"F3.imprint","INTERSECT",VERTEX,{"derivedFrom":[subQ1,subQ0]});Q266=makeQuery(id+"F3.imprint","IMPRINT",FACE,{"disambiguationData":[TD([[makeQuery(id+"F3.imprint","IMPRINT",EDGE,{"disambiguationData":[TD([[subQ2,-1.0]])],"derivedFrom":subQ1}),-1.0]])]});}
            var Q267;
            {var subQ0=sQuery(id+"F3.wireOp",EDGE,"E8.0.4.0");var subQ1=sQuery(id+"F3.wireOp",EDGE,"E4.4.0.0");var subQ2=makeQuery(id+"F3.imprint","INTERSECT",VERTEX,{"derivedFrom":[subQ1,subQ0]});Q267=makeQuery(id+"F3.imprint","IMPRINT",FACE,{"disambiguationData":[TD([[makeQuery(id+"F3.imprint","IMPRINT",EDGE,{"disambiguationData":[TD([[subQ2,-1.0]])],"derivedFrom":subQ1}),-1.0]])]});}
            var Q268;
            {var subQ0=sQuery(id+"F3.wireOp",EDGE,"E8.0.13.0");var subQ1=sQuery(id+"F3.wireOp",EDGE,"E4.4.0.0");var subQ2=makeQuery(id+"F3.imprint","INTERSECT",VERTEX,{"derivedFrom":[subQ1,subQ0]});Q268=makeQuery(id+"F3.imprint","IMPRINT",FACE,{"disambiguationData":[TD([[makeQuery(id+"F3.imprint","IMPRINT",EDGE,{"disambiguationData":[TD([[subQ2,-1.0]])],"derivedFrom":subQ1}),-1.0]])]});}
            var Q269;
            {var subQ0=sQuery(id+"F3.wireOp",EDGE,"E8.0.13.0");var subQ1=sQuery(id+"F3.wireOp",EDGE,"E4.3.0.0");var subQ2=makeQuery(id+"F3.imprint","INTERSECT",VERTEX,{"derivedFrom":[subQ1,subQ0]});Q269=makeQuery(id+"F3.imprint","IMPRINT",FACE,{"disambiguationData":[TD([[makeQuery(id+"F3.imprint","IMPRINT",EDGE,{"disambiguationData":[TD([[subQ2,-1.0]])],"derivedFrom":subQ1}),-1.0]])]});}
            var Q270;
            {var subQ0=sQuery(id+"F3.wireOp",EDGE,"E8.0.12.0");var subQ1=sQuery(id+"F3.wireOp",EDGE,"E4.5.0.0");var subQ2=makeQuery(id+"F3.imprint","INTERSECT",VERTEX,{"derivedFrom":[subQ1,subQ0]});Q270=makeQuery(id+"F3.imprint","IMPRINT",FACE,{"disambiguationData":[TD([[makeQuery(id+"F3.imprint","IMPRINT",EDGE,{"disambiguationData":[TD([[subQ2,-1.0]])],"derivedFrom":subQ1}),-1.0]])]});}
            var Q271;
            {var subQ0=sQuery(id+"F3.wireOp",EDGE,"E8.0.9.0");var subQ1=sQuery(id+"F3.wireOp",EDGE,"E4.4.0.0");var subQ2=makeQuery(id+"F3.imprint","INTERSECT",VERTEX,{"derivedFrom":[subQ1,subQ0]});Q271=makeQuery(id+"F3.imprint","IMPRINT",FACE,{"disambiguationData":[TD([[makeQuery(id+"F3.imprint","IMPRINT",EDGE,{"disambiguationData":[TD([[subQ2,-1.0]])],"derivedFrom":subQ1}),-1.0]])]});}
            var Q272;
            {var subQ0=sQuery(id+"F3.wireOp",EDGE,"E8.0.8.0");var subQ1=sQuery(id+"F3.wireOp",EDGE,"E4.4.0.0");var subQ2=makeQuery(id+"F3.imprint","INTERSECT",VERTEX,{"derivedFrom":[subQ1,subQ0]});Q272=makeQuery(id+"F3.imprint","IMPRINT",FACE,{"disambiguationData":[TD([[makeQuery(id+"F3.imprint","IMPRINT",EDGE,{"disambiguationData":[TD([[subQ2,-1.0]])],"derivedFrom":subQ1}),-1.0]])]});}
            var Q273;
            {var subQ0=sQuery(id+"F3.wireOp",EDGE,"E8.0.8.0");var subQ1=sQuery(id+"F3.wireOp",EDGE,"E4.3.0.0");var subQ2=makeQuery(id+"F3.imprint","INTERSECT",VERTEX,{"derivedFrom":[subQ1,subQ0]});Q273=makeQuery(id+"F3.imprint","IMPRINT",FACE,{"disambiguationData":[TD([[makeQuery(id+"F3.imprint","IMPRINT",EDGE,{"disambiguationData":[TD([[subQ2,-1.0]])],"derivedFrom":subQ1}),-1.0]])]});}
            var Q274;
            {var subQ0=sQuery(id+"F3.wireOp",EDGE,"E8.0.7.0");var subQ1=sQuery(id+"F3.wireOp",EDGE,"E4.4.0.0");var subQ2=makeQuery(id+"F3.imprint","INTERSECT",VERTEX,{"derivedFrom":[subQ1,subQ0]});Q274=makeQuery(id+"F3.imprint","IMPRINT",FACE,{"disambiguationData":[TD([[makeQuery(id+"F3.imprint","IMPRINT",EDGE,{"disambiguationData":[TD([[subQ2,-1.0]])],"derivedFrom":subQ1}),-1.0]])]});}
            var Q275;
            {var subQ0=sQuery(id+"F3.wireOp",EDGE,"E8.0.6.0");var subQ1=sQuery(id+"F3.wireOp",EDGE,"E4.4.0.0");var subQ2=makeQuery(id+"F3.imprint","INTERSECT",VERTEX,{"derivedFrom":[subQ1,subQ0]});Q275=makeQuery(id+"F3.imprint","IMPRINT",FACE,{"disambiguationData":[TD([[makeQuery(id+"F3.imprint","IMPRINT",EDGE,{"disambiguationData":[TD([[subQ2,-1.0]])],"derivedFrom":subQ1}),-1.0]])]});}
            var Q276;
            {var subQ0=sQuery(id+"F3.wireOp",EDGE,"E8.0.5.0");var subQ1=sQuery(id+"F3.wireOp",EDGE,"E4.4.0.0");var subQ2=makeQuery(id+"F3.imprint","INTERSECT",VERTEX,{"derivedFrom":[subQ1,subQ0]});Q276=makeQuery(id+"F3.imprint","IMPRINT",FACE,{"disambiguationData":[TD([[makeQuery(id+"F3.imprint","IMPRINT",EDGE,{"disambiguationData":[TD([[subQ2,-1.0]])],"derivedFrom":subQ1}),-1.0]])]});}
            var Q277;
            {var subQ0=sQuery(id+"F3.wireOp",EDGE,"E8.0.5.0");var subQ1=sQuery(id+"F3.wireOp",EDGE,"E4.5.0.0");var subQ2=makeQuery(id+"F3.imprint","INTERSECT",VERTEX,{"derivedFrom":[subQ1,subQ0]});Q277=makeQuery(id+"F3.imprint","IMPRINT",FACE,{"disambiguationData":[TD([[makeQuery(id+"F3.imprint","IMPRINT",EDGE,{"disambiguationData":[TD([[subQ2,-1.0]])],"derivedFrom":subQ1}),-1.0]])]});}
            var Q278;
            {var subQ0=sQuery(id+"F3.wireOp",EDGE,"E8.0.5.0");var subQ1=sQuery(id+"F3.wireOp",EDGE,"E4.6.0.0");var subQ2=makeQuery(id+"F3.imprint","INTERSECT",VERTEX,{"derivedFrom":[subQ1,subQ0]});Q278=makeQuery(id+"F3.imprint","IMPRINT",FACE,{"disambiguationData":[TD([[makeQuery(id+"F3.imprint","IMPRINT",EDGE,{"disambiguationData":[TD([[subQ2,-1.0]])],"derivedFrom":subQ1}),-1.0]])]});}
            var Q279;
            {var subQ0=sQuery(id+"F3.wireOp",EDGE,"E8.0.5.0");var subQ1=sQuery(id+"F3.wireOp",EDGE,"E4.7.0.0");var subQ2=makeQuery(id+"F3.imprint","INTERSECT",VERTEX,{"derivedFrom":[subQ1,subQ0]});Q279=makeQuery(id+"F3.imprint","IMPRINT",FACE,{"disambiguationData":[TD([[makeQuery(id+"F3.imprint","IMPRINT",EDGE,{"disambiguationData":[TD([[subQ2,-1.0]])],"derivedFrom":subQ1}),-1.0]])]});}
            var Q280;
            {var subQ0=sQuery(id+"F3.wireOp",EDGE,"E8.0.7.0");var subQ1=sQuery(id+"F3.wireOp",EDGE,"E4.6.0.0");var subQ2=makeQuery(id+"F3.imprint","INTERSECT",VERTEX,{"derivedFrom":[subQ1,subQ0]});Q280=makeQuery(id+"F3.imprint","IMPRINT",FACE,{"disambiguationData":[TD([[makeQuery(id+"F3.imprint","IMPRINT",EDGE,{"disambiguationData":[TD([[subQ2,-1.0]])],"derivedFrom":subQ1}),-1.0]])]});}
            var Q281;
            {var subQ0=sQuery(id+"F3.wireOp",EDGE,"E8.0.5.0");var subQ1=sQuery(id+"F3.wireOp",EDGE,"E6.0.16.0");var subQ2=makeQuery(id+"F3.imprint","INTERSECT",VERTEX,{"derivedFrom":[subQ1,subQ0]});Q281=makeQuery(id+"F3.imprint","IMPRINT",FACE,{"disambiguationData":[TD([[makeQuery(id+"F3.imprint","IMPRINT",EDGE,{"disambiguationData":[TD([[subQ2,-1.0]])],"derivedFrom":subQ1}),-1.0]])]});}
            var Q282;
            {var subQ0=sQuery(id+"F3.wireOp",EDGE,"E8.0.5.0");var subQ1=sQuery(id+"F3.wireOp",EDGE,"E6.0.15.0");var subQ2=makeQuery(id+"F3.imprint","INTERSECT",VERTEX,{"derivedFrom":[subQ1,subQ0]});Q282=makeQuery(id+"F3.imprint","IMPRINT",FACE,{"disambiguationData":[TD([[makeQuery(id+"F3.imprint","IMPRINT",EDGE,{"disambiguationData":[TD([[subQ2,-1.0]])],"derivedFrom":subQ1}),-1.0]])]});}
            var Q283;
            {var subQ0=sQuery(id+"F3.wireOp",EDGE,"E8.0.5.0");var subQ1=sQuery(id+"F3.wireOp",EDGE,"E6.0.14.0");var subQ2=makeQuery(id+"F3.imprint","INTERSECT",VERTEX,{"derivedFrom":[subQ1,subQ0]});Q283=makeQuery(id+"F3.imprint","IMPRINT",FACE,{"disambiguationData":[TD([[makeQuery(id+"F3.imprint","IMPRINT",EDGE,{"disambiguationData":[TD([[subQ2,-1.0]])],"derivedFrom":subQ1}),-1.0]])]});}
            var Q284;
            {var subQ0=sQuery(id+"F3.wireOp",EDGE,"E8.0.5.0");var subQ1=sQuery(id+"F3.wireOp",EDGE,"E6.0.13.0");var subQ2=makeQuery(id+"F3.imprint","INTERSECT",VERTEX,{"derivedFrom":[subQ1,subQ0]});Q284=makeQuery(id+"F3.imprint","IMPRINT",FACE,{"disambiguationData":[TD([[makeQuery(id+"F3.imprint","IMPRINT",EDGE,{"disambiguationData":[TD([[subQ2,-1.0]])],"derivedFrom":subQ1}),-1.0]])]});}
            var Q285;
            {var subQ0=sQuery(id+"F3.wireOp",EDGE,"E8.0.5.0");var subQ1=sQuery(id+"F3.wireOp",EDGE,"E6.0.12.0");var subQ2=makeQuery(id+"F3.imprint","INTERSECT",VERTEX,{"derivedFrom":[subQ1,subQ0]});Q285=makeQuery(id+"F3.imprint","IMPRINT",FACE,{"disambiguationData":[TD([[makeQuery(id+"F3.imprint","IMPRINT",EDGE,{"disambiguationData":[TD([[subQ2,-1.0]])],"derivedFrom":subQ1}),-1.0]])]});}
            var Q286;
            {var subQ0=sQuery(id+"F3.wireOp",EDGE,"E8.0.5.0");var subQ1=sQuery(id+"F3.wireOp",EDGE,"E5.0.11.0");var subQ2=makeQuery(id+"F3.imprint","INTERSECT",VERTEX,{"derivedFrom":[subQ1,subQ0]});Q286=makeQuery(id+"F3.imprint","IMPRINT",FACE,{"disambiguationData":[TD([[makeQuery(id+"F3.imprint","IMPRINT",EDGE,{"disambiguationData":[TD([[subQ2,-1.0]])],"derivedFrom":subQ1}),-1.0]])]});}
            var Q287;
            {var subQ0=sQuery(id+"F3.wireOp",EDGE,"E8.0.5.0");var subQ1=sQuery(id+"F3.wireOp",EDGE,"E5.0.10.0");var subQ2=makeQuery(id+"F3.imprint","INTERSECT",VERTEX,{"derivedFrom":[subQ1,subQ0]});Q287=makeQuery(id+"F3.imprint","IMPRINT",FACE,{"disambiguationData":[TD([[makeQuery(id+"F3.imprint","IMPRINT",EDGE,{"disambiguationData":[TD([[subQ2,-1.0]])],"derivedFrom":subQ1}),-1.0]])]});}
            var Q288;
            {var subQ0=sQuery(id+"F3.wireOp",EDGE,"E8.0.5.0");var subQ1=sQuery(id+"F3.wireOp",EDGE,"E4.9.0.0");var subQ2=makeQuery(id+"F3.imprint","INTERSECT",VERTEX,{"derivedFrom":[subQ1,subQ0]});Q288=makeQuery(id+"F3.imprint","IMPRINT",FACE,{"disambiguationData":[TD([[makeQuery(id+"F3.imprint","IMPRINT",EDGE,{"disambiguationData":[TD([[subQ2,-1.0]])],"derivedFrom":subQ1}),-1.0]])]});}
            var Q289;
            {var subQ0=sQuery(id+"F3.wireOp",EDGE,"E8.0.5.0");var subQ1=sQuery(id+"F3.wireOp",EDGE,"E4.8.0.0");var subQ2=makeQuery(id+"F3.imprint","INTERSECT",VERTEX,{"derivedFrom":[subQ1,subQ0]});Q289=makeQuery(id+"F3.imprint","IMPRINT",FACE,{"disambiguationData":[TD([[makeQuery(id+"F3.imprint","IMPRINT",EDGE,{"disambiguationData":[TD([[subQ2,-1.0]])],"derivedFrom":subQ1}),-1.0]])]});}
            var Q290;
            {var subQ0=sQuery(id+"F3.wireOp",EDGE,"E8.0.6.0");var subQ1=sQuery(id+"F3.wireOp",EDGE,"E4.8.0.0");var subQ2=makeQuery(id+"F3.imprint","INTERSECT",VERTEX,{"derivedFrom":[subQ1,subQ0]});Q290=makeQuery(id+"F3.imprint","IMPRINT",FACE,{"disambiguationData":[TD([[makeQuery(id+"F3.imprint","IMPRINT",EDGE,{"disambiguationData":[TD([[subQ2,-1.0]])],"derivedFrom":subQ1}),-1.0]])]});}
            var Q291;
            {var subQ0=sQuery(id+"F3.wireOp",EDGE,"E8.0.6.0");var subQ1=sQuery(id+"F3.wireOp",EDGE,"E4.9.0.0");var subQ2=makeQuery(id+"F3.imprint","INTERSECT",VERTEX,{"derivedFrom":[subQ1,subQ0]});Q291=makeQuery(id+"F3.imprint","IMPRINT",FACE,{"disambiguationData":[TD([[makeQuery(id+"F3.imprint","IMPRINT",EDGE,{"disambiguationData":[TD([[subQ2,-1.0]])],"derivedFrom":subQ1}),-1.0]])]});}
            var Q292;
            {var subQ0=sQuery(id+"F3.wireOp",EDGE,"E8.0.6.0");var subQ1=sQuery(id+"F3.wireOp",EDGE,"E5.0.10.0");var subQ2=makeQuery(id+"F3.imprint","INTERSECT",VERTEX,{"derivedFrom":[subQ1,subQ0]});Q292=makeQuery(id+"F3.imprint","IMPRINT",FACE,{"disambiguationData":[TD([[makeQuery(id+"F3.imprint","IMPRINT",EDGE,{"disambiguationData":[TD([[subQ2,-1.0]])],"derivedFrom":subQ1}),-1.0]])]});}
            var Q293;
            {var subQ0=sQuery(id+"F3.wireOp",EDGE,"E8.0.6.0");var subQ1=sQuery(id+"F3.wireOp",EDGE,"E6.0.13.0");var subQ2=makeQuery(id+"F3.imprint","INTERSECT",VERTEX,{"derivedFrom":[subQ1,subQ0]});Q293=makeQuery(id+"F3.imprint","IMPRINT",FACE,{"disambiguationData":[TD([[makeQuery(id+"F3.imprint","IMPRINT",EDGE,{"disambiguationData":[TD([[subQ2,-1.0]])],"derivedFrom":subQ1}),-1.0]])]});}
            var Q294;
            {var subQ0=sQuery(id+"F3.wireOp",EDGE,"E8.0.6.0");var subQ1=sQuery(id+"F3.wireOp",EDGE,"E6.0.14.0");var subQ2=makeQuery(id+"F3.imprint","INTERSECT",VERTEX,{"derivedFrom":[subQ1,subQ0]});Q294=makeQuery(id+"F3.imprint","IMPRINT",FACE,{"disambiguationData":[TD([[makeQuery(id+"F3.imprint","IMPRINT",EDGE,{"disambiguationData":[TD([[subQ2,-1.0]])],"derivedFrom":subQ1}),-1.0]])]});}
            var Q295;
            {var subQ0=sQuery(id+"F3.wireOp",EDGE,"E8.0.7.0");var subQ1=sQuery(id+"F3.wireOp",EDGE,"E6.0.16.0");var subQ2=makeQuery(id+"F3.imprint","INTERSECT",VERTEX,{"derivedFrom":[subQ1,subQ0]});Q295=makeQuery(id+"F3.imprint","IMPRINT",FACE,{"disambiguationData":[TD([[makeQuery(id+"F3.imprint","IMPRINT",EDGE,{"disambiguationData":[TD([[subQ2,-1.0]])],"derivedFrom":subQ1}),-1.0]])]});}
            var Q296;
            {var subQ0=sQuery(id+"F3.wireOp",EDGE,"E8.0.7.0");var subQ1=sQuery(id+"F3.wireOp",EDGE,"E6.0.14.0");var subQ2=makeQuery(id+"F3.imprint","INTERSECT",VERTEX,{"derivedFrom":[subQ1,subQ0]});Q296=makeQuery(id+"F3.imprint","IMPRINT",FACE,{"disambiguationData":[TD([[makeQuery(id+"F3.imprint","IMPRINT",EDGE,{"disambiguationData":[TD([[subQ2,-1.0]])],"derivedFrom":subQ1}),-1.0]])]});}
            var Q297;
            {var subQ0=sQuery(id+"F3.wireOp",EDGE,"E8.0.7.0");var subQ1=sQuery(id+"F3.wireOp",EDGE,"E6.0.12.0");var subQ2=makeQuery(id+"F3.imprint","INTERSECT",VERTEX,{"derivedFrom":[subQ1,subQ0]});Q297=makeQuery(id+"F3.imprint","IMPRINT",FACE,{"disambiguationData":[TD([[makeQuery(id+"F3.imprint","IMPRINT",EDGE,{"disambiguationData":[TD([[subQ2,-1.0]])],"derivedFrom":subQ1}),-1.0]])]});}
            var Q298;
            {var subQ0=sQuery(id+"F3.wireOp",EDGE,"E8.0.7.0");var subQ1=sQuery(id+"F3.wireOp",EDGE,"E5.0.10.0");var subQ2=makeQuery(id+"F3.imprint","INTERSECT",VERTEX,{"derivedFrom":[subQ1,subQ0]});Q298=makeQuery(id+"F3.imprint","IMPRINT",FACE,{"disambiguationData":[TD([[makeQuery(id+"F3.imprint","IMPRINT",EDGE,{"disambiguationData":[TD([[subQ2,-1.0]])],"derivedFrom":subQ1}),-1.0]])]});}
            var Q299;
            {var subQ0=sQuery(id+"F3.wireOp",EDGE,"E8.0.7.0");var subQ1=sQuery(id+"F3.wireOp",EDGE,"E4.8.0.0");var subQ2=makeQuery(id+"F3.imprint","INTERSECT",VERTEX,{"derivedFrom":[subQ1,subQ0]});Q299=makeQuery(id+"F3.imprint","IMPRINT",FACE,{"disambiguationData":[TD([[makeQuery(id+"F3.imprint","IMPRINT",EDGE,{"disambiguationData":[TD([[subQ2,-1.0]])],"derivedFrom":subQ1}),-1.0]])]});}
            var Q300;
            {var subQ0=sQuery(id+"F3.wireOp",EDGE,"E8.0.8.0");var subQ1=sQuery(id+"F3.wireOp",EDGE,"E6.0.16.0");var subQ2=makeQuery(id+"F3.imprint","INTERSECT",VERTEX,{"derivedFrom":[subQ1,subQ0]});Q300=makeQuery(id+"F3.imprint","IMPRINT",FACE,{"disambiguationData":[TD([[makeQuery(id+"F3.imprint","IMPRINT",EDGE,{"disambiguationData":[TD([[subQ2,-1.0]])],"derivedFrom":subQ1}),-1.0]])]});}
            var Q301;
            {var subQ0=sQuery(id+"F3.wireOp",EDGE,"E8.0.8.0");var subQ1=sQuery(id+"F3.wireOp",EDGE,"E6.0.15.0");var subQ2=makeQuery(id+"F3.imprint","INTERSECT",VERTEX,{"derivedFrom":[subQ1,subQ0]});Q301=makeQuery(id+"F3.imprint","IMPRINT",FACE,{"disambiguationData":[TD([[makeQuery(id+"F3.imprint","IMPRINT",EDGE,{"disambiguationData":[TD([[subQ2,-1.0]])],"derivedFrom":subQ1}),-1.0]])]});}
            var Q302;
            {var subQ0=sQuery(id+"F3.wireOp",EDGE,"E8.0.8.0");var subQ1=sQuery(id+"F3.wireOp",EDGE,"E6.0.14.0");var subQ2=makeQuery(id+"F3.imprint","INTERSECT",VERTEX,{"derivedFrom":[subQ1,subQ0]});Q302=makeQuery(id+"F3.imprint","IMPRINT",FACE,{"disambiguationData":[TD([[makeQuery(id+"F3.imprint","IMPRINT",EDGE,{"disambiguationData":[TD([[subQ2,-1.0]])],"derivedFrom":subQ1}),-1.0]])]});}
            var Q303;
            {var subQ0=sQuery(id+"F3.wireOp",EDGE,"E8.0.8.0");var subQ1=sQuery(id+"F3.wireOp",EDGE,"E6.0.13.0");var subQ2=makeQuery(id+"F3.imprint","INTERSECT",VERTEX,{"derivedFrom":[subQ1,subQ0]});Q303=makeQuery(id+"F3.imprint","IMPRINT",FACE,{"disambiguationData":[TD([[makeQuery(id+"F3.imprint","IMPRINT",EDGE,{"disambiguationData":[TD([[subQ2,-1.0]])],"derivedFrom":subQ1}),-1.0]])]});}
            var Q304;
            {var subQ0=sQuery(id+"F3.wireOp",EDGE,"E8.0.11.0");var subQ1=sQuery(id+"F3.wireOp",EDGE,"E6.0.15.0");var subQ2=makeQuery(id+"F3.imprint","INTERSECT",VERTEX,{"derivedFrom":[subQ1,subQ0]});Q304=makeQuery(id+"F3.imprint","IMPRINT",FACE,{"disambiguationData":[TD([[makeQuery(id+"F3.imprint","IMPRINT",EDGE,{"disambiguationData":[TD([[subQ2,-1.0]])],"derivedFrom":subQ1}),-1.0]])]});}
            var Q305;
            {var subQ0=sQuery(id+"F3.wireOp",EDGE,"E8.0.11.0");var subQ1=sQuery(id+"F3.wireOp",EDGE,"E6.0.14.0");var subQ2=makeQuery(id+"F3.imprint","INTERSECT",VERTEX,{"derivedFrom":[subQ1,subQ0]});Q305=makeQuery(id+"F3.imprint","IMPRINT",FACE,{"disambiguationData":[TD([[makeQuery(id+"F3.imprint","IMPRINT",EDGE,{"disambiguationData":[TD([[subQ2,-1.0]])],"derivedFrom":subQ1}),-1.0]])]});}
            var Q306;
            {var subQ0=sQuery(id+"F3.wireOp",EDGE,"E8.0.10.0");var subQ1=sQuery(id+"F3.wireOp",EDGE,"E6.0.14.0");var subQ2=makeQuery(id+"F3.imprint","INTERSECT",VERTEX,{"derivedFrom":[subQ1,subQ0]});Q306=makeQuery(id+"F3.imprint","IMPRINT",FACE,{"disambiguationData":[TD([[makeQuery(id+"F3.imprint","IMPRINT",EDGE,{"disambiguationData":[TD([[subQ2,-1.0]])],"derivedFrom":subQ1}),-1.0]])]});}
            var Q307;
            {var subQ0=sQuery(id+"F3.wireOp",EDGE,"E8.0.9.0");var subQ1=sQuery(id+"F3.wireOp",EDGE,"E6.0.14.0");var subQ2=makeQuery(id+"F3.imprint","INTERSECT",VERTEX,{"derivedFrom":[subQ1,subQ0]});Q307=makeQuery(id+"F3.imprint","IMPRINT",FACE,{"disambiguationData":[TD([[makeQuery(id+"F3.imprint","IMPRINT",EDGE,{"disambiguationData":[TD([[subQ2,-1.0]])],"derivedFrom":subQ1}),-1.0]])]});}
            var Q308;
            {var subQ0=sQuery(id+"F3.wireOp",EDGE,"E8.0.11.0");var subQ1=sQuery(id+"F3.wireOp",EDGE,"E6.0.12.0");var subQ2=makeQuery(id+"F3.imprint","INTERSECT",VERTEX,{"derivedFrom":[subQ1,subQ0]});Q308=makeQuery(id+"F3.imprint","IMPRINT",FACE,{"disambiguationData":[TD([[makeQuery(id+"F3.imprint","IMPRINT",EDGE,{"disambiguationData":[TD([[subQ2,-1.0]])],"derivedFrom":subQ1}),-1.0]])]});}
            var Q309;
            {var subQ0=sQuery(id+"F3.wireOp",EDGE,"E8.0.11.0");var subQ1=sQuery(id+"F3.wireOp",EDGE,"E5.0.11.0");var subQ2=makeQuery(id+"F3.imprint","INTERSECT",VERTEX,{"derivedFrom":[subQ1,subQ0]});Q309=makeQuery(id+"F3.imprint","IMPRINT",FACE,{"disambiguationData":[TD([[makeQuery(id+"F3.imprint","IMPRINT",EDGE,{"disambiguationData":[TD([[subQ2,-1.0]])],"derivedFrom":subQ1}),-1.0]])]});}
            var Q310;
            {var subQ0=sQuery(id+"F3.wireOp",EDGE,"E8.0.11.0");var subQ1=sQuery(id+"F3.wireOp",EDGE,"E5.0.10.0");var subQ2=makeQuery(id+"F3.imprint","INTERSECT",VERTEX,{"derivedFrom":[subQ1,subQ0]});Q310=makeQuery(id+"F3.imprint","IMPRINT",FACE,{"disambiguationData":[TD([[makeQuery(id+"F3.imprint","IMPRINT",EDGE,{"disambiguationData":[TD([[subQ2,-1.0]])],"derivedFrom":subQ1}),-1.0]])]});}
            var Q311;
            {var subQ0=sQuery(id+"F3.wireOp",EDGE,"E8.0.11.0");var subQ1=sQuery(id+"F3.wireOp",EDGE,"E4.9.0.0");var subQ2=makeQuery(id+"F3.imprint","INTERSECT",VERTEX,{"derivedFrom":[subQ1,subQ0]});Q311=makeQuery(id+"F3.imprint","IMPRINT",FACE,{"disambiguationData":[TD([[makeQuery(id+"F3.imprint","IMPRINT",EDGE,{"disambiguationData":[TD([[subQ2,-1.0]])],"derivedFrom":subQ1}),-1.0]])]});}
            var Q312;
            {var subQ0=sQuery(id+"F3.wireOp",EDGE,"E8.0.11.0");var subQ1=sQuery(id+"F3.wireOp",EDGE,"E4.7.0.0");var subQ2=makeQuery(id+"F3.imprint","INTERSECT",VERTEX,{"derivedFrom":[subQ1,subQ0]});Q312=makeQuery(id+"F3.imprint","IMPRINT",FACE,{"disambiguationData":[TD([[makeQuery(id+"F3.imprint","IMPRINT",EDGE,{"disambiguationData":[TD([[subQ2,-1.0]])],"derivedFrom":subQ1}),-1.0]])]});}
            var Q313;
            {var subQ0=sQuery(id+"F3.wireOp",EDGE,"E8.0.10.0");var subQ1=sQuery(id+"F3.wireOp",EDGE,"E4.9.0.0");var subQ2=makeQuery(id+"F3.imprint","INTERSECT",VERTEX,{"derivedFrom":[subQ1,subQ0]});Q313=makeQuery(id+"F3.imprint","IMPRINT",FACE,{"disambiguationData":[TD([[makeQuery(id+"F3.imprint","IMPRINT",EDGE,{"disambiguationData":[TD([[subQ2,-1.0]])],"derivedFrom":subQ1}),-1.0]])]});}
            var Q314;
            {var subQ0=sQuery(id+"F3.wireOp",EDGE,"E8.0.10.0");var subQ1=sQuery(id+"F3.wireOp",EDGE,"E4.8.0.0");var subQ2=makeQuery(id+"F3.imprint","INTERSECT",VERTEX,{"derivedFrom":[subQ1,subQ0]});Q314=makeQuery(id+"F3.imprint","IMPRINT",FACE,{"disambiguationData":[TD([[makeQuery(id+"F3.imprint","IMPRINT",EDGE,{"disambiguationData":[TD([[subQ2,-1.0]])],"derivedFrom":subQ1}),-1.0]])]});}
            var Q315;
            {var subQ0=sQuery(id+"F3.wireOp",EDGE,"E8.0.11.0");var subQ1=sQuery(id+"F3.wireOp",EDGE,"E4.8.0.0");var subQ2=makeQuery(id+"F3.imprint","INTERSECT",VERTEX,{"derivedFrom":[subQ1,subQ0]});Q315=makeQuery(id+"F3.imprint","IMPRINT",FACE,{"disambiguationData":[TD([[makeQuery(id+"F3.imprint","IMPRINT",EDGE,{"disambiguationData":[TD([[subQ2,-1.0]])],"derivedFrom":subQ1}),-1.0]])]});}
            var Q316;
            {var subQ0=sQuery(id+"F3.wireOp",EDGE,"E8.0.12.0");var subQ1=sQuery(id+"F3.wireOp",EDGE,"E4.8.0.0");var subQ2=makeQuery(id+"F3.imprint","INTERSECT",VERTEX,{"derivedFrom":[subQ1,subQ0]});Q316=makeQuery(id+"F3.imprint","IMPRINT",FACE,{"disambiguationData":[TD([[makeQuery(id+"F3.imprint","IMPRINT",EDGE,{"disambiguationData":[TD([[subQ2,-1.0]])],"derivedFrom":subQ1}),-1.0]])]});}
            var Q317;
            {var subQ0=sQuery(id+"F3.wireOp",EDGE,"E8.0.9.0");var subQ1=sQuery(id+"F3.wireOp",EDGE,"E6.0.12.0");var subQ2=makeQuery(id+"F3.imprint","INTERSECT",VERTEX,{"derivedFrom":[subQ1,subQ0]});Q317=makeQuery(id+"F3.imprint","IMPRINT",FACE,{"disambiguationData":[TD([[makeQuery(id+"F3.imprint","IMPRINT",EDGE,{"disambiguationData":[TD([[subQ2,-1.0]])],"derivedFrom":subQ1}),-1.0]])]});}
            var Q318;
            {var subQ0=sQuery(id+"F3.wireOp",EDGE,"E8.0.9.0");var subQ1=sQuery(id+"F3.wireOp",EDGE,"E5.0.11.0");var subQ2=makeQuery(id+"F3.imprint","INTERSECT",VERTEX,{"derivedFrom":[subQ1,subQ0]});Q318=makeQuery(id+"F3.imprint","IMPRINT",FACE,{"disambiguationData":[TD([[makeQuery(id+"F3.imprint","IMPRINT",EDGE,{"disambiguationData":[TD([[subQ2,-1.0]])],"derivedFrom":subQ1}),-1.0]])]});}
            var Q319;
            {var subQ0=sQuery(id+"F3.wireOp",EDGE,"E8.0.9.0");var subQ1=sQuery(id+"F3.wireOp",EDGE,"E5.0.10.0");var subQ2=makeQuery(id+"F3.imprint","INTERSECT",VERTEX,{"derivedFrom":[subQ1,subQ0]});Q319=makeQuery(id+"F3.imprint","IMPRINT",FACE,{"disambiguationData":[TD([[makeQuery(id+"F3.imprint","IMPRINT",EDGE,{"disambiguationData":[TD([[subQ2,-1.0]])],"derivedFrom":subQ1}),-1.0]])]});}
            var Q320;
            {var subQ0=sQuery(id+"F3.wireOp",EDGE,"E8.0.8.0");var subQ1=sQuery(id+"F3.wireOp",EDGE,"E4.9.0.0");var subQ2=makeQuery(id+"F3.imprint","INTERSECT",VERTEX,{"derivedFrom":[subQ1,subQ0]});Q320=makeQuery(id+"F3.imprint","IMPRINT",FACE,{"disambiguationData":[TD([[makeQuery(id+"F3.imprint","IMPRINT",EDGE,{"disambiguationData":[TD([[subQ2,-1.0]])],"derivedFrom":subQ1}),-1.0]])]});}
            var Q321;
            {var subQ0=sQuery(id+"F3.wireOp",EDGE,"E8.0.9.0");var subQ1=sQuery(id+"F3.wireOp",EDGE,"E4.8.0.0");var subQ2=makeQuery(id+"F3.imprint","INTERSECT",VERTEX,{"derivedFrom":[subQ1,subQ0]});Q321=makeQuery(id+"F3.imprint","IMPRINT",FACE,{"disambiguationData":[TD([[makeQuery(id+"F3.imprint","IMPRINT",EDGE,{"disambiguationData":[TD([[subQ2,-1.0]])],"derivedFrom":subQ1}),-1.0]])]});}
            var Q322;
            {var subQ0=sQuery(id+"F3.wireOp",EDGE,"E8.0.9.0");var subQ1=sQuery(id+"F3.wireOp",EDGE,"E4.7.0.0");var subQ2=makeQuery(id+"F3.imprint","INTERSECT",VERTEX,{"derivedFrom":[subQ1,subQ0]});Q322=makeQuery(id+"F3.imprint","IMPRINT",FACE,{"disambiguationData":[TD([[makeQuery(id+"F3.imprint","IMPRINT",EDGE,{"disambiguationData":[TD([[subQ2,-1.0]])],"derivedFrom":subQ1}),-1.0]])]});}
            var Q323;
            {var subQ0=sQuery(id+"F3.wireOp",EDGE,"E8.0.9.0");var subQ1=sQuery(id+"F3.wireOp",EDGE,"E4.6.0.0");var subQ2=makeQuery(id+"F3.imprint","INTERSECT",VERTEX,{"derivedFrom":[subQ1,subQ0]});Q323=makeQuery(id+"F3.imprint","IMPRINT",FACE,{"disambiguationData":[TD([[makeQuery(id+"F3.imprint","IMPRINT",EDGE,{"disambiguationData":[TD([[subQ2,-1.0]])],"derivedFrom":subQ1}),-1.0]])]});}
            var Q324;
            {var subQ0=sQuery(id+"F3.wireOp",EDGE,"E8.0.9.0");var subQ1=sQuery(id+"F3.wireOp",EDGE,"E4.5.0.0");var subQ2=makeQuery(id+"F3.imprint","INTERSECT",VERTEX,{"derivedFrom":[subQ1,subQ0]});Q324=makeQuery(id+"F3.imprint","IMPRINT",FACE,{"disambiguationData":[TD([[makeQuery(id+"F3.imprint","IMPRINT",EDGE,{"disambiguationData":[TD([[subQ2,-1.0]])],"derivedFrom":subQ1}),-1.0]])]});}
            var Q325;
            {var subQ0=sQuery(id+"F3.wireOp",EDGE,"E8.0.9.0");var subQ1=sQuery(id+"F3.wireOp",EDGE,"E6.0.16.0");var subQ2=makeQuery(id+"F3.imprint","INTERSECT",VERTEX,{"derivedFrom":[subQ1,subQ0]});Q325=makeQuery(id+"F3.imprint","IMPRINT",FACE,{"disambiguationData":[TD([[makeQuery(id+"F3.imprint","IMPRINT",EDGE,{"disambiguationData":[TD([[subQ2,-1.0]])],"derivedFrom":subQ1}),-1.0]])]});}
            var Q326;
            {var subQ0=sQuery(id+"F3.wireOp",EDGE,"E8.0.14.0");var subQ1=sQuery(id+"F3.wireOp",EDGE,"E4.4.0.0");var subQ2=makeQuery(id+"F3.imprint","INTERSECT",VERTEX,{"derivedFrom":[subQ1,subQ0]});Q326=makeQuery(id+"F3.imprint","IMPRINT",FACE,{"disambiguationData":[TD([[makeQuery(id+"F3.imprint","IMPRINT",EDGE,{"disambiguationData":[TD([[subQ2,-1.0]])],"derivedFrom":subQ1}),-1.0]])]});}
            var Q327;
            {var subQ0=sQuery(id+"F3.wireOp",EDGE,"E8.0.13.0");var subQ1=sQuery(id+"F3.wireOp",EDGE,"E4.7.0.0");var subQ2=makeQuery(id+"F3.imprint","INTERSECT",VERTEX,{"derivedFrom":[subQ1,subQ0]});Q327=makeQuery(id+"F3.imprint","IMPRINT",FACE,{"disambiguationData":[TD([[makeQuery(id+"F3.imprint","IMPRINT",EDGE,{"disambiguationData":[TD([[subQ2,-1.0]])],"derivedFrom":subQ1}),-1.0]])]});}
            var Q328;
            {var subQ0=sQuery(id+"F3.wireOp",EDGE,"E8.0.13.0");var subQ1=sQuery(id+"F3.wireOp",EDGE,"E4.6.0.0");var subQ2=makeQuery(id+"F3.imprint","INTERSECT",VERTEX,{"derivedFrom":[subQ1,subQ0]});Q328=makeQuery(id+"F3.imprint","IMPRINT",FACE,{"disambiguationData":[TD([[makeQuery(id+"F3.imprint","IMPRINT",EDGE,{"disambiguationData":[TD([[subQ2,-1.0]])],"derivedFrom":subQ1}),-1.0]])]});}
            var Q329;
            {var subQ0=sQuery(id+"F3.wireOp",EDGE,"E8.0.14.0");var subQ1=sQuery(id+"F3.wireOp",EDGE,"E4.6.0.0");var subQ2=makeQuery(id+"F3.imprint","INTERSECT",VERTEX,{"derivedFrom":[subQ1,subQ0]});Q329=makeQuery(id+"F3.imprint","IMPRINT",FACE,{"disambiguationData":[TD([[makeQuery(id+"F3.imprint","IMPRINT",EDGE,{"disambiguationData":[TD([[subQ2,-1.0]])],"derivedFrom":subQ1}),-1.0]])]});}
            var Q330;
            {var subQ0=sQuery(id+"F3.wireOp",EDGE,"E8.0.14.0");var subQ1=sQuery(id+"F3.wireOp",EDGE,"E4.7.0.0");var subQ2=makeQuery(id+"F3.imprint","INTERSECT",VERTEX,{"derivedFrom":[subQ1,subQ0]});Q330=makeQuery(id+"F3.imprint","IMPRINT",FACE,{"disambiguationData":[TD([[makeQuery(id+"F3.imprint","IMPRINT",EDGE,{"disambiguationData":[TD([[subQ2,-1.0]])],"derivedFrom":subQ1}),-1.0]])]});}
            var Q331;
            {var subQ0=sQuery(id+"F3.wireOp",EDGE,"E8.0.15.0");var subQ1=sQuery(id+"F3.wireOp",EDGE,"E4.6.0.0");var subQ2=makeQuery(id+"F3.imprint","INTERSECT",VERTEX,{"derivedFrom":[subQ1,subQ0]});Q331=makeQuery(id+"F3.imprint","IMPRINT",FACE,{"disambiguationData":[TD([[makeQuery(id+"F3.imprint","IMPRINT",EDGE,{"disambiguationData":[TD([[subQ2,-1.0]])],"derivedFrom":subQ1}),-1.0]])]});}
            var Q332;
            {var subQ0=sQuery(id+"F3.wireOp",EDGE,"E8.0.9.0");var subQ1=sQuery(id+"F3.wireOp",EDGE,"E6.0.17.0");var subQ2=makeQuery(id+"F3.imprint","INTERSECT",VERTEX,{"derivedFrom":[subQ1,subQ0]});Q332=makeQuery(id+"F3.imprint","IMPRINT",FACE,{"disambiguationData":[TD([[makeQuery(id+"F3.imprint","IMPRINT",EDGE,{"disambiguationData":[TD([[subQ2,-1.0]])],"derivedFrom":subQ1}),-1.0]])]});}
            extrude(context, id + "F4", {"entities" : qUnion([Q0, Q1, Q2, Q3, Q4, Q5, Q6, Q7, Q8, Q9, Q10, Q11, Q12, Q13, Q14, Q15, Q16, Q17, Q18, Q19, Q20, Q21, Q22, Q23, Q24, Q25, Q26, Q27, Q28, Q29, Q30, Q31, Q32, Q33, Q34, Q35, Q36, Q37, Q38, Q39, Q40, Q41, Q42, Q43, Q44, Q45, Q46, Q47, Q48, Q49, Q50, Q51, Q52, Q53, Q54, Q55, Q56, Q57, Q58, Q59, Q60, Q61, Q62, Q63, Q64, Q65, Q66, Q67, Q68, Q69, Q70, Q71, Q72, Q73, Q74, Q75, Q76, Q77, Q78, Q79, Q80, Q81, Q82, Q83, Q84, Q85, Q86, Q87, Q88, Q89, Q90, Q91, Q92, Q93, Q94, Q95, Q96, Q97, Q98, Q99, Q100, Q101, Q102, Q103, Q104, Q105, Q106, Q107, Q108, Q109, Q110, Q111, Q112, Q113, Q114, Q115, Q116, Q117, Q118, Q119, Q120, Q121, Q122, Q123, Q124, Q125, Q126, Q127, Q128, Q129, Q130, Q131, Q132, Q133, Q134, Q135, Q136, Q137, Q138, Q139, Q140, Q141, Q142, Q143, Q144, Q145, Q146, Q147, Q148, Q149, Q150, Q151, Q152, Q153, Q154, Q155, Q156, Q157, Q158, Q159, Q160, Q161, Q162, Q163, Q164, Q165, Q166, Q167, Q168, Q169, Q170, Q171, Q172, Q173, Q174, Q175, Q176, Q177, Q178, Q179, Q180, Q181, Q182, Q183, Q184, Q185, Q186, Q187, Q188, Q189, Q190, Q191, Q192, Q193, Q194, Q195, Q196, Q197, Q198, Q199, Q200, Q201, Q202, Q203, Q204, Q205, Q206, Q207, Q208, Q209, Q210, Q211, Q212, Q213, Q214, Q215, Q216, Q217, Q218, Q219, Q220, Q221, Q222, Q223, Q224, Q225, Q226, Q227, Q228, Q229, Q230, Q231, Q232, Q233, Q234, Q235, Q236, Q237, Q238, Q239, Q240, Q241, Q242, Q243, Q244, Q245, Q246, Q247, Q248, Q249, Q250, Q251, Q252, Q253, Q254, Q255, Q256, Q257, Q258, Q259, Q260, Q261, Q262, Q263, Q264, Q265, Q266, Q267, Q268, Q269, Q270, Q271, Q272, Q273, Q274, Q275, Q276, Q277, Q278, Q279, Q280, Q281, Q282, Q283, Q284, Q285, Q286, Q287, Q288, Q289, Q290, Q291, Q292, Q293, Q294, Q295, Q296, Q297, Q298, Q299, Q300, Q301, Q302, Q303, Q304, Q305, Q306, Q307, Q308, Q309, Q310, Q311, Q312, Q313, Q314, Q315, Q316, Q317, Q318, Q319, Q320, Q321, Q322, Q323, Q324, Q325, Q326, Q327, Q328, Q329, Q330, Q331, Q332]), "depth" : 1 * mm, "offsetDistance" : 25 * mm});
        }
        {
            var Q0;
            Q0=qCreatedBy(makeId("Top.planeOp"),FACE);
            var sketch = newSketch(context, id + "F5", { "sketchPlane" : qUnion([Q0])});
            skLineSegment(sketch, "E9.bottom", {"start": v(-9.9, -2.7) * mm, "end": v(-8.1, -2.7) * mm});
            skLineSegment(sketch, "E9.top", {"start": v(-9.9, -0.9) * mm, "end": v(-8.1, -0.9) * mm});
            skLineSegment(sketch, "E9.left", {"start": v(-9.9, -2.7) * mm, "end": v(-9.9, -0.9) * mm});
            skLineSegment(sketch, "E9.right", {"start": v(-8.1, -2.7) * mm, "end": v(-8.1, -0.9) * mm});
            skLineSegment(sketch, "E10.bottom", {"start": v(-9.9, -4.5) * mm, "end": v(-6.3, -4.5) * mm});
            skLineSegment(sketch, "E10.top", {"start": v(-9.9, -6.3) * mm, "end": v(-6.3, -6.3) * mm});
            skLineSegment(sketch, "E10.left", {"start": v(-9.9, -4.5) * mm, "end": v(-9.9, -6.3) * mm});
            skLineSegment(sketch, "E10.right", {"start": v(-6.3, -4.5) * mm, "end": v(-6.3, -6.3) * mm});
            skLineSegment(sketch, "E11.bottom", {"start": v(6.3, -8.1) * mm, "end": v(8.1, -8.1) * mm});
            skLineSegment(sketch, "E11.top", {"start": v(6.3, -9.9) * mm, "end": v(8.1, -9.9) * mm});
            skLineSegment(sketch, "E11.left", {"start": v(6.3, -8.1) * mm, "end": v(6.3, -9.9) * mm});
            skLineSegment(sketch, "E11.right", {"start": v(8.1, -8.1) * mm, "end": v(8.1, -9.9) * mm});
            skLineSegment(sketch, "E12.bottom", {"start": v(15.3, 2.7) * mm, "end": v(17.1, 2.7) * mm});
            skLineSegment(sketch, "E12.top", {"start": v(15.3, 0.9) * mm, "end": v(17.1, 0.9) * mm});
            skLineSegment(sketch, "E12.left", {"start": v(15.3, 2.7) * mm, "end": v(15.3, 0.9) * mm});
            skLineSegment(sketch, "E12.right", {"start": v(17.1, 2.7) * mm, "end": v(17.1, 0.9) * mm});
            skSolve(sketch);
        }
        {
            var Q0;
            Q0 = qSketchRegion(id + "F5", true);
            extrude(context, id + "F6", {"entities" : qUnion([Q0]), "depth" : 1 * mm, "offsetDistance" : 25 * mm});
        }
        {
            var Q0;
            Q0=makeQuery(id+"F1.opExtrude","CAP_EDGE",EDGE,{"disambiguationData":[OSD([sQuery(id+"F0.wireOp",EDGE,"E2")])],"isStart":true});
            var Q1;
            Q1=makeQuery(id+"F1.opExtrude","CAP_EDGE",EDGE,{"disambiguationData":[OSD([sQuery(id+"F0.wireOp",EDGE,"E2")])],"isStart":false});
            var Q2;
            Q2=makeQuery(id+"F1.opExtrude","CAP_EDGE",EDGE,{"disambiguationData":[OSD([sQuery(id+"F0.wireOp",EDGE,"E0.bottom")])],"isStart":true});
            fillet(context, id + "F7", {"entities" : qUnion([Q0, Q1, Q2]), "radius" : 0.5 * mm, "tangentPropagation" : true, "allowEdgeOverflow" : false});
        }
    });
